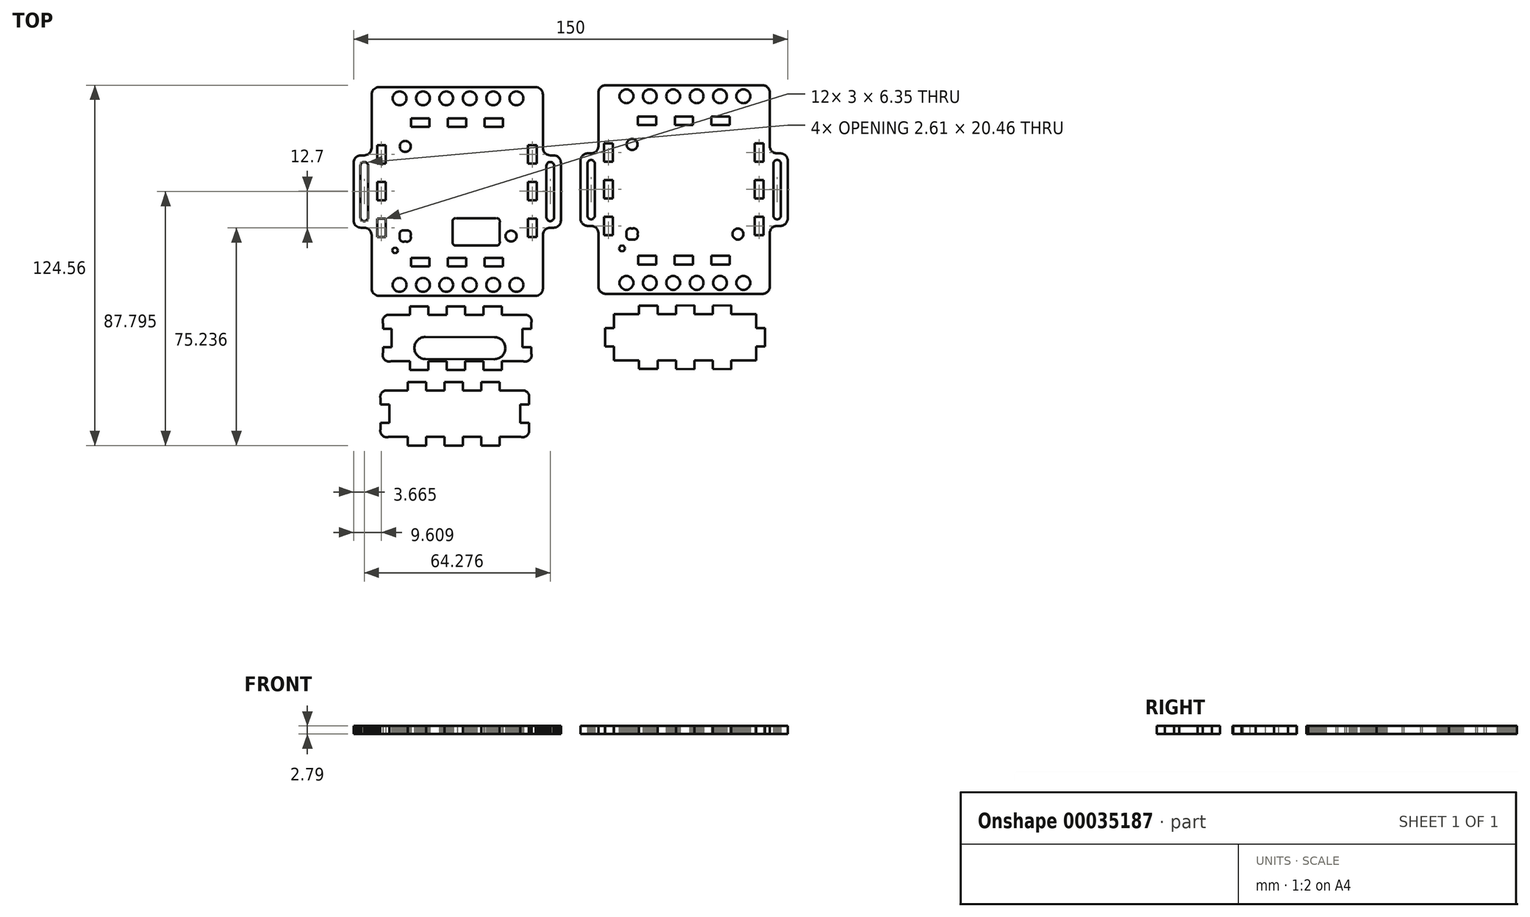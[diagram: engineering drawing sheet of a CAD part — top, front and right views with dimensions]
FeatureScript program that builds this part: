
annotation { "Feature Type Name" : "Feature", "Feature Type Description" : "" }
export const myFeature = defineFeature(function(context is Context, id is Id, definition is map)
    precondition{}
    {
        {
            var Q0;
            Q0=qCreatedBy(makeId("Top.planeOp"),FACE);
            var sketch = newSketch(context, id + "F0", { "sketchPlane" : qUnion([Q0])});
            skLineSegment(sketch, "E0", {"start": v(15.08, -72.64) * mm, "end": v(23.78, -72.67) * mm});
            skLineSegment(sketch, "E1", {"start": v(15.08, -67.86) * mm, "end": v(15.08, -72.64) * mm});
            skLineSegment(sketch, "E2", {"start": v(12.08, -61.47) * mm, "end": v(12.08, -67.86) * mm});
            skLineSegment(sketch, "E3", {"start": v(30.16, -56.69) * mm, "end": v(36.48, -56.66) * mm});
            skLineSegment(sketch, "E4", {"start": v(36.48, -56.66) * mm, "end": v(36.48, -53.69) * mm});
            skLineSegment(sketch, "E5", {"start": v(42.86, -53.67) * mm, "end": v(42.86, -56.69) * mm});
            skLineSegment(sketch, "E6", {"start": v(49.18, -56.66) * mm, "end": v(49.18, -53.69) * mm});
            skFitSpline(sketch, "E7", {"points": [v(40.44, -58.82) * mm, v(39.57, -58.82) * mm, v(38.85, -59.53) * mm, v(38.85, -60.4) * mm]});
            skLineSegment(sketch, "E8", {"start": v(23.78, -75.64) * mm, "end": v(30.16, -75.64) * mm});
            skFitSpline(sketch, "E9", {"points": [v(38.85, -66.62) * mm, v(38.85, -67.5) * mm, v(39.57, -68.2) * mm, v(40.44, -68.2) * mm]});
            skLineSegment(sketch, "E10", {"start": v(38.85, -60.4) * mm, "end": v(38.85, -66.62) * mm});
            skFitSpline(sketch, "E11", {"points": [v(53.53, -68.2) * mm, v(54.4, -68.2) * mm, v(55.12, -67.5) * mm, v(55.12, -66.62) * mm]});
            skLineSegment(sketch, "E12", {"start": v(53.53, -68.2) * mm, "end": v(40.44, -68.2) * mm});
            skFitSpline(sketch, "E13", {"points": [v(55.12, -60.4) * mm, v(55.12, -59.53) * mm, v(54.4, -58.82) * mm, v(53.53, -58.82) * mm]});
            skLineSegment(sketch, "E14", {"start": v(55.12, -60.4) * mm, "end": v(55.12, -66.62) * mm});
            skLineSegment(sketch, "E15", {"start": v(53.53, -58.82) * mm, "end": v(40.44, -58.82) * mm});
            skLineSegment(sketch, "E16", {"start": v(15.08, -61.47) * mm, "end": v(15.08, -56.69) * mm});
            skLineSegment(sketch, "E17", {"start": v(15.08, -56.69) * mm, "end": v(23.78, -56.65) * mm});
            skLineSegment(sketch, "E18", {"start": v(23.78, -56.65) * mm, "end": v(23.78, -53.69) * mm});
            skLineSegment(sketch, "E19", {"start": v(23.78, -53.69) * mm, "end": v(30.16, -53.69) * mm});
            skLineSegment(sketch, "E20", {"start": v(30.16, -53.69) * mm, "end": v(30.16, -56.69) * mm});
            skLineSegment(sketch, "E21", {"start": v(64.22, -72.64) * mm, "end": v(64.22, -67.86) * mm});
            skLineSegment(sketch, "E22", {"start": v(55.56, -72.64) * mm, "end": v(64.22, -72.64) * mm});
            skLineSegment(sketch, "E23", {"start": v(36.48, -53.69) * mm, "end": v(42.86, -53.67) * mm});
            skLineSegment(sketch, "E24", {"start": v(49.18, -75.64) * mm, "end": v(55.56, -75.66) * mm});
            skLineSegment(sketch, "E25", {"start": v(42.86, -56.69) * mm, "end": v(49.18, -56.66) * mm});
            skLineSegment(sketch, "E26", {"start": v(12.08, -67.86) * mm, "end": v(15.08, -67.86) * mm});
            skLineSegment(sketch, "E27", {"start": v(49.18, -53.69) * mm, "end": v(55.56, -53.67) * mm});
            skLineSegment(sketch, "E28", {"start": v(55.56, -53.67) * mm, "end": v(55.56, -56.69) * mm});
            skLineSegment(sketch, "E29", {"start": v(55.56, -56.69) * mm, "end": v(64.22, -56.69) * mm});
            skLineSegment(sketch, "E30", {"start": v(64.22, -56.69) * mm, "end": v(64.22, -61.47) * mm});
            skLineSegment(sketch, "E31", {"start": v(67.22, -61.47) * mm, "end": v(64.22, -61.47) * mm});
            skLineSegment(sketch, "E32", {"start": v(67.22, -67.86) * mm, "end": v(67.22, -61.47) * mm});
            skLineSegment(sketch, "E33", {"start": v(64.22, -67.86) * mm, "end": v(67.22, -67.86) * mm});
            skLineSegment(sketch, "E34", {"start": v(42.86, -75.66) * mm, "end": v(42.86, -72.64) * mm});
            skLineSegment(sketch, "E35", {"start": v(36.48, -75.64) * mm, "end": v(42.86, -75.66) * mm});
            skLineSegment(sketch, "E36", {"start": v(55.56, -75.66) * mm, "end": v(55.56, -72.64) * mm});
            skLineSegment(sketch, "E37", {"start": v(30.16, -72.64) * mm, "end": v(36.48, -72.66) * mm});
            skLineSegment(sketch, "E38", {"start": v(49.18, -72.66) * mm, "end": v(49.18, -75.64) * mm});
            skLineSegment(sketch, "E39", {"start": v(42.86, -72.64) * mm, "end": v(49.18, -72.66) * mm});
            skLineSegment(sketch, "E40", {"start": v(30.16, -75.64) * mm, "end": v(30.16, -72.64) * mm});
            skLineSegment(sketch, "E41", {"start": v(36.48, -72.66) * mm, "end": v(36.48, -75.64) * mm});
            skLineSegment(sketch, "E42", {"start": v(23.78, -72.67) * mm, "end": v(23.78, -75.64) * mm});
            skLineSegment(sketch, "E43", {"start": v(15.08, -61.47) * mm, "end": v(12.08, -61.47) * mm});
            skFitSpline(sketch, "E44", {"points": [v(-14.45, -32.95) * mm, v(-14.45, -31.3) * mm, v(-15.79, -29.95) * mm, v(-17.45, -29.95) * mm]});
            skLineSegment(sketch, "E45", {"start": v(-43.62, -29.95) * mm, "end": v(-43.62, -26.95) * mm});
            skLineSegment(sketch, "E46", {"start": v(-43.62, -26.95) * mm, "end": v(-37.27, -26.95) * mm});
            skLineSegment(sketch, "E47", {"start": v(-37.27, -26.95) * mm, "end": v(-37.27, -29.95) * mm});
            skLineSegment(sketch, "E48", {"start": v(-37.27, -29.95) * mm, "end": v(-30.92, -29.95) * mm});
            skLineSegment(sketch, "E49", {"start": v(-30.92, -29.95) * mm, "end": v(-30.92, -26.95) * mm});
            skLineSegment(sketch, "E50", {"start": v(-30.92, -26.95) * mm, "end": v(-24.57, -26.95) * mm});
            skLineSegment(sketch, "E51", {"start": v(-24.57, -26.95) * mm, "end": v(-24.57, -29.95) * mm});
            skLineSegment(sketch, "E52", {"start": v(-24.57, -29.95) * mm, "end": v(-17.45, -29.95) * mm});
            skLineSegment(sketch, "E53", {"start": v(-14.45, -32.95) * mm, "end": v(-14.45, -34.73) * mm});
            skLineSegment(sketch, "E54", {"start": v(-17.45, -34.73) * mm, "end": v(-14.45, -34.73) * mm});
            skLineSegment(sketch, "E55", {"start": v(-17.45, -41.12) * mm, "end": v(-17.45, -34.73) * mm});
            skLineSegment(sketch, "E56", {"start": v(-14.45, -41.12) * mm, "end": v(-17.45, -41.12) * mm});
            skLineSegment(sketch, "E57", {"start": v(-37.27, -48.9) * mm, "end": v(-37.27, -45.9) * mm});
            skLineSegment(sketch, "E58", {"start": v(-43.62, -48.9) * mm, "end": v(-37.27, -48.9) * mm});
            skLineSegment(sketch, "E59", {"start": v(-43.62, -45.9) * mm, "end": v(-43.62, -48.9) * mm});
            skLineSegment(sketch, "E60", {"start": v(-49.97, -45.9) * mm, "end": v(-43.62, -45.9) * mm});
            skFitSpline(sketch, "E61", {"points": [v(-17.45, -45.9) * mm, v(-15.79, -45.9) * mm, v(-14.45, -44.56) * mm, v(-14.45, -42.9) * mm]});
            skLineSegment(sketch, "E62", {"start": v(-14.45, -42.9) * mm, "end": v(-14.45, -41.12) * mm});
            skLineSegment(sketch, "E63", {"start": v(-24.57, -45.9) * mm, "end": v(-17.45, -45.9) * mm});
            skLineSegment(sketch, "E64", {"start": v(-24.57, -48.9) * mm, "end": v(-24.57, -45.9) * mm});
            skLineSegment(sketch, "E65", {"start": v(-30.92, -48.9) * mm, "end": v(-24.57, -48.9) * mm});
            skLineSegment(sketch, "E66", {"start": v(-30.92, -45.9) * mm, "end": v(-30.92, -48.9) * mm});
            skFitSpline(sketch, "E67", {"points": [v(-62.67, -29.95) * mm, v(-64.33, -29.95) * mm, v(-65.67, -31.3) * mm, v(-65.67, -32.95) * mm]});
            skLineSegment(sketch, "E68", {"start": v(-37.27, -45.9) * mm, "end": v(-30.92, -45.9) * mm});
            skLineSegment(sketch, "E69", {"start": v(-62.67, -29.95) * mm, "end": v(-56.36, -29.95) * mm});
            skLineSegment(sketch, "E70", {"start": v(-56.36, -29.95) * mm, "end": v(-56.36, -26.95) * mm});
            skLineSegment(sketch, "E71", {"start": v(-56.36, -26.95) * mm, "end": v(-49.97, -26.95) * mm});
            skLineSegment(sketch, "E72", {"start": v(-49.97, -48.9) * mm, "end": v(-49.97, -45.9) * mm});
            skLineSegment(sketch, "E73", {"start": v(-56.36, -48.9) * mm, "end": v(-49.97, -48.9) * mm});
            skLineSegment(sketch, "E74", {"start": v(-56.36, -45.9) * mm, "end": v(-56.36, -48.9) * mm});
            skLineSegment(sketch, "E75", {"start": v(-65.67, -41.12) * mm, "end": v(-65.67, -42.9) * mm});
            skLineSegment(sketch, "E76", {"start": v(-62.67, -41.12) * mm, "end": v(-65.67, -41.12) * mm});
            skLineSegment(sketch, "E77", {"start": v(-62.67, -34.73) * mm, "end": v(-62.67, -41.12) * mm});
            skLineSegment(sketch, "E78", {"start": v(-65.67, -34.73) * mm, "end": v(-62.67, -34.73) * mm});
            skFitSpline(sketch, "E79", {"points": [v(-65.67, -42.9) * mm, v(-65.67, -44.56) * mm, v(-64.33, -45.9) * mm, v(-62.67, -45.9) * mm]});
            skLineSegment(sketch, "E80", {"start": v(-62.67, -45.9) * mm, "end": v(-56.36, -45.9) * mm});
            skLineSegment(sketch, "E81", {"start": v(-49.97, -29.95) * mm, "end": v(-43.62, -29.95) * mm});
            skLineSegment(sketch, "E82", {"start": v(-65.67, -34.73) * mm, "end": v(-65.67, -32.95) * mm});
            skLineSegment(sketch, "E83", {"start": v(-49.97, -26.95) * mm, "end": v(-49.97, -29.95) * mm});
            skLineSegment(sketch, "E84", {"start": v(48.5, -26.32) * mm, "end": v(54.88, -26.3) * mm});
            skLineSegment(sketch, "E85", {"start": v(54.88, -26.3) * mm, "end": v(54.88, -29.32) * mm});
            skLineSegment(sketch, "E86", {"start": v(54.88, -29.32) * mm, "end": v(63.55, -29.32) * mm});
            skLineSegment(sketch, "E87", {"start": v(63.55, -29.32) * mm, "end": v(63.55, -34.1) * mm});
            skLineSegment(sketch, "E88", {"start": v(66.55, -34.1) * mm, "end": v(63.55, -34.1) * mm});
            skLineSegment(sketch, "E89", {"start": v(66.55, -40.48) * mm, "end": v(66.55, -34.1) * mm});
            skLineSegment(sketch, "E90", {"start": v(63.55, -40.48) * mm, "end": v(66.55, -40.48) * mm});
            skLineSegment(sketch, "E91", {"start": v(63.55, -45.27) * mm, "end": v(63.55, -40.48) * mm});
            skLineSegment(sketch, "E92", {"start": v(54.88, -45.27) * mm, "end": v(63.55, -45.27) * mm});
            skLineSegment(sketch, "E93", {"start": v(54.88, -48.29) * mm, "end": v(54.88, -45.27) * mm});
            skLineSegment(sketch, "E94", {"start": v(48.5, -48.26) * mm, "end": v(54.88, -48.29) * mm});
            skLineSegment(sketch, "E95", {"start": v(48.5, -45.29) * mm, "end": v(48.5, -48.26) * mm});
            skLineSegment(sketch, "E96", {"start": v(42.18, -45.27) * mm, "end": v(48.5, -45.29) * mm});
            skLineSegment(sketch, "E97", {"start": v(42.18, -48.29) * mm, "end": v(42.18, -45.27) * mm});
            skLineSegment(sketch, "E98", {"start": v(35.8, -48.26) * mm, "end": v(42.18, -48.29) * mm});
            skLineSegment(sketch, "E99", {"start": v(35.8, -45.29) * mm, "end": v(35.8, -48.26) * mm});
            skLineSegment(sketch, "E100", {"start": v(29.48, -45.27) * mm, "end": v(35.8, -45.29) * mm});
            skLineSegment(sketch, "E101", {"start": v(29.48, -48.26) * mm, "end": v(29.48, -45.27) * mm});
            skLineSegment(sketch, "E102", {"start": v(23.1, -48.26) * mm, "end": v(29.48, -48.26) * mm});
            skLineSegment(sketch, "E103", {"start": v(23.1, -45.3) * mm, "end": v(23.1, -48.26) * mm});
            skLineSegment(sketch, "E104", {"start": v(14.4, -45.27) * mm, "end": v(23.1, -45.3) * mm});
            skLineSegment(sketch, "E105", {"start": v(14.4, -40.48) * mm, "end": v(14.4, -45.27) * mm});
            skLineSegment(sketch, "E106", {"start": v(11.4, -40.48) * mm, "end": v(14.4, -40.48) * mm});
            skLineSegment(sketch, "E107", {"start": v(11.4, -34.1) * mm, "end": v(11.4, -40.48) * mm});
            skLineSegment(sketch, "E108", {"start": v(14.4, -34.1) * mm, "end": v(11.4, -34.1) * mm});
            skLineSegment(sketch, "E109", {"start": v(14.4, -34.1) * mm, "end": v(14.4, -29.32) * mm});
            skLineSegment(sketch, "E110", {"start": v(14.4, -29.32) * mm, "end": v(23.1, -29.28) * mm});
            skLineSegment(sketch, "E111", {"start": v(23.1, -29.28) * mm, "end": v(23.1, -26.32) * mm});
            skLineSegment(sketch, "E112", {"start": v(23.1, -26.32) * mm, "end": v(29.48, -26.32) * mm});
            skLineSegment(sketch, "E113", {"start": v(29.48, -26.32) * mm, "end": v(29.48, -29.32) * mm});
            skLineSegment(sketch, "E114", {"start": v(29.48, -29.32) * mm, "end": v(35.8, -29.3) * mm});
            skLineSegment(sketch, "E115", {"start": v(35.8, -29.3) * mm, "end": v(35.8, -26.32) * mm});
            skLineSegment(sketch, "E116", {"start": v(35.8, -26.32) * mm, "end": v(42.18, -26.3) * mm});
            skLineSegment(sketch, "E117", {"start": v(42.18, -26.3) * mm, "end": v(42.18, -29.32) * mm});
            skLineSegment(sketch, "E118", {"start": v(42.18, -29.32) * mm, "end": v(48.5, -29.3) * mm});
            skLineSegment(sketch, "E119", {"start": v(48.5, -29.3) * mm, "end": v(48.5, -26.32) * mm});
            skLineSegment(sketch, "E120", {"start": v(-13.64, -14.97) * mm, "end": v(-16.64, -14.97) * mm});
            skFitSpline(sketch, "E121", {"points": [v(-16.64, -19.76) * mm, v(-14.98, -19.76) * mm, v(-13.64, -18.4) * mm, v(-13.64, -16.76) * mm]});
            skLineSegment(sketch, "E122", {"start": v(-13.64, -16.76) * mm, "end": v(-13.64, -14.97) * mm});
            skLineSegment(sketch, "E123", {"start": v(-23.76, -19.76) * mm, "end": v(-16.64, -19.76) * mm});
            skLineSegment(sketch, "E124", {"start": v(-23.76, -22.75) * mm, "end": v(-23.76, -19.76) * mm});
            skLineSegment(sketch, "E125", {"start": v(-30.1, -22.75) * mm, "end": v(-23.76, -22.75) * mm});
            skLineSegment(sketch, "E126", {"start": v(-30.1, -19.76) * mm, "end": v(-30.1, -22.75) * mm});
            skLineSegment(sketch, "E127", {"start": v(-36.46, -19.76) * mm, "end": v(-30.1, -19.76) * mm});
            skLineSegment(sketch, "E128", {"start": v(-36.46, -22.75) * mm, "end": v(-36.46, -19.76) * mm});
            skLineSegment(sketch, "E129", {"start": v(-42.8, -22.75) * mm, "end": v(-36.46, -22.75) * mm});
            skLineSegment(sketch, "E130", {"start": v(-42.8, -19.76) * mm, "end": v(-42.8, -22.75) * mm});
            skLineSegment(sketch, "E131", {"start": v(-49.16, -19.76) * mm, "end": v(-42.8, -19.76) * mm});
            skLineSegment(sketch, "E132", {"start": v(-49.16, -22.75) * mm, "end": v(-49.16, -19.76) * mm});
            skLineSegment(sketch, "E133", {"start": v(-55.55, -22.75) * mm, "end": v(-49.16, -22.75) * mm});
            skLineSegment(sketch, "E134", {"start": v(-55.55, -19.76) * mm, "end": v(-55.55, -22.75) * mm});
            skFitSpline(sketch, "E135", {"points": [v(-64.86, -16.76) * mm, v(-64.86, -18.4) * mm, v(-63.52, -19.76) * mm, v(-61.87, -19.76) * mm]});
            skLineSegment(sketch, "E136", {"start": v(-61.87, -19.76) * mm, "end": v(-55.55, -19.76) * mm});
            skLineSegment(sketch, "E137", {"start": v(-64.86, -14.97) * mm, "end": v(-64.86, -16.76) * mm});
            skLineSegment(sketch, "E138", {"start": v(-61.86, -14.97) * mm, "end": v(-64.86, -14.97) * mm});
            skLineSegment(sketch, "E139", {"start": v(-61.86, -8.59) * mm, "end": v(-61.86, -14.97) * mm});
            skLineSegment(sketch, "E140", {"start": v(-64.86, -8.59) * mm, "end": v(-61.86, -8.59) * mm});
            skFitSpline(sketch, "E141", {"points": [v(-61.87, -3.8) * mm, v(-63.52, -3.8) * mm, v(-64.86, -5.15) * mm, v(-64.86, -6.8) * mm]});
            skLineSegment(sketch, "E142", {"start": v(-64.86, -8.59) * mm, "end": v(-64.86, -6.8) * mm});
            skLineSegment(sketch, "E143", {"start": v(-61.87, -3.8) * mm, "end": v(-55.55, -3.8) * mm});
            skLineSegment(sketch, "E144", {"start": v(-55.55, -3.8) * mm, "end": v(-55.55, -0.8) * mm});
            skLineSegment(sketch, "E145", {"start": v(-55.55, -0.8) * mm, "end": v(-49.16, -0.8) * mm});
            skFitSpline(sketch, "E146", {"points": [v(-13.64, -6.8) * mm, v(-13.64, -5.15) * mm, v(-14.98, -3.8) * mm, v(-16.64, -3.8) * mm]});
            skLineSegment(sketch, "E147", {"start": v(-49.16, -3.8) * mm, "end": v(-42.8, -3.8) * mm});
            skLineSegment(sketch, "E148", {"start": v(-42.8, -3.8) * mm, "end": v(-42.8, -0.8) * mm});
            skLineSegment(sketch, "E149", {"start": v(-42.8, -0.8) * mm, "end": v(-36.46, -0.8) * mm});
            skLineSegment(sketch, "E150", {"start": v(-36.46, -0.8) * mm, "end": v(-36.46, -3.8) * mm});
            skLineSegment(sketch, "E151", {"start": v(-36.46, -3.8) * mm, "end": v(-30.1, -3.8) * mm});
            skLineSegment(sketch, "E152", {"start": v(-30.1, -3.8) * mm, "end": v(-30.1, -0.8) * mm});
            skLineSegment(sketch, "E153", {"start": v(-30.1, -0.8) * mm, "end": v(-23.76, -0.8) * mm});
            skLineSegment(sketch, "E154", {"start": v(-23.76, -0.8) * mm, "end": v(-23.76, -3.8) * mm});
            skLineSegment(sketch, "E155", {"start": v(-23.76, -3.8) * mm, "end": v(-16.64, -3.8) * mm});
            skLineSegment(sketch, "E156", {"start": v(-13.64, -6.8) * mm, "end": v(-13.64, -8.59) * mm});
            skLineSegment(sketch, "E157", {"start": v(-16.64, -8.59) * mm, "end": v(-13.64, -8.59) * mm});
            skLineSegment(sketch, "E158", {"start": v(-16.64, -14.97) * mm, "end": v(-16.64, -8.59) * mm});
            skLineSegment(sketch, "E159", {"start": v(-49.16, -0.8) * mm, "end": v(-49.16, -3.8) * mm});
            skLineSegment(sketch, "E160", {"start": v(64.1, -14.68) * mm, "end": v(67.1, -14.68) * mm});
            skLineSegment(sketch, "E161", {"start": v(64.1, -19.46) * mm, "end": v(64.1, -14.68) * mm});
            skLineSegment(sketch, "E162", {"start": v(55.42, -19.46) * mm, "end": v(64.1, -19.46) * mm});
            skLineSegment(sketch, "E163", {"start": v(55.42, -22.48) * mm, "end": v(55.42, -19.46) * mm});
            skLineSegment(sketch, "E164", {"start": v(49.05, -22.46) * mm, "end": v(55.42, -22.48) * mm});
            skLineSegment(sketch, "E165", {"start": v(49.05, -19.49) * mm, "end": v(49.05, -22.46) * mm});
            skLineSegment(sketch, "E166", {"start": v(42.72, -19.46) * mm, "end": v(49.05, -19.49) * mm});
            skLineSegment(sketch, "E167", {"start": v(42.72, -22.48) * mm, "end": v(42.72, -19.46) * mm});
            skLineSegment(sketch, "E168", {"start": v(36.35, -22.46) * mm, "end": v(42.72, -22.48) * mm});
            skLineSegment(sketch, "E169", {"start": v(36.35, -19.49) * mm, "end": v(36.35, -22.46) * mm});
            skLineSegment(sketch, "E170", {"start": v(30.02, -19.46) * mm, "end": v(36.35, -19.49) * mm});
            skLineSegment(sketch, "E171", {"start": v(30.02, -22.46) * mm, "end": v(30.02, -19.46) * mm});
            skLineSegment(sketch, "E172", {"start": v(23.65, -22.46) * mm, "end": v(30.02, -22.46) * mm});
            skLineSegment(sketch, "E173", {"start": v(23.65, -19.49) * mm, "end": v(23.65, -22.46) * mm});
            skLineSegment(sketch, "E174", {"start": v(14.95, -19.46) * mm, "end": v(23.65, -19.49) * mm});
            skLineSegment(sketch, "E175", {"start": v(14.95, -14.68) * mm, "end": v(14.95, -19.46) * mm});
            skLineSegment(sketch, "E176", {"start": v(11.95, -14.68) * mm, "end": v(14.95, -14.68) * mm});
            skLineSegment(sketch, "E177", {"start": v(11.95, -8.29) * mm, "end": v(11.95, -14.68) * mm});
            skLineSegment(sketch, "E178", {"start": v(14.95, -8.29) * mm, "end": v(11.95, -8.29) * mm});
            skLineSegment(sketch, "E179", {"start": v(14.95, -8.29) * mm, "end": v(14.95, -3.5) * mm});
            skLineSegment(sketch, "E180", {"start": v(14.95, -3.5) * mm, "end": v(23.65, -3.48) * mm});
            skLineSegment(sketch, "E181", {"start": v(23.65, -3.48) * mm, "end": v(23.65, -0.5) * mm});
            skLineSegment(sketch, "E182", {"start": v(23.65, -0.5) * mm, "end": v(30.02, -0.5) * mm});
            skLineSegment(sketch, "E183", {"start": v(30.02, -0.5) * mm, "end": v(30.02, -3.5) * mm});
            skLineSegment(sketch, "E184", {"start": v(30.02, -3.5) * mm, "end": v(36.35, -3.49) * mm});
            skLineSegment(sketch, "E185", {"start": v(36.35, -3.49) * mm, "end": v(36.35, -0.5) * mm});
            skLineSegment(sketch, "E186", {"start": v(36.35, -0.5) * mm, "end": v(42.72, -0.49) * mm});
            skLineSegment(sketch, "E187", {"start": v(42.72, -0.49) * mm, "end": v(42.72, -3.5) * mm});
            skLineSegment(sketch, "E188", {"start": v(42.72, -3.5) * mm, "end": v(49.05, -3.49) * mm});
            skLineSegment(sketch, "E189", {"start": v(49.05, -3.49) * mm, "end": v(49.05, -0.5) * mm});
            skLineSegment(sketch, "E190", {"start": v(49.05, -0.5) * mm, "end": v(55.42, -0.49) * mm});
            skLineSegment(sketch, "E191", {"start": v(55.42, -0.49) * mm, "end": v(55.42, -3.5) * mm});
            skLineSegment(sketch, "E192", {"start": v(55.42, -3.5) * mm, "end": v(64.1, -3.5) * mm});
            skLineSegment(sketch, "E193", {"start": v(64.1, -3.5) * mm, "end": v(64.1, -8.29) * mm});
            skLineSegment(sketch, "E194", {"start": v(67.1, -8.29) * mm, "end": v(64.1, -8.29) * mm});
            skLineSegment(sketch, "E195", {"start": v(67.1, -14.68) * mm, "end": v(67.1, -8.29) * mm});
            skLineSegment(sketch, "E196", {"start": v(5.93, 27.05) * mm, "end": v(7.06, 27.05) * mm});
            skLineSegment(sketch, "E197", {"start": v(7.06, 52.1) * mm, "end": v(5.93, 52.1) * mm});
            skLineSegment(sketch, "E198", {"start": v(72.46, 52.1) * mm, "end": v(71.34, 52.1) * mm});
            skLineSegment(sketch, "E199", {"start": v(71.34, 27.05) * mm, "end": v(72.46, 27.05) * mm});
            skLineSegment(sketch, "E200", {"start": v(59.66, 24.58) * mm, "end": v(59.55, 24.93) * mm});
            skLineSegment(sketch, "E201", {"start": v(59.55, 24.93) * mm, "end": v(59.38, 25.25) * mm});
            skLineSegment(sketch, "E202", {"start": v(59.38, 25.25) * mm, "end": v(59.13, 25.56) * mm});
            skLineSegment(sketch, "E203", {"start": v(59.13, 25.56) * mm, "end": v(58.85, 25.78) * mm});
            skLineSegment(sketch, "E204", {"start": v(58.85, 25.78) * mm, "end": v(58.53, 25.95) * mm});
            skLineSegment(sketch, "E205", {"start": v(58.53, 25.95) * mm, "end": v(58.14, 26.06) * mm});
            skLineSegment(sketch, "E206", {"start": v(58.14, 26.06) * mm, "end": v(57.79, 26.1) * mm});
            skLineSegment(sketch, "E207", {"start": v(57.79, 26.1) * mm, "end": v(57.4, 26.06) * mm});
            skLineSegment(sketch, "E208", {"start": v(57.4, 26.06) * mm, "end": v(57.05, 25.95) * mm});
            skLineSegment(sketch, "E209", {"start": v(57.05, 25.95) * mm, "end": v(56.73, 25.78) * mm});
            skLineSegment(sketch, "E210", {"start": v(56.73, 25.78) * mm, "end": v(56.45, 25.56) * mm});
            skLineSegment(sketch, "E211", {"start": v(56.45, 25.56) * mm, "end": v(56.2, 25.25) * mm});
            skLineSegment(sketch, "E212", {"start": v(56.2, 25.25) * mm, "end": v(56.02, 24.93) * mm});
            skLineSegment(sketch, "E213", {"start": v(56.02, 24.93) * mm, "end": v(55.92, 24.58) * mm});
            skLineSegment(sketch, "E214", {"start": v(55.92, 24.58) * mm, "end": v(55.88, 24.22) * mm});
            skLineSegment(sketch, "E215", {"start": v(55.88, 24.22) * mm, "end": v(55.92, 23.84) * mm});
            skLineSegment(sketch, "E216", {"start": v(55.92, 23.84) * mm, "end": v(56.02, 23.48) * mm});
            skLineSegment(sketch, "E217", {"start": v(56.02, 23.48) * mm, "end": v(56.2, 23.17) * mm});
            skLineSegment(sketch, "E218", {"start": v(56.2, 23.17) * mm, "end": v(56.45, 22.88) * mm});
            skLineSegment(sketch, "E219", {"start": v(56.45, 22.88) * mm, "end": v(56.73, 22.64) * mm});
            skLineSegment(sketch, "E220", {"start": v(56.73, 22.64) * mm, "end": v(57.05, 22.46) * mm});
            skLineSegment(sketch, "E221", {"start": v(57.05, 22.46) * mm, "end": v(57.4, 22.35) * mm});
            skLineSegment(sketch, "E222", {"start": v(57.4, 22.35) * mm, "end": v(57.79, 22.32) * mm});
            skLineSegment(sketch, "E223", {"start": v(57.79, 22.32) * mm, "end": v(58.14, 22.35) * mm});
            skLineSegment(sketch, "E224", {"start": v(58.14, 22.35) * mm, "end": v(58.53, 22.46) * mm});
            skLineSegment(sketch, "E225", {"start": v(58.53, 22.46) * mm, "end": v(58.85, 22.64) * mm});
            skLineSegment(sketch, "E226", {"start": v(58.85, 22.64) * mm, "end": v(59.13, 22.88) * mm});
            skLineSegment(sketch, "E227", {"start": v(59.13, 22.88) * mm, "end": v(59.38, 23.17) * mm});
            skLineSegment(sketch, "E228", {"start": v(59.38, 23.17) * mm, "end": v(59.55, 23.48) * mm});
            skLineSegment(sketch, "E229", {"start": v(59.55, 23.48) * mm, "end": v(59.66, 23.84) * mm});
            skLineSegment(sketch, "E230", {"start": v(59.66, 23.84) * mm, "end": v(59.7, 24.22) * mm});
            skLineSegment(sketch, "E231", {"start": v(59.7, 24.22) * mm, "end": v(59.66, 24.58) * mm});
            skLineSegment(sketch, "E232", {"start": v(66.64, 55.59) * mm, "end": v(63.64, 55.59) * mm});
            skLineSegment(sketch, "E233", {"start": v(63.64, 55.59) * mm, "end": v(63.64, 49.24) * mm});
            skLineSegment(sketch, "E234", {"start": v(63.64, 49.24) * mm, "end": v(66.64, 49.24) * mm});
            skLineSegment(sketch, "E235", {"start": v(66.64, 49.24) * mm, "end": v(66.64, 55.59) * mm});
            skLineSegment(sketch, "E236", {"start": v(37.75, 72.27) * mm, "end": v(37.65, 72.66) * mm});
            skLineSegment(sketch, "E237", {"start": v(37.65, 72.66) * mm, "end": v(37.47, 73.05) * mm});
            skLineSegment(sketch, "E238", {"start": v(37.47, 73.05) * mm, "end": v(37.22, 73.37) * mm});
            skLineSegment(sketch, "E239", {"start": v(37.22, 73.37) * mm, "end": v(36.94, 73.68) * mm});
            skLineSegment(sketch, "E240", {"start": v(36.94, 73.68) * mm, "end": v(36.59, 73.9) * mm});
            skLineSegment(sketch, "E241", {"start": v(36.59, 73.9) * mm, "end": v(36.2, 74.07) * mm});
            skLineSegment(sketch, "E242", {"start": v(36.2, 74.07) * mm, "end": v(35.81, 74.21) * mm});
            skLineSegment(sketch, "E243", {"start": v(35.81, 74.21) * mm, "end": v(35.39, 74.25) * mm});
            skLineSegment(sketch, "E244", {"start": v(35.39, 74.25) * mm, "end": v(35, 74.21) * mm});
            skLineSegment(sketch, "E245", {"start": v(35, 74.21) * mm, "end": v(34.58, 74.07) * mm});
            skLineSegment(sketch, "E246", {"start": v(34.58, 74.07) * mm, "end": v(34.19, 73.9) * mm});
            skLineSegment(sketch, "E247", {"start": v(34.19, 73.9) * mm, "end": v(33.87, 73.68) * mm});
            skLineSegment(sketch, "E248", {"start": v(33.87, 73.68) * mm, "end": v(33.55, 73.37) * mm});
            skLineSegment(sketch, "E249", {"start": v(33.55, 73.37) * mm, "end": v(33.34, 73.05) * mm});
            skLineSegment(sketch, "E250", {"start": v(33.34, 73.05) * mm, "end": v(33.16, 72.66) * mm});
            skLineSegment(sketch, "E251", {"start": v(33.16, 72.66) * mm, "end": v(33.06, 72.27) * mm});
            skLineSegment(sketch, "E252", {"start": v(33.06, 72.27) * mm, "end": v(33.02, 71.85) * mm});
            skLineSegment(sketch, "E253", {"start": v(33.02, 71.85) * mm, "end": v(33.06, 71.43) * mm});
            skLineSegment(sketch, "E254", {"start": v(33.06, 71.43) * mm, "end": v(33.16, 71.04) * mm});
            skLineSegment(sketch, "E255", {"start": v(33.16, 71.04) * mm, "end": v(33.34, 70.65) * mm});
            skLineSegment(sketch, "E256", {"start": v(33.34, 70.65) * mm, "end": v(33.55, 70.3) * mm});
            skLineSegment(sketch, "E257", {"start": v(33.55, 70.3) * mm, "end": v(33.87, 70.01) * mm});
            skLineSegment(sketch, "E258", {"start": v(33.87, 70.01) * mm, "end": v(34.19, 69.77) * mm});
            skLineSegment(sketch, "E259", {"start": v(34.19, 69.77) * mm, "end": v(34.58, 69.6) * mm});
            skLineSegment(sketch, "E260", {"start": v(34.58, 69.6) * mm, "end": v(35, 69.49) * mm});
            skLineSegment(sketch, "E261", {"start": v(35, 69.49) * mm, "end": v(35.39, 69.45) * mm});
            skLineSegment(sketch, "E262", {"start": v(35.39, 69.45) * mm, "end": v(35.81, 69.49) * mm});
            skLineSegment(sketch, "E263", {"start": v(35.81, 69.49) * mm, "end": v(36.2, 69.6) * mm});
            skLineSegment(sketch, "E264", {"start": v(36.2, 69.6) * mm, "end": v(36.59, 69.77) * mm});
            skLineSegment(sketch, "E265", {"start": v(36.59, 69.77) * mm, "end": v(36.94, 70.01) * mm});
            skLineSegment(sketch, "E266", {"start": v(36.94, 70.01) * mm, "end": v(37.22, 70.3) * mm});
            skLineSegment(sketch, "E267", {"start": v(37.22, 70.3) * mm, "end": v(37.47, 70.65) * mm});
            skLineSegment(sketch, "E268", {"start": v(37.47, 70.65) * mm, "end": v(37.65, 71.04) * mm});
            skLineSegment(sketch, "E269", {"start": v(37.65, 71.04) * mm, "end": v(37.75, 71.43) * mm});
            skLineSegment(sketch, "E270", {"start": v(37.75, 71.43) * mm, "end": v(37.79, 71.85) * mm});
            skLineSegment(sketch, "E271", {"start": v(37.79, 71.85) * mm, "end": v(37.75, 72.27) * mm});
            skLineSegment(sketch, "E272", {"start": v(53.94, 72.27) * mm, "end": v(53.84, 72.66) * mm});
            skLineSegment(sketch, "E273", {"start": v(53.84, 72.66) * mm, "end": v(53.66, 73.05) * mm});
            skLineSegment(sketch, "E274", {"start": v(53.66, 73.05) * mm, "end": v(53.41, 73.37) * mm});
            skLineSegment(sketch, "E275", {"start": v(53.41, 73.37) * mm, "end": v(53.13, 73.68) * mm});
            skLineSegment(sketch, "E276", {"start": v(53.13, 73.68) * mm, "end": v(52.78, 73.9) * mm});
            skLineSegment(sketch, "E277", {"start": v(52.78, 73.9) * mm, "end": v(52.43, 74.07) * mm});
            skLineSegment(sketch, "E278", {"start": v(52.43, 74.07) * mm, "end": v(52, 74.21) * mm});
            skLineSegment(sketch, "E279", {"start": v(52, 74.21) * mm, "end": v(51.58, 74.25) * mm});
            skLineSegment(sketch, "E280", {"start": v(51.58, 74.25) * mm, "end": v(51.2, 74.21) * mm});
            skLineSegment(sketch, "E281", {"start": v(51.2, 74.21) * mm, "end": v(50.77, 74.07) * mm});
            skLineSegment(sketch, "E282", {"start": v(50.77, 74.07) * mm, "end": v(50.38, 73.9) * mm});
            skLineSegment(sketch, "E283", {"start": v(50.38, 73.9) * mm, "end": v(50.06, 73.68) * mm});
            skLineSegment(sketch, "E284", {"start": v(50.06, 73.68) * mm, "end": v(49.75, 73.37) * mm});
            skLineSegment(sketch, "E285", {"start": v(49.75, 73.37) * mm, "end": v(49.53, 73.05) * mm});
            skLineSegment(sketch, "E286", {"start": v(49.53, 73.05) * mm, "end": v(49.36, 72.66) * mm});
            skLineSegment(sketch, "E287", {"start": v(49.36, 72.66) * mm, "end": v(49.25, 72.27) * mm});
            skLineSegment(sketch, "E288", {"start": v(49.25, 72.27) * mm, "end": v(49.22, 71.85) * mm});
            skLineSegment(sketch, "E289", {"start": v(49.22, 71.85) * mm, "end": v(49.25, 71.43) * mm});
            skLineSegment(sketch, "E290", {"start": v(49.25, 71.43) * mm, "end": v(49.36, 71.04) * mm});
            skLineSegment(sketch, "E291", {"start": v(49.36, 71.04) * mm, "end": v(49.53, 70.65) * mm});
            skLineSegment(sketch, "E292", {"start": v(49.53, 70.65) * mm, "end": v(49.75, 70.3) * mm});
            skLineSegment(sketch, "E293", {"start": v(49.75, 70.3) * mm, "end": v(50.06, 70.01) * mm});
            skLineSegment(sketch, "E294", {"start": v(50.06, 70.01) * mm, "end": v(50.38, 69.77) * mm});
            skLineSegment(sketch, "E295", {"start": v(50.38, 69.77) * mm, "end": v(50.77, 69.6) * mm});
            skLineSegment(sketch, "E296", {"start": v(50.77, 69.6) * mm, "end": v(51.2, 69.49) * mm});
            skLineSegment(sketch, "E297", {"start": v(51.2, 69.49) * mm, "end": v(51.58, 69.45) * mm});
            skLineSegment(sketch, "E298", {"start": v(51.58, 69.45) * mm, "end": v(52, 69.49) * mm});
            skLineSegment(sketch, "E299", {"start": v(52, 69.49) * mm, "end": v(52.43, 69.6) * mm});
            skLineSegment(sketch, "E300", {"start": v(52.43, 69.6) * mm, "end": v(52.78, 69.77) * mm});
            skLineSegment(sketch, "E301", {"start": v(52.78, 69.77) * mm, "end": v(53.13, 70.01) * mm});
            skLineSegment(sketch, "E302", {"start": v(53.13, 70.01) * mm, "end": v(53.41, 70.3) * mm});
            skLineSegment(sketch, "E303", {"start": v(53.41, 70.3) * mm, "end": v(53.66, 70.65) * mm});
            skLineSegment(sketch, "E304", {"start": v(53.66, 70.65) * mm, "end": v(53.84, 71.04) * mm});
            skLineSegment(sketch, "E305", {"start": v(53.84, 71.04) * mm, "end": v(53.94, 71.43) * mm});
            skLineSegment(sketch, "E306", {"start": v(53.94, 71.43) * mm, "end": v(53.98, 71.85) * mm});
            skLineSegment(sketch, "E307", {"start": v(53.98, 71.85) * mm, "end": v(53.94, 72.27) * mm});
            skLineSegment(sketch, "E308", {"start": v(57.3, 6.9) * mm, "end": v(57.4, 6.51) * mm});
            skLineSegment(sketch, "E309", {"start": v(57.4, 6.51) * mm, "end": v(57.58, 6.13) * mm});
            skLineSegment(sketch, "E310", {"start": v(57.58, 6.13) * mm, "end": v(57.82, 5.8) * mm});
            skLineSegment(sketch, "E311", {"start": v(57.82, 5.8) * mm, "end": v(58.1, 5.5) * mm});
            skLineSegment(sketch, "E312", {"start": v(58.1, 5.5) * mm, "end": v(58.46, 5.24) * mm});
            skLineSegment(sketch, "E313", {"start": v(58.46, 5.24) * mm, "end": v(58.85, 5.07) * mm});
            skLineSegment(sketch, "E314", {"start": v(58.85, 5.07) * mm, "end": v(59.24, 4.96) * mm});
            skLineSegment(sketch, "E315", {"start": v(59.24, 4.96) * mm, "end": v(59.66, 4.93) * mm});
            skLineSegment(sketch, "E316", {"start": v(59.66, 4.93) * mm, "end": v(60.08, 4.96) * mm});
            skLineSegment(sketch, "E317", {"start": v(60.08, 4.96) * mm, "end": v(60.47, 5.07) * mm});
            skLineSegment(sketch, "E318", {"start": v(60.47, 5.07) * mm, "end": v(60.86, 5.24) * mm});
            skLineSegment(sketch, "E319", {"start": v(60.86, 5.24) * mm, "end": v(61.18, 5.5) * mm});
            skLineSegment(sketch, "E320", {"start": v(61.18, 5.5) * mm, "end": v(61.5, 5.8) * mm});
            skLineSegment(sketch, "E321", {"start": v(61.5, 5.8) * mm, "end": v(61.74, 6.13) * mm});
            skLineSegment(sketch, "E322", {"start": v(61.74, 6.13) * mm, "end": v(61.92, 6.51) * mm});
            skLineSegment(sketch, "E323", {"start": v(61.92, 6.51) * mm, "end": v(62.02, 6.9) * mm});
            skLineSegment(sketch, "E324", {"start": v(62.02, 6.9) * mm, "end": v(62.06, 7.33) * mm});
            skLineSegment(sketch, "E325", {"start": v(62.06, 7.33) * mm, "end": v(62.02, 7.75) * mm});
            skLineSegment(sketch, "E326", {"start": v(62.02, 7.75) * mm, "end": v(61.92, 8.14) * mm});
            skLineSegment(sketch, "E327", {"start": v(61.92, 8.14) * mm, "end": v(61.74, 8.53) * mm});
            skLineSegment(sketch, "E328", {"start": v(61.74, 8.53) * mm, "end": v(61.5, 8.88) * mm});
            skLineSegment(sketch, "E329", {"start": v(61.5, 8.88) * mm, "end": v(61.18, 9.16) * mm});
            skLineSegment(sketch, "E330", {"start": v(61.18, 9.16) * mm, "end": v(60.86, 9.4) * mm});
            skLineSegment(sketch, "E331", {"start": v(60.86, 9.4) * mm, "end": v(60.47, 9.58) * mm});
            skLineSegment(sketch, "E332", {"start": v(60.47, 9.58) * mm, "end": v(60.08, 9.69) * mm});
            skLineSegment(sketch, "E333", {"start": v(60.08, 9.69) * mm, "end": v(59.66, 9.73) * mm});
            skLineSegment(sketch, "E334", {"start": v(59.66, 9.73) * mm, "end": v(59.24, 9.69) * mm});
            skLineSegment(sketch, "E335", {"start": v(59.24, 9.69) * mm, "end": v(58.85, 9.58) * mm});
            skLineSegment(sketch, "E336", {"start": v(58.85, 9.58) * mm, "end": v(58.46, 9.4) * mm});
            skLineSegment(sketch, "E337", {"start": v(58.46, 9.4) * mm, "end": v(58.1, 9.16) * mm});
            skLineSegment(sketch, "E338", {"start": v(58.1, 9.16) * mm, "end": v(57.82, 8.88) * mm});
            skLineSegment(sketch, "E339", {"start": v(57.82, 8.88) * mm, "end": v(57.58, 8.53) * mm});
            skLineSegment(sketch, "E340", {"start": v(57.58, 8.53) * mm, "end": v(57.4, 8.14) * mm});
            skLineSegment(sketch, "E341", {"start": v(57.4, 8.14) * mm, "end": v(57.3, 7.75) * mm});
            skLineSegment(sketch, "E342", {"start": v(57.3, 7.75) * mm, "end": v(57.26, 7.33) * mm});
            skLineSegment(sketch, "E343", {"start": v(57.26, 7.33) * mm, "end": v(57.3, 6.9) * mm});
            skLineSegment(sketch, "E344", {"start": v(41.17, 6.9) * mm, "end": v(41.28, 6.51) * mm});
            skLineSegment(sketch, "E345", {"start": v(41.28, 6.51) * mm, "end": v(41.46, 6.13) * mm});
            skLineSegment(sketch, "E346", {"start": v(41.46, 6.13) * mm, "end": v(41.7, 5.8) * mm});
            skLineSegment(sketch, "E347", {"start": v(41.7, 5.8) * mm, "end": v(41.98, 5.5) * mm});
            skLineSegment(sketch, "E348", {"start": v(41.98, 5.5) * mm, "end": v(42.34, 5.24) * mm});
            skLineSegment(sketch, "E349", {"start": v(42.34, 5.24) * mm, "end": v(42.73, 5.07) * mm});
            skLineSegment(sketch, "E350", {"start": v(42.73, 5.07) * mm, "end": v(43.11, 4.96) * mm});
            skLineSegment(sketch, "E351", {"start": v(43.11, 4.96) * mm, "end": v(43.54, 4.93) * mm});
            skLineSegment(sketch, "E352", {"start": v(43.54, 4.93) * mm, "end": v(43.92, 4.96) * mm});
            skLineSegment(sketch, "E353", {"start": v(43.92, 4.96) * mm, "end": v(44.35, 5.07) * mm});
            skLineSegment(sketch, "E354", {"start": v(44.35, 5.07) * mm, "end": v(44.74, 5.24) * mm});
            skLineSegment(sketch, "E355", {"start": v(44.74, 5.24) * mm, "end": v(45.05, 5.5) * mm});
            skLineSegment(sketch, "E356", {"start": v(45.05, 5.5) * mm, "end": v(45.37, 5.8) * mm});
            skLineSegment(sketch, "E357", {"start": v(45.37, 5.8) * mm, "end": v(45.58, 6.13) * mm});
            skLineSegment(sketch, "E358", {"start": v(45.58, 6.13) * mm, "end": v(45.76, 6.51) * mm});
            skLineSegment(sketch, "E359", {"start": v(45.76, 6.51) * mm, "end": v(45.86, 6.9) * mm});
            skLineSegment(sketch, "E360", {"start": v(45.86, 6.9) * mm, "end": v(45.9, 7.33) * mm});
            skLineSegment(sketch, "E361", {"start": v(45.9, 7.33) * mm, "end": v(45.86, 7.75) * mm});
            skLineSegment(sketch, "E362", {"start": v(45.86, 7.75) * mm, "end": v(45.76, 8.14) * mm});
            skLineSegment(sketch, "E363", {"start": v(45.76, 8.14) * mm, "end": v(45.58, 8.53) * mm});
            skLineSegment(sketch, "E364", {"start": v(45.58, 8.53) * mm, "end": v(45.37, 8.88) * mm});
            skLineSegment(sketch, "E365", {"start": v(45.37, 8.88) * mm, "end": v(45.05, 9.16) * mm});
            skLineSegment(sketch, "E366", {"start": v(45.05, 9.16) * mm, "end": v(44.74, 9.4) * mm});
            skLineSegment(sketch, "E367", {"start": v(44.74, 9.4) * mm, "end": v(44.35, 9.58) * mm});
            skLineSegment(sketch, "E368", {"start": v(44.35, 9.58) * mm, "end": v(43.92, 9.69) * mm});
            skLineSegment(sketch, "E369", {"start": v(43.92, 9.69) * mm, "end": v(43.54, 9.73) * mm});
            skLineSegment(sketch, "E370", {"start": v(43.54, 9.73) * mm, "end": v(43.11, 9.69) * mm});
            skLineSegment(sketch, "E371", {"start": v(43.11, 9.69) * mm, "end": v(42.73, 9.58) * mm});
            skLineSegment(sketch, "E372", {"start": v(42.73, 9.58) * mm, "end": v(42.34, 9.4) * mm});
            skLineSegment(sketch, "E373", {"start": v(42.34, 9.4) * mm, "end": v(41.98, 9.16) * mm});
            skLineSegment(sketch, "E374", {"start": v(41.98, 9.16) * mm, "end": v(41.7, 8.88) * mm});
            skLineSegment(sketch, "E375", {"start": v(41.7, 8.88) * mm, "end": v(41.46, 8.53) * mm});
            skLineSegment(sketch, "E376", {"start": v(41.46, 8.53) * mm, "end": v(41.28, 8.14) * mm});
            skLineSegment(sketch, "E377", {"start": v(41.28, 8.14) * mm, "end": v(41.17, 7.75) * mm});
            skLineSegment(sketch, "E378", {"start": v(41.17, 7.75) * mm, "end": v(41.14, 7.33) * mm});
            skLineSegment(sketch, "E379", {"start": v(41.14, 7.33) * mm, "end": v(41.17, 6.9) * mm});
            skLineSegment(sketch, "E380", {"start": v(24.98, 6.9) * mm, "end": v(25.09, 6.51) * mm});
            skLineSegment(sketch, "E381", {"start": v(25.09, 6.51) * mm, "end": v(25.26, 6.13) * mm});
            skLineSegment(sketch, "E382", {"start": v(25.26, 6.13) * mm, "end": v(25.5, 5.8) * mm});
            skLineSegment(sketch, "E383", {"start": v(25.5, 5.8) * mm, "end": v(25.8, 5.5) * mm});
            skLineSegment(sketch, "E384", {"start": v(25.8, 5.5) * mm, "end": v(26.14, 5.24) * mm});
            skLineSegment(sketch, "E385", {"start": v(26.14, 5.24) * mm, "end": v(26.53, 5.07) * mm});
            skLineSegment(sketch, "E386", {"start": v(26.53, 5.07) * mm, "end": v(26.92, 4.96) * mm});
            skLineSegment(sketch, "E387", {"start": v(26.92, 4.96) * mm, "end": v(27.34, 4.93) * mm});
            skLineSegment(sketch, "E388", {"start": v(27.34, 4.93) * mm, "end": v(27.73, 4.96) * mm});
            skLineSegment(sketch, "E389", {"start": v(27.73, 4.96) * mm, "end": v(28.16, 5.07) * mm});
            skLineSegment(sketch, "E390", {"start": v(28.16, 5.07) * mm, "end": v(28.54, 5.24) * mm});
            skLineSegment(sketch, "E391", {"start": v(28.54, 5.24) * mm, "end": v(28.86, 5.5) * mm});
            skLineSegment(sketch, "E392", {"start": v(28.86, 5.5) * mm, "end": v(29.18, 5.8) * mm});
            skLineSegment(sketch, "E393", {"start": v(29.18, 5.8) * mm, "end": v(29.4, 6.13) * mm});
            skLineSegment(sketch, "E394", {"start": v(29.4, 6.13) * mm, "end": v(29.57, 6.51) * mm});
            skLineSegment(sketch, "E395", {"start": v(29.57, 6.51) * mm, "end": v(29.67, 6.9) * mm});
            skLineSegment(sketch, "E396", {"start": v(29.67, 6.9) * mm, "end": v(29.7, 7.33) * mm});
            skLineSegment(sketch, "E397", {"start": v(29.7, 7.33) * mm, "end": v(29.67, 7.75) * mm});
            skLineSegment(sketch, "E398", {"start": v(29.67, 7.75) * mm, "end": v(29.57, 8.14) * mm});
            skLineSegment(sketch, "E399", {"start": v(29.57, 8.14) * mm, "end": v(29.4, 8.53) * mm});
            skLineSegment(sketch, "E400", {"start": v(29.4, 8.53) * mm, "end": v(29.18, 8.88) * mm});
            skLineSegment(sketch, "E401", {"start": v(29.18, 8.88) * mm, "end": v(28.86, 9.16) * mm});
            skLineSegment(sketch, "E402", {"start": v(28.86, 9.16) * mm, "end": v(28.54, 9.4) * mm});
            skLineSegment(sketch, "E403", {"start": v(28.54, 9.4) * mm, "end": v(28.16, 9.58) * mm});
            skLineSegment(sketch, "E404", {"start": v(28.16, 9.58) * mm, "end": v(27.73, 9.69) * mm});
            skLineSegment(sketch, "E405", {"start": v(27.73, 9.69) * mm, "end": v(27.34, 9.73) * mm});
            skLineSegment(sketch, "E406", {"start": v(27.34, 9.73) * mm, "end": v(26.92, 9.69) * mm});
            skLineSegment(sketch, "E407", {"start": v(26.92, 9.69) * mm, "end": v(26.53, 9.58) * mm});
            skLineSegment(sketch, "E408", {"start": v(26.53, 9.58) * mm, "end": v(26.14, 9.4) * mm});
            skLineSegment(sketch, "E409", {"start": v(26.14, 9.4) * mm, "end": v(25.8, 9.16) * mm});
            skLineSegment(sketch, "E410", {"start": v(25.8, 9.16) * mm, "end": v(25.5, 8.88) * mm});
            skLineSegment(sketch, "E411", {"start": v(25.5, 8.88) * mm, "end": v(25.26, 8.53) * mm});
            skLineSegment(sketch, "E412", {"start": v(25.26, 8.53) * mm, "end": v(25.09, 8.14) * mm});
            skLineSegment(sketch, "E413", {"start": v(25.09, 8.14) * mm, "end": v(24.98, 7.75) * mm});
            skLineSegment(sketch, "E414", {"start": v(24.98, 7.75) * mm, "end": v(24.95, 7.33) * mm});
            skLineSegment(sketch, "E415", {"start": v(24.95, 7.33) * mm, "end": v(24.98, 6.9) * mm});
            skLineSegment(sketch, "E416", {"start": v(72.6, 48.85) * mm, "end": v(72.46, 49.13) * mm});
            skLineSegment(sketch, "E417", {"start": v(72.46, 49.13) * mm, "end": v(72.29, 49.38) * mm});
            skLineSegment(sketch, "E418", {"start": v(72.29, 49.38) * mm, "end": v(72.08, 49.59) * mm});
            skLineSegment(sketch, "E419", {"start": v(72.08, 49.59) * mm, "end": v(71.8, 49.73) * mm});
            skLineSegment(sketch, "E420", {"start": v(71.8, 49.73) * mm, "end": v(71.48, 49.8) * mm});
            skLineSegment(sketch, "E421", {"start": v(71.48, 49.8) * mm, "end": v(71.16, 49.8) * mm});
            skLineSegment(sketch, "E422", {"start": v(71.16, 49.8) * mm, "end": v(70.88, 49.73) * mm});
            skLineSegment(sketch, "E423", {"start": v(70.88, 49.73) * mm, "end": v(70.6, 49.59) * mm});
            skLineSegment(sketch, "E424", {"start": v(70.6, 49.59) * mm, "end": v(70.35, 49.38) * mm});
            skLineSegment(sketch, "E425", {"start": v(70.35, 49.38) * mm, "end": v(70.17, 49.13) * mm});
            skLineSegment(sketch, "E426", {"start": v(70.17, 49.13) * mm, "end": v(70.07, 48.85) * mm});
            skLineSegment(sketch, "E427", {"start": v(70.07, 48.85) * mm, "end": v(70.03, 48.53) * mm});
            skLineSegment(sketch, "E428", {"start": v(70.03, 48.53) * mm, "end": v(70.03, 30.64) * mm});
            skLineSegment(sketch, "E429", {"start": v(70.03, 30.64) * mm, "end": v(70.07, 30.33) * mm});
            skLineSegment(sketch, "E430", {"start": v(70.07, 30.33) * mm, "end": v(70.17, 30.05) * mm});
            skLineSegment(sketch, "E431", {"start": v(70.17, 30.05) * mm, "end": v(70.35, 29.8) * mm});
            skLineSegment(sketch, "E432", {"start": v(70.35, 29.8) * mm, "end": v(70.6, 29.59) * mm});
            skLineSegment(sketch, "E433", {"start": v(70.6, 29.59) * mm, "end": v(70.88, 29.45) * mm});
            skLineSegment(sketch, "E434", {"start": v(70.88, 29.45) * mm, "end": v(71.16, 29.34) * mm});
            skLineSegment(sketch, "E435", {"start": v(71.16, 29.34) * mm, "end": v(71.48, 29.34) * mm});
            skLineSegment(sketch, "E436", {"start": v(71.48, 29.34) * mm, "end": v(71.8, 29.45) * mm});
            skLineSegment(sketch, "E437", {"start": v(71.8, 29.45) * mm, "end": v(72.08, 29.59) * mm});
            skLineSegment(sketch, "E438", {"start": v(72.08, 29.59) * mm, "end": v(72.29, 29.8) * mm});
            skLineSegment(sketch, "E439", {"start": v(72.29, 29.8) * mm, "end": v(72.46, 30.05) * mm});
            skLineSegment(sketch, "E440", {"start": v(72.46, 30.05) * mm, "end": v(72.6, 30.33) * mm});
            skLineSegment(sketch, "E441", {"start": v(72.6, 30.33) * mm, "end": v(72.64, 30.64) * mm});
            skLineSegment(sketch, "E442", {"start": v(72.64, 30.64) * mm, "end": v(72.64, 48.53) * mm});
            skLineSegment(sketch, "E443", {"start": v(72.64, 48.53) * mm, "end": v(72.6, 48.85) * mm});
            skLineSegment(sketch, "E444", {"start": v(29.57, 64.9) * mm, "end": v(23.18, 64.9) * mm});
            skLineSegment(sketch, "E445", {"start": v(23.18, 64.9) * mm, "end": v(23.18, 61.9) * mm});
            skLineSegment(sketch, "E446", {"start": v(23.18, 61.9) * mm, "end": v(29.57, 61.9) * mm});
            skLineSegment(sketch, "E447", {"start": v(29.57, 61.9) * mm, "end": v(29.57, 64.9) * mm});
            skLineSegment(sketch, "E448", {"start": v(54.97, 64.9) * mm, "end": v(48.58, 64.9) * mm});
            skLineSegment(sketch, "E449", {"start": v(48.58, 64.9) * mm, "end": v(48.58, 61.9) * mm});
            skLineSegment(sketch, "E450", {"start": v(48.58, 61.9) * mm, "end": v(54.97, 61.9) * mm});
            skLineSegment(sketch, "E451", {"start": v(54.97, 61.9) * mm, "end": v(54.97, 64.9) * mm});
            skLineSegment(sketch, "E452", {"start": v(42.27, 16.67) * mm, "end": v(35.88, 16.67) * mm});
            skLineSegment(sketch, "E453", {"start": v(35.88, 16.67) * mm, "end": v(35.88, 13.68) * mm});
            skLineSegment(sketch, "E454", {"start": v(35.88, 13.68) * mm, "end": v(42.27, 13.68) * mm});
            skLineSegment(sketch, "E455", {"start": v(42.27, 13.68) * mm, "end": v(42.27, 16.67) * mm});
            skLineSegment(sketch, "E456", {"start": v(66.64, 30.19) * mm, "end": v(63.64, 30.19) * mm});
            skLineSegment(sketch, "E457", {"start": v(63.64, 30.19) * mm, "end": v(63.64, 23.84) * mm});
            skLineSegment(sketch, "E458", {"start": v(63.64, 23.84) * mm, "end": v(66.64, 23.84) * mm});
            skLineSegment(sketch, "E459", {"start": v(66.64, 23.84) * mm, "end": v(66.64, 30.19) * mm});
            skFitSpline(sketch, "E460", {"points": [v(19.3, 24.22) * mm, v(19.3, 23.18) * mm, v(20.16, 22.33) * mm, v(21.2, 22.33) * mm]});
            skFitSpline(sketch, "E461", {"points": [v(21.2, 22.33) * mm, v(22.25, 22.33) * mm, v(23.1, 23.18) * mm, v(23.1, 24.22) * mm]});
            skFitSpline(sketch, "E462", {"points": [v(23.1, 24.22) * mm, v(23.1, 25.27) * mm, v(22.25, 26.12) * mm, v(21.2, 26.12) * mm]});
            skFitSpline(sketch, "E463", {"points": [v(21.2, 26.12) * mm, v(20.16, 26.12) * mm, v(19.3, 25.27) * mm, v(19.3, 24.22) * mm]});
            skLineSegment(sketch, "E464", {"start": v(11.5, 23.84) * mm, "end": v(14.5, 23.84) * mm});
            skLineSegment(sketch, "E465", {"start": v(14.5, 23.84) * mm, "end": v(14.5, 30.19) * mm});
            skLineSegment(sketch, "E466", {"start": v(14.5, 30.19) * mm, "end": v(11.5, 30.19) * mm});
            skLineSegment(sketch, "E467", {"start": v(11.5, 30.19) * mm, "end": v(11.5, 23.84) * mm});
            skLineSegment(sketch, "E468", {"start": v(16.77, 19.24) * mm, "end": v(16.94, 19.79) * mm});
            skLineSegment(sketch, "E469", {"start": v(16.94, 19.79) * mm, "end": v(17.26, 20.1) * mm});
            skLineSegment(sketch, "E470", {"start": v(17.26, 18.4) * mm, "end": v(16.87, 18.8) * mm});
            skLineSegment(sketch, "E471", {"start": v(16.87, 18.8) * mm, "end": v(16.77, 19.24) * mm});
            skLineSegment(sketch, "E472", {"start": v(18.25, 18.4) * mm, "end": v(17.7, 18.26) * mm});
            skLineSegment(sketch, "E473", {"start": v(17.7, 18.26) * mm, "end": v(17.26, 18.4) * mm});
            skLineSegment(sketch, "E474", {"start": v(18.74, 19.24) * mm, "end": v(18.57, 18.7) * mm});
            skLineSegment(sketch, "E475", {"start": v(18.57, 18.7) * mm, "end": v(18.25, 18.4) * mm});
            skLineSegment(sketch, "E476", {"start": v(18.25, 20.1) * mm, "end": v(18.63, 19.68) * mm});
            skLineSegment(sketch, "E477", {"start": v(18.63, 19.68) * mm, "end": v(18.74, 19.24) * mm});
            skLineSegment(sketch, "E478", {"start": v(22.97, 55.94) * mm, "end": v(22.8, 56.26) * mm});
            skLineSegment(sketch, "E479", {"start": v(22.8, 56.26) * mm, "end": v(22.55, 56.54) * mm});
            skLineSegment(sketch, "E480", {"start": v(22.55, 56.54) * mm, "end": v(22.26, 56.79) * mm});
            skLineSegment(sketch, "E481", {"start": v(22.26, 56.79) * mm, "end": v(21.95, 56.96) * mm});
            skLineSegment(sketch, "E482", {"start": v(21.95, 56.96) * mm, "end": v(21.6, 57.07) * mm});
            skLineSegment(sketch, "E483", {"start": v(21.6, 57.07) * mm, "end": v(21.2, 57.1) * mm});
            skLineSegment(sketch, "E484", {"start": v(21.2, 57.1) * mm, "end": v(20.85, 57.07) * mm});
            skLineSegment(sketch, "E485", {"start": v(20.85, 57.07) * mm, "end": v(20.5, 56.96) * mm});
            skLineSegment(sketch, "E486", {"start": v(20.5, 56.96) * mm, "end": v(20.15, 56.79) * mm});
            skLineSegment(sketch, "E487", {"start": v(20.15, 56.79) * mm, "end": v(19.87, 56.54) * mm});
            skLineSegment(sketch, "E488", {"start": v(19.87, 56.54) * mm, "end": v(19.62, 56.26) * mm});
            skLineSegment(sketch, "E489", {"start": v(19.62, 56.26) * mm, "end": v(19.44, 55.94) * mm});
            skLineSegment(sketch, "E490", {"start": v(19.44, 55.94) * mm, "end": v(19.34, 55.55) * mm});
            skLineSegment(sketch, "E491", {"start": v(19.34, 55.55) * mm, "end": v(19.3, 55.2) * mm});
            skLineSegment(sketch, "E492", {"start": v(19.3, 55.2) * mm, "end": v(19.34, 54.81) * mm});
            skLineSegment(sketch, "E493", {"start": v(19.34, 54.81) * mm, "end": v(19.44, 54.46) * mm});
            skLineSegment(sketch, "E494", {"start": v(19.44, 54.46) * mm, "end": v(19.62, 54.14) * mm});
            skLineSegment(sketch, "E495", {"start": v(19.62, 54.14) * mm, "end": v(19.87, 53.86) * mm});
            skLineSegment(sketch, "E496", {"start": v(19.87, 53.86) * mm, "end": v(20.15, 53.61) * mm});
            skLineSegment(sketch, "E497", {"start": v(20.15, 53.61) * mm, "end": v(20.5, 53.43) * mm});
            skLineSegment(sketch, "E498", {"start": v(20.5, 53.43) * mm, "end": v(20.85, 53.33) * mm});
            skLineSegment(sketch, "E499", {"start": v(20.85, 53.33) * mm, "end": v(21.2, 53.3) * mm});
            skLineSegment(sketch, "E500", {"start": v(21.2, 53.3) * mm, "end": v(21.6, 53.33) * mm});
            skLineSegment(sketch, "E501", {"start": v(21.6, 53.33) * mm, "end": v(21.95, 53.43) * mm});
            skLineSegment(sketch, "E502", {"start": v(21.95, 53.43) * mm, "end": v(22.26, 53.61) * mm});
            skLineSegment(sketch, "E503", {"start": v(22.26, 53.61) * mm, "end": v(22.55, 53.86) * mm});
            skLineSegment(sketch, "E504", {"start": v(22.55, 53.86) * mm, "end": v(22.8, 54.14) * mm});
            skLineSegment(sketch, "E505", {"start": v(22.8, 54.14) * mm, "end": v(22.97, 54.46) * mm});
            skLineSegment(sketch, "E506", {"start": v(22.97, 54.46) * mm, "end": v(23.08, 54.81) * mm});
            skLineSegment(sketch, "E507", {"start": v(23.08, 54.81) * mm, "end": v(23.11, 55.2) * mm});
            skLineSegment(sketch, "E508", {"start": v(23.11, 55.2) * mm, "end": v(23.08, 55.55) * mm});
            skLineSegment(sketch, "E509", {"start": v(21.52, 72.66) * mm, "end": v(21.35, 73.05) * mm});
            skLineSegment(sketch, "E510", {"start": v(21.35, 73.05) * mm, "end": v(21.1, 73.37) * mm});
            skLineSegment(sketch, "E511", {"start": v(21.1, 73.37) * mm, "end": v(20.82, 73.68) * mm});
            skLineSegment(sketch, "E512", {"start": v(20.82, 73.68) * mm, "end": v(20.46, 73.9) * mm});
            skLineSegment(sketch, "E513", {"start": v(20.46, 73.9) * mm, "end": v(20.08, 74.07) * mm});
            skLineSegment(sketch, "E514", {"start": v(20.08, 74.07) * mm, "end": v(19.69, 74.21) * mm});
            skLineSegment(sketch, "E515", {"start": v(19.69, 74.21) * mm, "end": v(19.27, 74.25) * mm});
            skLineSegment(sketch, "E516", {"start": v(19.27, 74.25) * mm, "end": v(18.84, 74.21) * mm});
            skLineSegment(sketch, "E517", {"start": v(18.84, 74.21) * mm, "end": v(18.45, 74.07) * mm});
            skLineSegment(sketch, "E518", {"start": v(18.45, 74.07) * mm, "end": v(18.07, 73.9) * mm});
            skLineSegment(sketch, "E519", {"start": v(18.07, 73.9) * mm, "end": v(17.75, 73.68) * mm});
            skLineSegment(sketch, "E520", {"start": v(17.75, 73.68) * mm, "end": v(17.43, 73.37) * mm});
            skLineSegment(sketch, "E521", {"start": v(17.43, 73.37) * mm, "end": v(17.18, 73.05) * mm});
            skLineSegment(sketch, "E522", {"start": v(17.18, 73.05) * mm, "end": v(17, 72.66) * mm});
            skLineSegment(sketch, "E523", {"start": v(17, 72.66) * mm, "end": v(16.9, 72.27) * mm});
            skLineSegment(sketch, "E524", {"start": v(16.9, 72.27) * mm, "end": v(16.87, 71.85) * mm});
            skLineSegment(sketch, "E525", {"start": v(16.87, 71.85) * mm, "end": v(16.9, 71.43) * mm});
            skLineSegment(sketch, "E526", {"start": v(16.9, 71.43) * mm, "end": v(17, 71.04) * mm});
            skLineSegment(sketch, "E527", {"start": v(17, 71.04) * mm, "end": v(17.18, 70.65) * mm});
            skLineSegment(sketch, "E528", {"start": v(17.18, 70.65) * mm, "end": v(17.43, 70.3) * mm});
            skLineSegment(sketch, "E529", {"start": v(17.43, 70.3) * mm, "end": v(17.75, 70.01) * mm});
            skLineSegment(sketch, "E530", {"start": v(17.75, 70.01) * mm, "end": v(18.07, 69.77) * mm});
            skLineSegment(sketch, "E531", {"start": v(18.07, 69.77) * mm, "end": v(18.45, 69.6) * mm});
            skLineSegment(sketch, "E532", {"start": v(18.45, 69.6) * mm, "end": v(18.84, 69.49) * mm});
            skLineSegment(sketch, "E533", {"start": v(18.84, 69.49) * mm, "end": v(19.27, 69.45) * mm});
            skLineSegment(sketch, "E534", {"start": v(19.27, 69.45) * mm, "end": v(19.69, 69.49) * mm});
            skLineSegment(sketch, "E535", {"start": v(19.69, 69.49) * mm, "end": v(20.08, 69.6) * mm});
            skLineSegment(sketch, "E536", {"start": v(20.08, 69.6) * mm, "end": v(20.46, 69.77) * mm});
            skLineSegment(sketch, "E537", {"start": v(20.46, 69.77) * mm, "end": v(20.82, 70.01) * mm});
            skLineSegment(sketch, "E538", {"start": v(20.82, 70.01) * mm, "end": v(21.1, 70.3) * mm});
            skLineSegment(sketch, "E539", {"start": v(21.1, 70.3) * mm, "end": v(21.35, 70.65) * mm});
            skLineSegment(sketch, "E540", {"start": v(21.35, 70.65) * mm, "end": v(21.52, 71.04) * mm});
            skLineSegment(sketch, "E541", {"start": v(21.52, 71.04) * mm, "end": v(21.63, 71.43) * mm});
            skLineSegment(sketch, "E542", {"start": v(21.63, 71.43) * mm, "end": v(21.66, 71.85) * mm});
            skLineSegment(sketch, "E543", {"start": v(21.66, 71.85) * mm, "end": v(21.63, 72.27) * mm});
            skLineSegment(sketch, "E544", {"start": v(29.57, 72.66) * mm, "end": v(29.4, 73.05) * mm});
            skLineSegment(sketch, "E545", {"start": v(29.4, 73.05) * mm, "end": v(29.18, 73.37) * mm});
            skLineSegment(sketch, "E546", {"start": v(29.18, 73.37) * mm, "end": v(28.86, 73.68) * mm});
            skLineSegment(sketch, "E547", {"start": v(28.86, 73.68) * mm, "end": v(28.54, 73.9) * mm});
            skLineSegment(sketch, "E548", {"start": v(28.54, 73.9) * mm, "end": v(28.16, 74.07) * mm});
            skLineSegment(sketch, "E549", {"start": v(28.16, 74.07) * mm, "end": v(27.73, 74.21) * mm});
            skLineSegment(sketch, "E550", {"start": v(27.73, 74.21) * mm, "end": v(27.34, 74.25) * mm});
            skLineSegment(sketch, "E551", {"start": v(27.34, 74.25) * mm, "end": v(26.92, 74.21) * mm});
            skLineSegment(sketch, "E552", {"start": v(26.92, 74.21) * mm, "end": v(26.53, 74.07) * mm});
            skLineSegment(sketch, "E553", {"start": v(26.53, 74.07) * mm, "end": v(26.14, 73.9) * mm});
            skLineSegment(sketch, "E554", {"start": v(26.14, 73.9) * mm, "end": v(25.8, 73.68) * mm});
            skLineSegment(sketch, "E555", {"start": v(25.8, 73.68) * mm, "end": v(25.5, 73.37) * mm});
            skLineSegment(sketch, "E556", {"start": v(25.5, 73.37) * mm, "end": v(25.26, 73.05) * mm});
            skLineSegment(sketch, "E557", {"start": v(25.26, 73.05) * mm, "end": v(25.09, 72.66) * mm});
            skLineSegment(sketch, "E558", {"start": v(25.09, 72.66) * mm, "end": v(24.98, 72.27) * mm});
            skLineSegment(sketch, "E559", {"start": v(24.98, 72.27) * mm, "end": v(24.95, 71.85) * mm});
            skLineSegment(sketch, "E560", {"start": v(24.95, 71.85) * mm, "end": v(24.98, 71.43) * mm});
            skLineSegment(sketch, "E561", {"start": v(24.98, 71.43) * mm, "end": v(25.09, 71.04) * mm});
            skLineSegment(sketch, "E562", {"start": v(25.09, 71.04) * mm, "end": v(25.26, 70.65) * mm});
            skLineSegment(sketch, "E563", {"start": v(25.26, 70.65) * mm, "end": v(25.5, 70.3) * mm});
            skLineSegment(sketch, "E564", {"start": v(25.5, 70.3) * mm, "end": v(25.8, 70.01) * mm});
            skLineSegment(sketch, "E565", {"start": v(25.8, 70.01) * mm, "end": v(26.14, 69.77) * mm});
            skLineSegment(sketch, "E566", {"start": v(26.14, 69.77) * mm, "end": v(26.53, 69.6) * mm});
            skLineSegment(sketch, "E567", {"start": v(26.53, 69.6) * mm, "end": v(26.92, 69.49) * mm});
            skLineSegment(sketch, "E568", {"start": v(26.92, 69.49) * mm, "end": v(27.34, 69.45) * mm});
            skLineSegment(sketch, "E569", {"start": v(27.34, 69.45) * mm, "end": v(27.73, 69.49) * mm});
            skLineSegment(sketch, "E570", {"start": v(27.73, 69.49) * mm, "end": v(28.16, 69.6) * mm});
            skLineSegment(sketch, "E571", {"start": v(28.16, 69.6) * mm, "end": v(28.54, 69.77) * mm});
            skLineSegment(sketch, "E572", {"start": v(28.54, 69.77) * mm, "end": v(28.86, 70.01) * mm});
            skLineSegment(sketch, "E573", {"start": v(28.86, 70.01) * mm, "end": v(29.18, 70.3) * mm});
            skLineSegment(sketch, "E574", {"start": v(29.18, 70.3) * mm, "end": v(29.4, 70.65) * mm});
            skLineSegment(sketch, "E575", {"start": v(29.4, 70.65) * mm, "end": v(29.57, 71.04) * mm});
            skLineSegment(sketch, "E576", {"start": v(29.57, 71.04) * mm, "end": v(29.67, 71.43) * mm});
            skLineSegment(sketch, "E577", {"start": v(29.67, 71.43) * mm, "end": v(29.7, 71.85) * mm});
            skLineSegment(sketch, "E578", {"start": v(29.7, 71.85) * mm, "end": v(29.67, 72.27) * mm});
            skLineSegment(sketch, "E579", {"start": v(66.64, 36.54) * mm, "end": v(66.64, 42.89) * mm});
            skLineSegment(sketch, "E580", {"start": v(66.64, 42.89) * mm, "end": v(63.64, 42.89) * mm});
            skLineSegment(sketch, "E581", {"start": v(63.64, 42.89) * mm, "end": v(63.64, 36.54) * mm});
            skLineSegment(sketch, "E582", {"start": v(45.76, 72.66) * mm, "end": v(45.58, 73.05) * mm});
            skLineSegment(sketch, "E583", {"start": v(45.58, 73.05) * mm, "end": v(45.37, 73.37) * mm});
            skLineSegment(sketch, "E584", {"start": v(45.37, 73.37) * mm, "end": v(45.05, 73.68) * mm});
            skLineSegment(sketch, "E585", {"start": v(45.05, 73.68) * mm, "end": v(44.74, 73.9) * mm});
            skLineSegment(sketch, "E586", {"start": v(44.74, 73.9) * mm, "end": v(44.35, 74.07) * mm});
            skLineSegment(sketch, "E587", {"start": v(44.35, 74.07) * mm, "end": v(43.92, 74.21) * mm});
            skLineSegment(sketch, "E588", {"start": v(43.92, 74.21) * mm, "end": v(43.54, 74.25) * mm});
            skLineSegment(sketch, "E589", {"start": v(43.54, 74.25) * mm, "end": v(43.11, 74.21) * mm});
            skLineSegment(sketch, "E590", {"start": v(43.11, 74.21) * mm, "end": v(42.73, 74.07) * mm});
            skLineSegment(sketch, "E591", {"start": v(42.73, 74.07) * mm, "end": v(42.34, 73.9) * mm});
            skLineSegment(sketch, "E592", {"start": v(42.34, 73.9) * mm, "end": v(41.98, 73.68) * mm});
            skLineSegment(sketch, "E593", {"start": v(41.98, 73.68) * mm, "end": v(41.7, 73.37) * mm});
            skLineSegment(sketch, "E594", {"start": v(41.7, 73.37) * mm, "end": v(41.46, 73.05) * mm});
            skLineSegment(sketch, "E595", {"start": v(41.46, 73.05) * mm, "end": v(41.28, 72.66) * mm});
            skLineSegment(sketch, "E596", {"start": v(41.28, 72.66) * mm, "end": v(41.17, 72.27) * mm});
            skLineSegment(sketch, "E597", {"start": v(41.17, 72.27) * mm, "end": v(41.14, 71.85) * mm});
            skLineSegment(sketch, "E598", {"start": v(41.14, 71.85) * mm, "end": v(41.17, 71.43) * mm});
            skLineSegment(sketch, "E599", {"start": v(41.17, 71.43) * mm, "end": v(41.28, 71.04) * mm});
            skLineSegment(sketch, "E600", {"start": v(41.28, 71.04) * mm, "end": v(41.46, 70.65) * mm});
            skLineSegment(sketch, "E601", {"start": v(41.46, 70.65) * mm, "end": v(41.7, 70.3) * mm});
            skLineSegment(sketch, "E602", {"start": v(41.7, 70.3) * mm, "end": v(41.98, 70.01) * mm});
            skLineSegment(sketch, "E603", {"start": v(41.98, 70.01) * mm, "end": v(42.34, 69.77) * mm});
            skLineSegment(sketch, "E604", {"start": v(42.34, 69.77) * mm, "end": v(42.73, 69.6) * mm});
            skLineSegment(sketch, "E605", {"start": v(42.73, 69.6) * mm, "end": v(43.11, 69.49) * mm});
            skLineSegment(sketch, "E606", {"start": v(43.11, 69.49) * mm, "end": v(43.54, 69.45) * mm});
            skLineSegment(sketch, "E607", {"start": v(43.54, 69.45) * mm, "end": v(43.92, 69.49) * mm});
            skLineSegment(sketch, "E608", {"start": v(43.92, 69.49) * mm, "end": v(44.35, 69.6) * mm});
            skLineSegment(sketch, "E609", {"start": v(44.35, 69.6) * mm, "end": v(44.74, 69.77) * mm});
            skLineSegment(sketch, "E610", {"start": v(44.74, 69.77) * mm, "end": v(45.05, 70.01) * mm});
            skLineSegment(sketch, "E611", {"start": v(45.05, 70.01) * mm, "end": v(45.37, 70.3) * mm});
            skLineSegment(sketch, "E612", {"start": v(45.37, 70.3) * mm, "end": v(45.58, 70.65) * mm});
            skLineSegment(sketch, "E613", {"start": v(45.58, 70.65) * mm, "end": v(45.76, 71.04) * mm});
            skLineSegment(sketch, "E614", {"start": v(45.76, 71.04) * mm, "end": v(45.86, 71.43) * mm});
            skLineSegment(sketch, "E615", {"start": v(45.86, 71.43) * mm, "end": v(45.9, 71.85) * mm});
            skLineSegment(sketch, "E616", {"start": v(45.9, 71.85) * mm, "end": v(45.86, 72.27) * mm});
            skLineSegment(sketch, "E617", {"start": v(61.92, 72.66) * mm, "end": v(61.74, 73.05) * mm});
            skLineSegment(sketch, "E618", {"start": v(61.74, 73.05) * mm, "end": v(61.5, 73.37) * mm});
            skLineSegment(sketch, "E619", {"start": v(61.5, 73.37) * mm, "end": v(61.18, 73.68) * mm});
            skLineSegment(sketch, "E620", {"start": v(61.18, 73.68) * mm, "end": v(60.86, 73.9) * mm});
            skLineSegment(sketch, "E621", {"start": v(60.86, 73.9) * mm, "end": v(60.47, 74.07) * mm});
            skLineSegment(sketch, "E622", {"start": v(60.47, 74.07) * mm, "end": v(60.08, 74.21) * mm});
            skLineSegment(sketch, "E623", {"start": v(60.08, 74.21) * mm, "end": v(59.66, 74.25) * mm});
            skLineSegment(sketch, "E624", {"start": v(59.66, 74.25) * mm, "end": v(59.24, 74.21) * mm});
            skLineSegment(sketch, "E625", {"start": v(59.24, 74.21) * mm, "end": v(58.85, 74.07) * mm});
            skLineSegment(sketch, "E626", {"start": v(58.85, 74.07) * mm, "end": v(58.46, 73.9) * mm});
            skLineSegment(sketch, "E627", {"start": v(58.46, 73.9) * mm, "end": v(58.1, 73.68) * mm});
            skLineSegment(sketch, "E628", {"start": v(58.1, 73.68) * mm, "end": v(57.82, 73.37) * mm});
            skLineSegment(sketch, "E629", {"start": v(57.82, 73.37) * mm, "end": v(57.58, 73.05) * mm});
            skLineSegment(sketch, "E630", {"start": v(57.58, 73.05) * mm, "end": v(57.4, 72.66) * mm});
            skLineSegment(sketch, "E631", {"start": v(57.4, 72.66) * mm, "end": v(57.3, 72.27) * mm});
            skLineSegment(sketch, "E632", {"start": v(57.3, 72.27) * mm, "end": v(57.26, 71.85) * mm});
            skLineSegment(sketch, "E633", {"start": v(57.26, 71.85) * mm, "end": v(57.3, 71.43) * mm});
            skLineSegment(sketch, "E634", {"start": v(57.3, 71.43) * mm, "end": v(57.4, 71.04) * mm});
            skLineSegment(sketch, "E635", {"start": v(57.4, 71.04) * mm, "end": v(57.58, 70.65) * mm});
            skLineSegment(sketch, "E636", {"start": v(57.58, 70.65) * mm, "end": v(57.82, 70.3) * mm});
            skLineSegment(sketch, "E637", {"start": v(57.82, 70.3) * mm, "end": v(58.1, 70.01) * mm});
            skLineSegment(sketch, "E638", {"start": v(58.1, 70.01) * mm, "end": v(58.46, 69.77) * mm});
            skLineSegment(sketch, "E639", {"start": v(58.46, 69.77) * mm, "end": v(58.85, 69.6) * mm});
            skLineSegment(sketch, "E640", {"start": v(58.85, 69.6) * mm, "end": v(59.24, 69.49) * mm});
            skLineSegment(sketch, "E641", {"start": v(59.24, 69.49) * mm, "end": v(59.66, 69.45) * mm});
            skLineSegment(sketch, "E642", {"start": v(59.66, 69.45) * mm, "end": v(60.08, 69.49) * mm});
            skLineSegment(sketch, "E643", {"start": v(60.08, 69.49) * mm, "end": v(60.47, 69.6) * mm});
            skLineSegment(sketch, "E644", {"start": v(60.47, 69.6) * mm, "end": v(60.86, 69.77) * mm});
            skLineSegment(sketch, "E645", {"start": v(60.86, 69.77) * mm, "end": v(61.18, 70.01) * mm});
            skLineSegment(sketch, "E646", {"start": v(61.18, 70.01) * mm, "end": v(61.5, 70.3) * mm});
            skLineSegment(sketch, "E647", {"start": v(61.5, 70.3) * mm, "end": v(61.74, 70.65) * mm});
            skLineSegment(sketch, "E648", {"start": v(61.74, 70.65) * mm, "end": v(61.92, 71.04) * mm});
            skLineSegment(sketch, "E649", {"start": v(61.92, 71.04) * mm, "end": v(62.02, 71.43) * mm});
            skLineSegment(sketch, "E650", {"start": v(62.02, 71.43) * mm, "end": v(62.06, 71.85) * mm});
            skLineSegment(sketch, "E651", {"start": v(62.06, 71.85) * mm, "end": v(62.02, 72.27) * mm});
            skLineSegment(sketch, "E652", {"start": v(49.36, 6.51) * mm, "end": v(49.53, 6.13) * mm});
            skLineSegment(sketch, "E653", {"start": v(49.53, 6.13) * mm, "end": v(49.75, 5.8) * mm});
            skLineSegment(sketch, "E654", {"start": v(49.75, 5.8) * mm, "end": v(50.06, 5.5) * mm});
            skLineSegment(sketch, "E655", {"start": v(50.06, 5.5) * mm, "end": v(50.38, 5.24) * mm});
            skLineSegment(sketch, "E656", {"start": v(50.38, 5.24) * mm, "end": v(50.77, 5.07) * mm});
            skLineSegment(sketch, "E657", {"start": v(50.77, 5.07) * mm, "end": v(51.2, 4.96) * mm});
            skLineSegment(sketch, "E658", {"start": v(51.2, 4.96) * mm, "end": v(51.58, 4.93) * mm});
            skLineSegment(sketch, "E659", {"start": v(51.58, 4.93) * mm, "end": v(52, 4.96) * mm});
            skLineSegment(sketch, "E660", {"start": v(52, 4.96) * mm, "end": v(52.43, 5.07) * mm});
            skLineSegment(sketch, "E661", {"start": v(52.43, 5.07) * mm, "end": v(52.78, 5.24) * mm});
            skLineSegment(sketch, "E662", {"start": v(52.78, 5.24) * mm, "end": v(53.13, 5.5) * mm});
            skLineSegment(sketch, "E663", {"start": v(53.13, 5.5) * mm, "end": v(53.41, 5.8) * mm});
            skLineSegment(sketch, "E664", {"start": v(53.41, 5.8) * mm, "end": v(53.66, 6.13) * mm});
            skLineSegment(sketch, "E665", {"start": v(53.66, 6.13) * mm, "end": v(53.84, 6.51) * mm});
            skLineSegment(sketch, "E666", {"start": v(53.84, 6.51) * mm, "end": v(53.94, 6.9) * mm});
            skLineSegment(sketch, "E667", {"start": v(53.94, 6.9) * mm, "end": v(53.98, 7.33) * mm});
            skLineSegment(sketch, "E668", {"start": v(53.98, 7.33) * mm, "end": v(53.94, 7.75) * mm});
            skLineSegment(sketch, "E669", {"start": v(53.94, 7.75) * mm, "end": v(53.84, 8.14) * mm});
            skLineSegment(sketch, "E670", {"start": v(53.84, 8.14) * mm, "end": v(53.66, 8.53) * mm});
            skLineSegment(sketch, "E671", {"start": v(53.66, 8.53) * mm, "end": v(53.41, 8.88) * mm});
            skLineSegment(sketch, "E672", {"start": v(53.41, 8.88) * mm, "end": v(53.13, 9.16) * mm});
            skLineSegment(sketch, "E673", {"start": v(53.13, 9.16) * mm, "end": v(52.78, 9.4) * mm});
            skLineSegment(sketch, "E674", {"start": v(52.78, 9.4) * mm, "end": v(52.43, 9.58) * mm});
            skLineSegment(sketch, "E675", {"start": v(52.43, 9.58) * mm, "end": v(52, 9.69) * mm});
            skLineSegment(sketch, "E676", {"start": v(52, 9.69) * mm, "end": v(51.58, 9.73) * mm});
            skLineSegment(sketch, "E677", {"start": v(51.58, 9.73) * mm, "end": v(51.2, 9.69) * mm});
            skLineSegment(sketch, "E678", {"start": v(51.2, 9.69) * mm, "end": v(50.77, 9.58) * mm});
            skLineSegment(sketch, "E679", {"start": v(50.77, 9.58) * mm, "end": v(50.38, 9.4) * mm});
            skLineSegment(sketch, "E680", {"start": v(50.38, 9.4) * mm, "end": v(50.06, 9.16) * mm});
            skLineSegment(sketch, "E681", {"start": v(50.06, 9.16) * mm, "end": v(49.75, 8.88) * mm});
            skLineSegment(sketch, "E682", {"start": v(49.75, 8.88) * mm, "end": v(49.53, 8.53) * mm});
            skLineSegment(sketch, "E683", {"start": v(49.53, 8.53) * mm, "end": v(49.36, 8.14) * mm});
            skLineSegment(sketch, "E684", {"start": v(49.36, 8.14) * mm, "end": v(49.25, 7.75) * mm});
            skLineSegment(sketch, "E685", {"start": v(49.25, 7.75) * mm, "end": v(49.22, 7.33) * mm});
            skLineSegment(sketch, "E686", {"start": v(49.22, 7.33) * mm, "end": v(49.25, 6.9) * mm});
            skLineSegment(sketch, "E687", {"start": v(33.16, 6.51) * mm, "end": v(33.34, 6.13) * mm});
            skLineSegment(sketch, "E688", {"start": v(33.34, 6.13) * mm, "end": v(33.55, 5.8) * mm});
            skLineSegment(sketch, "E689", {"start": v(33.55, 5.8) * mm, "end": v(33.87, 5.5) * mm});
            skLineSegment(sketch, "E690", {"start": v(33.87, 5.5) * mm, "end": v(34.19, 5.24) * mm});
            skLineSegment(sketch, "E691", {"start": v(34.19, 5.24) * mm, "end": v(34.58, 5.07) * mm});
            skLineSegment(sketch, "E692", {"start": v(34.58, 5.07) * mm, "end": v(35, 4.96) * mm});
            skLineSegment(sketch, "E693", {"start": v(35, 4.96) * mm, "end": v(35.39, 4.93) * mm});
            skLineSegment(sketch, "E694", {"start": v(35.39, 4.93) * mm, "end": v(35.81, 4.96) * mm});
            skLineSegment(sketch, "E695", {"start": v(35.81, 4.96) * mm, "end": v(36.2, 5.07) * mm});
            skLineSegment(sketch, "E696", {"start": v(36.2, 5.07) * mm, "end": v(36.59, 5.24) * mm});
            skLineSegment(sketch, "E697", {"start": v(36.59, 5.24) * mm, "end": v(36.94, 5.5) * mm});
            skLineSegment(sketch, "E698", {"start": v(36.94, 5.5) * mm, "end": v(37.22, 5.8) * mm});
            skLineSegment(sketch, "E699", {"start": v(37.22, 5.8) * mm, "end": v(37.47, 6.13) * mm});
            skLineSegment(sketch, "E700", {"start": v(37.47, 6.13) * mm, "end": v(37.65, 6.51) * mm});
            skLineSegment(sketch, "E701", {"start": v(37.65, 6.51) * mm, "end": v(37.75, 6.9) * mm});
            skLineSegment(sketch, "E702", {"start": v(37.75, 6.9) * mm, "end": v(37.79, 7.33) * mm});
            skLineSegment(sketch, "E703", {"start": v(37.79, 7.33) * mm, "end": v(37.75, 7.75) * mm});
            skLineSegment(sketch, "E704", {"start": v(37.75, 7.75) * mm, "end": v(37.65, 8.14) * mm});
            skLineSegment(sketch, "E705", {"start": v(37.65, 8.14) * mm, "end": v(37.47, 8.53) * mm});
            skLineSegment(sketch, "E706", {"start": v(37.47, 8.53) * mm, "end": v(37.22, 8.88) * mm});
            skLineSegment(sketch, "E707", {"start": v(37.22, 8.88) * mm, "end": v(36.94, 9.16) * mm});
            skLineSegment(sketch, "E708", {"start": v(36.94, 9.16) * mm, "end": v(36.59, 9.4) * mm});
            skLineSegment(sketch, "E709", {"start": v(36.59, 9.4) * mm, "end": v(36.2, 9.58) * mm});
            skLineSegment(sketch, "E710", {"start": v(36.2, 9.58) * mm, "end": v(35.81, 9.69) * mm});
            skLineSegment(sketch, "E711", {"start": v(35.81, 9.69) * mm, "end": v(35.39, 9.73) * mm});
            skLineSegment(sketch, "E712", {"start": v(35.39, 9.73) * mm, "end": v(35, 9.69) * mm});
            skLineSegment(sketch, "E713", {"start": v(35, 9.69) * mm, "end": v(34.58, 9.58) * mm});
            skLineSegment(sketch, "E714", {"start": v(34.58, 9.58) * mm, "end": v(34.19, 9.4) * mm});
            skLineSegment(sketch, "E715", {"start": v(34.19, 9.4) * mm, "end": v(33.87, 9.16) * mm});
            skLineSegment(sketch, "E716", {"start": v(33.87, 9.16) * mm, "end": v(33.55, 8.88) * mm});
            skLineSegment(sketch, "E717", {"start": v(33.55, 8.88) * mm, "end": v(33.34, 8.53) * mm});
            skLineSegment(sketch, "E718", {"start": v(33.34, 8.53) * mm, "end": v(33.16, 8.14) * mm});
            skLineSegment(sketch, "E719", {"start": v(33.16, 8.14) * mm, "end": v(33.06, 7.75) * mm});
            skLineSegment(sketch, "E720", {"start": v(33.06, 7.75) * mm, "end": v(33.02, 7.33) * mm});
            skLineSegment(sketch, "E721", {"start": v(33.02, 7.33) * mm, "end": v(33.06, 6.9) * mm});
            skLineSegment(sketch, "E722", {"start": v(18.45, 9.58) * mm, "end": v(18.07, 9.4) * mm});
            skLineSegment(sketch, "E723", {"start": v(18.07, 9.4) * mm, "end": v(17.75, 9.16) * mm});
            skLineSegment(sketch, "E724", {"start": v(17.75, 9.16) * mm, "end": v(17.43, 8.88) * mm});
            skLineSegment(sketch, "E725", {"start": v(17.43, 8.88) * mm, "end": v(17.18, 8.53) * mm});
            skLineSegment(sketch, "E726", {"start": v(17.18, 8.53) * mm, "end": v(17, 8.14) * mm});
            skLineSegment(sketch, "E727", {"start": v(17, 8.14) * mm, "end": v(16.9, 7.75) * mm});
            skLineSegment(sketch, "E728", {"start": v(16.9, 7.75) * mm, "end": v(16.87, 7.33) * mm});
            skLineSegment(sketch, "E729", {"start": v(16.87, 7.33) * mm, "end": v(16.9, 6.9) * mm});
            skLineSegment(sketch, "E730", {"start": v(8.19, 49.13) * mm, "end": v(8.01, 49.38) * mm});
            skLineSegment(sketch, "E731", {"start": v(8.01, 49.38) * mm, "end": v(7.8, 49.59) * mm});
            skLineSegment(sketch, "E732", {"start": v(7.8, 49.59) * mm, "end": v(7.52, 49.73) * mm});
            skLineSegment(sketch, "E733", {"start": v(7.52, 49.73) * mm, "end": v(7.2, 49.8) * mm});
            skLineSegment(sketch, "E734", {"start": v(7.2, 49.8) * mm, "end": v(6.88, 49.8) * mm});
            skLineSegment(sketch, "E735", {"start": v(6.88, 49.8) * mm, "end": v(6.57, 49.73) * mm});
            skLineSegment(sketch, "E736", {"start": v(6.57, 49.73) * mm, "end": v(6.32, 49.59) * mm});
            skLineSegment(sketch, "E737", {"start": v(6.32, 49.59) * mm, "end": v(6.07, 49.38) * mm});
            skLineSegment(sketch, "E738", {"start": v(35.99, 64.9) * mm, "end": v(35.99, 61.9) * mm});
            skLineSegment(sketch, "E739", {"start": v(35.99, 61.9) * mm, "end": v(42.27, 61.9) * mm});
            skLineSegment(sketch, "E740", {"start": v(42.27, 61.9) * mm, "end": v(42.27, 64.9) * mm});
            skLineSegment(sketch, "E741", {"start": v(23.29, 16.67) * mm, "end": v(23.29, 13.68) * mm});
            skLineSegment(sketch, "E742", {"start": v(23.29, 13.68) * mm, "end": v(29.57, 13.68) * mm});
            skLineSegment(sketch, "E743", {"start": v(29.57, 13.68) * mm, "end": v(29.57, 16.67) * mm});
            skLineSegment(sketch, "E744", {"start": v(48.58, 16.67) * mm, "end": v(48.58, 13.68) * mm});
            skLineSegment(sketch, "E745", {"start": v(48.58, 13.68) * mm, "end": v(54.97, 13.68) * mm});
            skLineSegment(sketch, "E746", {"start": v(54.97, 13.68) * mm, "end": v(54.97, 16.67) * mm});
            skLineSegment(sketch, "E747", {"start": v(14.5, 49.24) * mm, "end": v(14.5, 55.59) * mm});
            skLineSegment(sketch, "E748", {"start": v(14.5, 55.59) * mm, "end": v(11.5, 55.59) * mm});
            skLineSegment(sketch, "E749", {"start": v(11.5, 55.59) * mm, "end": v(11.5, 49.24) * mm});
            skLineSegment(sketch, "E750", {"start": v(11.5, 42.89) * mm, "end": v(11.5, 36.54) * mm});
            skLineSegment(sketch, "E751", {"start": v(11.5, 36.54) * mm, "end": v(14.5, 36.54) * mm});
            skLineSegment(sketch, "E752", {"start": v(14.5, 36.54) * mm, "end": v(14.5, 42.89) * mm});
            skLineSegment(sketch, "E753", {"start": v(14.5, 42.89) * mm, "end": v(11.5, 42.89) * mm});
            skLineSegment(sketch, "E754", {"start": v(11.5, 49.24) * mm, "end": v(14.5, 49.24) * mm});
            skLineSegment(sketch, "E755", {"start": v(54.97, 16.67) * mm, "end": v(48.58, 16.67) * mm});
            skLineSegment(sketch, "E756", {"start": v(29.57, 16.67) * mm, "end": v(23.29, 16.67) * mm});
            skLineSegment(sketch, "E757", {"start": v(42.27, 64.9) * mm, "end": v(35.99, 64.9) * mm});
            skLineSegment(sketch, "E758", {"start": v(8.3, 48.85) * mm, "end": v(8.19, 49.13) * mm});
            skLineSegment(sketch, "E759", {"start": v(16.9, 6.9) * mm, "end": v(17, 6.51) * mm});
            skLineSegment(sketch, "E760", {"start": v(33.06, 6.9) * mm, "end": v(33.16, 6.51) * mm});
            skLineSegment(sketch, "E761", {"start": v(49.25, 6.9) * mm, "end": v(49.36, 6.51) * mm});
            skLineSegment(sketch, "E762", {"start": v(62.02, 72.27) * mm, "end": v(61.92, 72.66) * mm});
            skLineSegment(sketch, "E763", {"start": v(45.86, 72.27) * mm, "end": v(45.76, 72.66) * mm});
            skLineSegment(sketch, "E764", {"start": v(63.64, 36.54) * mm, "end": v(66.64, 36.54) * mm});
            skLineSegment(sketch, "E765", {"start": v(29.67, 72.27) * mm, "end": v(29.57, 72.66) * mm});
            skLineSegment(sketch, "E766", {"start": v(21.63, 72.27) * mm, "end": v(21.52, 72.66) * mm});
            skLineSegment(sketch, "E767", {"start": v(23.08, 55.55) * mm, "end": v(22.97, 55.94) * mm});
            skLineSegment(sketch, "E768", {"start": v(17.26, 20.1) * mm, "end": v(17.82, 20.22) * mm});
            skLineSegment(sketch, "E769", {"start": v(17.82, 20.22) * mm, "end": v(18.25, 20.1) * mm});
            skLineSegment(sketch, "E770", {"start": v(8.19, 30.05) * mm, "end": v(8.3, 30.33) * mm});
            skLineSegment(sketch, "E771", {"start": v(8.3, 30.33) * mm, "end": v(8.36, 30.64) * mm});
            skLineSegment(sketch, "E772", {"start": v(8.36, 30.64) * mm, "end": v(8.36, 48.53) * mm});
            skLineSegment(sketch, "E773", {"start": v(8.36, 48.53) * mm, "end": v(8.3, 48.85) * mm});
            skLineSegment(sketch, "E774", {"start": v(17, 6.51) * mm, "end": v(17.18, 6.13) * mm});
            skLineSegment(sketch, "E775", {"start": v(17.18, 6.13) * mm, "end": v(17.43, 5.8) * mm});
            skLineSegment(sketch, "E776", {"start": v(17.43, 5.8) * mm, "end": v(17.75, 5.5) * mm});
            skLineSegment(sketch, "E777", {"start": v(17.75, 5.5) * mm, "end": v(18.07, 5.24) * mm});
            skLineSegment(sketch, "E778", {"start": v(18.07, 5.24) * mm, "end": v(18.45, 5.07) * mm});
            skLineSegment(sketch, "E779", {"start": v(18.45, 5.07) * mm, "end": v(18.84, 4.96) * mm});
            skLineSegment(sketch, "E780", {"start": v(18.84, 4.96) * mm, "end": v(19.27, 4.93) * mm});
            skLineSegment(sketch, "E781", {"start": v(19.27, 4.93) * mm, "end": v(19.69, 4.96) * mm});
            skLineSegment(sketch, "E782", {"start": v(19.69, 4.96) * mm, "end": v(20.08, 5.07) * mm});
            skLineSegment(sketch, "E783", {"start": v(20.08, 5.07) * mm, "end": v(20.46, 5.24) * mm});
            skLineSegment(sketch, "E784", {"start": v(20.46, 5.24) * mm, "end": v(20.82, 5.5) * mm});
            skLineSegment(sketch, "E785", {"start": v(20.82, 5.5) * mm, "end": v(21.1, 5.8) * mm});
            skLineSegment(sketch, "E786", {"start": v(21.1, 5.8) * mm, "end": v(21.35, 6.13) * mm});
            skLineSegment(sketch, "E787", {"start": v(21.35, 6.13) * mm, "end": v(21.52, 6.51) * mm});
            skLineSegment(sketch, "E788", {"start": v(21.52, 6.51) * mm, "end": v(21.63, 6.9) * mm});
            skLineSegment(sketch, "E789", {"start": v(21.63, 6.9) * mm, "end": v(21.66, 7.33) * mm});
            skLineSegment(sketch, "E790", {"start": v(21.66, 7.33) * mm, "end": v(21.63, 7.75) * mm});
            skLineSegment(sketch, "E791", {"start": v(21.63, 7.75) * mm, "end": v(21.52, 8.14) * mm});
            skLineSegment(sketch, "E792", {"start": v(21.52, 8.14) * mm, "end": v(21.35, 8.53) * mm});
            skLineSegment(sketch, "E793", {"start": v(21.35, 8.53) * mm, "end": v(21.1, 8.88) * mm});
            skLineSegment(sketch, "E794", {"start": v(21.1, 8.88) * mm, "end": v(20.82, 9.16) * mm});
            skLineSegment(sketch, "E795", {"start": v(20.82, 9.16) * mm, "end": v(20.46, 9.4) * mm});
            skLineSegment(sketch, "E796", {"start": v(20.46, 9.4) * mm, "end": v(20.08, 9.58) * mm});
            skLineSegment(sketch, "E797", {"start": v(20.08, 9.58) * mm, "end": v(19.69, 9.69) * mm});
            skLineSegment(sketch, "E798", {"start": v(19.69, 9.69) * mm, "end": v(19.27, 9.73) * mm});
            skLineSegment(sketch, "E799", {"start": v(19.27, 9.73) * mm, "end": v(18.84, 9.69) * mm});
            skLineSegment(sketch, "E800", {"start": v(18.84, 9.69) * mm, "end": v(18.45, 9.58) * mm});
            skLineSegment(sketch, "E801", {"start": v(6.07, 29.8) * mm, "end": v(6.32, 29.59) * mm});
            skLineSegment(sketch, "E802", {"start": v(6.32, 29.59) * mm, "end": v(6.57, 29.45) * mm});
            skLineSegment(sketch, "E803", {"start": v(6.57, 29.45) * mm, "end": v(6.88, 29.34) * mm});
            skLineSegment(sketch, "E804", {"start": v(6.88, 29.34) * mm, "end": v(7.2, 29.34) * mm});
            skLineSegment(sketch, "E805", {"start": v(7.2, 29.34) * mm, "end": v(7.52, 29.45) * mm});
            skLineSegment(sketch, "E806", {"start": v(7.52, 29.45) * mm, "end": v(7.8, 29.59) * mm});
            skLineSegment(sketch, "E807", {"start": v(6.07, 49.38) * mm, "end": v(5.9, 49.13) * mm});
            skLineSegment(sketch, "E808", {"start": v(5.9, 49.13) * mm, "end": v(5.79, 48.85) * mm});
            skLineSegment(sketch, "E809", {"start": v(5.79, 48.85) * mm, "end": v(5.75, 48.53) * mm});
            skLineSegment(sketch, "E810", {"start": v(5.75, 48.53) * mm, "end": v(5.75, 30.64) * mm});
            skLineSegment(sketch, "E811", {"start": v(5.75, 30.64) * mm, "end": v(5.79, 30.33) * mm});
            skLineSegment(sketch, "E812", {"start": v(5.79, 30.33) * mm, "end": v(5.9, 30.05) * mm});
            skLineSegment(sketch, "E813", {"start": v(5.9, 30.05) * mm, "end": v(6.07, 29.8) * mm});
            skLineSegment(sketch, "E814", {"start": v(7.8, 29.59) * mm, "end": v(8.01, 29.8) * mm});
            skLineSegment(sketch, "E815", {"start": v(8.01, 29.8) * mm, "end": v(8.19, 30.05) * mm});
            skLineSegment(sketch, "E816", {"start": v(-67.14, 2.98) * mm, "end": v(-66.71, 2.88) * mm});
            skLineSegment(sketch, "E817", {"start": v(-18.74, 23.9) * mm, "end": v(-18.84, 24.25) * mm});
            skLineSegment(sketch, "E818", {"start": v(-11.75, 54.91) * mm, "end": v(-14.75, 54.91) * mm});
            skLineSegment(sketch, "E819", {"start": v(-40.64, 71.6) * mm, "end": v(-40.75, 71.99) * mm});
            skLineSegment(sketch, "E820", {"start": v(-24.45, 71.6) * mm, "end": v(-24.56, 71.99) * mm});
            skLineSegment(sketch, "E821", {"start": v(-21.1, 6.23) * mm, "end": v(-21, 5.84) * mm});
            skLineSegment(sketch, "E822", {"start": v(-37.22, 6.23) * mm, "end": v(-37.12, 5.84) * mm});
            skLineSegment(sketch, "E823", {"start": v(-53.41, 6.23) * mm, "end": v(-53.3, 5.84) * mm});
            skLineSegment(sketch, "E824", {"start": v(-5.79, 48.17) * mm, "end": v(-5.9, 48.46) * mm});
            skLineSegment(sketch, "E825", {"start": v(-48.83, 64.22) * mm, "end": v(-55.21, 64.22) * mm});
            skLineSegment(sketch, "E826", {"start": v(-23.43, 64.22) * mm, "end": v(-29.81, 64.22) * mm});
            skLineSegment(sketch, "E827", {"start": v(-36.13, 16) * mm, "end": v(-42.51, 16) * mm});
            skLineSegment(sketch, "E828", {"start": v(-42.51, 16) * mm, "end": v(-42.51, 13) * mm});
            skLineSegment(sketch, "E829", {"start": v(-11.75, 29.51) * mm, "end": v(-14.75, 29.51) * mm});
            skLineSegment(sketch, "E830", {"start": v(-14.75, 29.51) * mm, "end": v(-14.75, 23.16) * mm});
            skLineSegment(sketch, "E831", {"start": v(-14.75, 23.16) * mm, "end": v(-11.75, 23.16) * mm});
            skLineSegment(sketch, "E832", {"start": v(-11.75, 23.16) * mm, "end": v(-11.75, 29.51) * mm});
            skFitSpline(sketch, "E833", {"points": [v(-59.08, 23.55) * mm, v(-59.08, 22.5) * mm, v(-58.24, 21.65) * mm, v(-57.19, 21.65) * mm]});
            skFitSpline(sketch, "E834", {"points": [v(-57.19, 21.65) * mm, v(-56.14, 21.65) * mm, v(-55.3, 22.5) * mm, v(-55.3, 23.55) * mm]});
            skFitSpline(sketch, "E835", {"points": [v(-55.3, 23.55) * mm, v(-55.3, 24.6) * mm, v(-56.14, 25.45) * mm, v(-57.19, 25.45) * mm]});
            skFitSpline(sketch, "E836", {"points": [v(-57.19, 25.45) * mm, v(-58.24, 25.45) * mm, v(-59.08, 24.6) * mm, v(-59.08, 23.55) * mm]});
            skLineSegment(sketch, "E837", {"start": v(-66.9, 23.16) * mm, "end": v(-63.9, 23.16) * mm});
            skLineSegment(sketch, "E838", {"start": v(-63.9, 23.16) * mm, "end": v(-63.9, 29.51) * mm});
            skLineSegment(sketch, "E839", {"start": v(-63.9, 29.51) * mm, "end": v(-66.9, 29.51) * mm});
            skLineSegment(sketch, "E840", {"start": v(-66.9, 29.51) * mm, "end": v(-66.9, 23.16) * mm});
            skFitSpline(sketch, "E841", {"points": [v(-24.54, 28.08) * mm, v(-24.54, 28.96) * mm, v(-25.25, 29.67) * mm, v(-26.12, 29.67) * mm]});
            skLineSegment(sketch, "E842", {"start": v(-24.54, 28.08) * mm, "end": v(-24.54, 21.87) * mm});
            skFitSpline(sketch, "E843", {"points": [v(-39.21, 29.67) * mm, v(-40.09, 29.67) * mm, v(-40.8, 28.96) * mm, v(-40.8, 28.08) * mm]});
            skLineSegment(sketch, "E844", {"start": v(-26.12, 29.67) * mm, "end": v(-39.21, 29.67) * mm});
            skFitSpline(sketch, "E845", {"points": [v(-40.8, 21.87) * mm, v(-40.8, 21) * mm, v(-40.09, 20.28) * mm, v(-39.21, 20.28) * mm]});
            skLineSegment(sketch, "E846", {"start": v(-40.8, 28.08) * mm, "end": v(-40.8, 21.87) * mm});
            skFitSpline(sketch, "E847", {"points": [v(-26.12, 20.28) * mm, v(-25.25, 20.28) * mm, v(-24.54, 21) * mm, v(-24.54, 21.87) * mm]});
            skLineSegment(sketch, "E848", {"start": v(-26.12, 20.28) * mm, "end": v(-39.21, 20.28) * mm});
            skLineSegment(sketch, "E849", {"start": v(-61.18, 19.42) * mm, "end": v(-60.62, 19.55) * mm});
            skLineSegment(sketch, "E850", {"start": v(-60.62, 19.55) * mm, "end": v(-60.2, 19.42) * mm});
            skLineSegment(sketch, "E851", {"start": v(-61.67, 18.57) * mm, "end": v(-61.5, 19.11) * mm});
            skLineSegment(sketch, "E852", {"start": v(-61.5, 19.11) * mm, "end": v(-61.18, 19.42) * mm});
            skLineSegment(sketch, "E853", {"start": v(-61.18, 17.72) * mm, "end": v(-61.56, 18.13) * mm});
            skLineSegment(sketch, "E854", {"start": v(-61.56, 18.13) * mm, "end": v(-61.67, 18.57) * mm});
            skLineSegment(sketch, "E855", {"start": v(-60.2, 17.72) * mm, "end": v(-60.74, 17.59) * mm});
            skLineSegment(sketch, "E856", {"start": v(-60.74, 17.59) * mm, "end": v(-61.18, 17.72) * mm});
            skLineSegment(sketch, "E857", {"start": v(-59.7, 18.57) * mm, "end": v(-59.86, 18.02) * mm});
            skLineSegment(sketch, "E858", {"start": v(-59.86, 18.02) * mm, "end": v(-60.2, 17.72) * mm});
            skLineSegment(sketch, "E859", {"start": v(-60.2, 19.42) * mm, "end": v(-59.8, 19) * mm});
            skLineSegment(sketch, "E860", {"start": v(-59.8, 19) * mm, "end": v(-59.7, 18.57) * mm});
            skLineSegment(sketch, "E861", {"start": v(-55.32, 54.88) * mm, "end": v(-55.43, 55.26) * mm});
            skLineSegment(sketch, "E862", {"start": v(-59.02, 54.88) * mm, "end": v(-59.06, 54.52) * mm});
            skLineSegment(sketch, "E863", {"start": v(-59.06, 54.52) * mm, "end": v(-59.02, 54.14) * mm});
            skLineSegment(sketch, "E864", {"start": v(-59.02, 54.14) * mm, "end": v(-58.92, 53.78) * mm});
            skLineSegment(sketch, "E865", {"start": v(-58.92, 53.78) * mm, "end": v(-58.74, 53.46) * mm});
            skLineSegment(sketch, "E866", {"start": v(-58.74, 53.46) * mm, "end": v(-58.53, 53.18) * mm});
            skLineSegment(sketch, "E867", {"start": v(-58.53, 53.18) * mm, "end": v(-58.25, 52.94) * mm});
            skLineSegment(sketch, "E868", {"start": v(-58.25, 52.94) * mm, "end": v(-57.9, 52.76) * mm});
            skLineSegment(sketch, "E869", {"start": v(-57.9, 52.76) * mm, "end": v(-57.54, 52.65) * mm});
            skLineSegment(sketch, "E870", {"start": v(-57.54, 52.65) * mm, "end": v(-57.19, 52.62) * mm});
            skLineSegment(sketch, "E871", {"start": v(-57.19, 52.62) * mm, "end": v(-56.8, 52.65) * mm});
            skLineSegment(sketch, "E872", {"start": v(-56.8, 52.65) * mm, "end": v(-56.45, 52.76) * mm});
            skLineSegment(sketch, "E873", {"start": v(-56.45, 52.76) * mm, "end": v(-56.13, 52.94) * mm});
            skLineSegment(sketch, "E874", {"start": v(-56.13, 52.94) * mm, "end": v(-55.85, 53.18) * mm});
            skLineSegment(sketch, "E875", {"start": v(-55.85, 53.18) * mm, "end": v(-55.6, 53.46) * mm});
            skLineSegment(sketch, "E876", {"start": v(-55.6, 53.46) * mm, "end": v(-55.43, 53.78) * mm});
            skLineSegment(sketch, "E877", {"start": v(-55.43, 53.78) * mm, "end": v(-55.32, 54.14) * mm});
            skLineSegment(sketch, "E878", {"start": v(-55.32, 54.14) * mm, "end": v(-55.28, 54.52) * mm});
            skLineSegment(sketch, "E879", {"start": v(-55.28, 54.52) * mm, "end": v(-55.32, 54.88) * mm});
            skLineSegment(sketch, "E880", {"start": v(-56.77, 71.6) * mm, "end": v(-56.87, 71.99) * mm});
            skLineSegment(sketch, "E881", {"start": v(-56.87, 71.99) * mm, "end": v(-57.05, 72.37) * mm});
            skLineSegment(sketch, "E882", {"start": v(-57.05, 72.37) * mm, "end": v(-57.3, 72.7) * mm});
            skLineSegment(sketch, "E883", {"start": v(-57.3, 72.7) * mm, "end": v(-57.58, 73) * mm});
            skLineSegment(sketch, "E884", {"start": v(-57.58, 73) * mm, "end": v(-57.93, 73.22) * mm});
            skLineSegment(sketch, "E885", {"start": v(-57.93, 73.22) * mm, "end": v(-58.32, 73.4) * mm});
            skLineSegment(sketch, "E886", {"start": v(-48.69, 71.6) * mm, "end": v(-48.8, 71.99) * mm});
            skLineSegment(sketch, "E887", {"start": v(-49.53, 73) * mm, "end": v(-49.85, 73.22) * mm});
            skLineSegment(sketch, "E888", {"start": v(-49.85, 73.22) * mm, "end": v(-50.24, 73.4) * mm});
            skLineSegment(sketch, "E889", {"start": v(-50.24, 73.4) * mm, "end": v(-50.63, 73.54) * mm});
            skLineSegment(sketch, "E890", {"start": v(-50.63, 73.54) * mm, "end": v(-51.05, 73.57) * mm});
            skLineSegment(sketch, "E891", {"start": v(-51.05, 73.57) * mm, "end": v(-51.47, 73.54) * mm});
            skLineSegment(sketch, "E892", {"start": v(-51.47, 73.54) * mm, "end": v(-51.86, 73.4) * mm});
            skLineSegment(sketch, "E893", {"start": v(-51.86, 73.4) * mm, "end": v(-52.25, 73.22) * mm});
            skLineSegment(sketch, "E894", {"start": v(-52.25, 73.22) * mm, "end": v(-52.6, 73) * mm});
            skLineSegment(sketch, "E895", {"start": v(-52.6, 73) * mm, "end": v(-52.89, 72.7) * mm});
            skLineSegment(sketch, "E896", {"start": v(-52.89, 72.7) * mm, "end": v(-53.13, 72.37) * mm});
            skLineSegment(sketch, "E897", {"start": v(-53.13, 72.37) * mm, "end": v(-53.3, 71.99) * mm});
            skLineSegment(sketch, "E898", {"start": v(-53.3, 71.99) * mm, "end": v(-53.41, 71.6) * mm});
            skLineSegment(sketch, "E899", {"start": v(-53.41, 71.6) * mm, "end": v(-53.45, 71.17) * mm});
            skLineSegment(sketch, "E900", {"start": v(-53.45, 71.17) * mm, "end": v(-53.41, 70.75) * mm});
            skLineSegment(sketch, "E901", {"start": v(-53.41, 70.75) * mm, "end": v(-53.3, 70.36) * mm});
            skLineSegment(sketch, "E902", {"start": v(-53.3, 70.36) * mm, "end": v(-53.13, 69.97) * mm});
            skLineSegment(sketch, "E903", {"start": v(-53.13, 69.97) * mm, "end": v(-52.89, 69.62) * mm});
            skLineSegment(sketch, "E904", {"start": v(-52.89, 69.62) * mm, "end": v(-52.6, 69.34) * mm});
            skLineSegment(sketch, "E905", {"start": v(-52.6, 69.34) * mm, "end": v(-52.25, 69.1) * mm});
            skLineSegment(sketch, "E906", {"start": v(-52.25, 69.1) * mm, "end": v(-51.86, 68.92) * mm});
            skLineSegment(sketch, "E907", {"start": v(-51.86, 68.92) * mm, "end": v(-51.47, 68.81) * mm});
            skLineSegment(sketch, "E908", {"start": v(-51.47, 68.81) * mm, "end": v(-51.05, 68.78) * mm});
            skLineSegment(sketch, "E909", {"start": v(-51.05, 68.78) * mm, "end": v(-50.63, 68.81) * mm});
            skLineSegment(sketch, "E910", {"start": v(-50.63, 68.81) * mm, "end": v(-50.24, 68.92) * mm});
            skLineSegment(sketch, "E911", {"start": v(-50.24, 68.92) * mm, "end": v(-49.85, 69.1) * mm});
            skLineSegment(sketch, "E912", {"start": v(-49.85, 69.1) * mm, "end": v(-49.53, 69.34) * mm});
            skLineSegment(sketch, "E913", {"start": v(-49.53, 69.34) * mm, "end": v(-49.22, 69.62) * mm});
            skLineSegment(sketch, "E914", {"start": v(-49.22, 69.62) * mm, "end": v(-48.97, 69.97) * mm});
            skLineSegment(sketch, "E915", {"start": v(-48.97, 69.97) * mm, "end": v(-48.8, 70.36) * mm});
            skLineSegment(sketch, "E916", {"start": v(-48.8, 70.36) * mm, "end": v(-48.69, 70.75) * mm});
            skLineSegment(sketch, "E917", {"start": v(-48.69, 70.75) * mm, "end": v(-48.65, 71.17) * mm});
            skLineSegment(sketch, "E918", {"start": v(-48.65, 71.17) * mm, "end": v(-48.69, 71.6) * mm});
            skLineSegment(sketch, "E919", {"start": v(-14.75, 35.86) * mm, "end": v(-11.75, 35.86) * mm});
            skLineSegment(sketch, "E920", {"start": v(-32.5, 71.6) * mm, "end": v(-32.6, 71.99) * mm});
            skLineSegment(sketch, "E921", {"start": v(-16.37, 71.6) * mm, "end": v(-16.48, 71.99) * mm});
            skLineSegment(sketch, "E922", {"start": v(-16.48, 71.99) * mm, "end": v(-16.65, 72.37) * mm});
            skLineSegment(sketch, "E923", {"start": v(-16.65, 72.37) * mm, "end": v(-16.9, 72.7) * mm});
            skLineSegment(sketch, "E924", {"start": v(-16.9, 72.7) * mm, "end": v(-17.18, 73) * mm});
            skLineSegment(sketch, "E925", {"start": v(-17.18, 73) * mm, "end": v(-17.54, 73.22) * mm});
            skLineSegment(sketch, "E926", {"start": v(-17.54, 73.22) * mm, "end": v(-17.92, 73.4) * mm});
            skLineSegment(sketch, "E927", {"start": v(-17.92, 73.4) * mm, "end": v(-18.31, 73.54) * mm});
            skLineSegment(sketch, "E928", {"start": v(-18.31, 73.54) * mm, "end": v(-18.74, 73.57) * mm});
            skLineSegment(sketch, "E929", {"start": v(-18.74, 73.57) * mm, "end": v(-19.16, 73.54) * mm});
            skLineSegment(sketch, "E930", {"start": v(-19.16, 73.54) * mm, "end": v(-19.55, 73.4) * mm});
            skLineSegment(sketch, "E931", {"start": v(-19.55, 73.4) * mm, "end": v(-19.94, 73.22) * mm});
            skLineSegment(sketch, "E932", {"start": v(-19.94, 73.22) * mm, "end": v(-20.25, 73) * mm});
            skLineSegment(sketch, "E933", {"start": v(-20.25, 73) * mm, "end": v(-20.57, 72.7) * mm});
            skLineSegment(sketch, "E934", {"start": v(-20.57, 72.7) * mm, "end": v(-20.82, 72.37) * mm});
            skLineSegment(sketch, "E935", {"start": v(-20.82, 72.37) * mm, "end": v(-21, 71.99) * mm});
            skLineSegment(sketch, "E936", {"start": v(-21, 71.99) * mm, "end": v(-21.1, 71.6) * mm});
            skLineSegment(sketch, "E937", {"start": v(-21.1, 71.6) * mm, "end": v(-21.14, 71.17) * mm});
            skLineSegment(sketch, "E938", {"start": v(-21.14, 71.17) * mm, "end": v(-21.1, 70.75) * mm});
            skLineSegment(sketch, "E939", {"start": v(-21.1, 70.75) * mm, "end": v(-21, 70.36) * mm});
            skLineSegment(sketch, "E940", {"start": v(-21, 70.36) * mm, "end": v(-20.82, 69.97) * mm});
            skLineSegment(sketch, "E941", {"start": v(-20.82, 69.97) * mm, "end": v(-20.57, 69.62) * mm});
            skLineSegment(sketch, "E942", {"start": v(-20.57, 69.62) * mm, "end": v(-20.25, 69.34) * mm});
            skLineSegment(sketch, "E943", {"start": v(-20.25, 69.34) * mm, "end": v(-19.94, 69.1) * mm});
            skLineSegment(sketch, "E944", {"start": v(-19.94, 69.1) * mm, "end": v(-19.55, 68.92) * mm});
            skLineSegment(sketch, "E945", {"start": v(-19.55, 68.92) * mm, "end": v(-19.16, 68.81) * mm});
            skLineSegment(sketch, "E946", {"start": v(-19.16, 68.81) * mm, "end": v(-18.74, 68.78) * mm});
            skLineSegment(sketch, "E947", {"start": v(-18.74, 68.78) * mm, "end": v(-18.31, 68.81) * mm});
            skLineSegment(sketch, "E948", {"start": v(-18.31, 68.81) * mm, "end": v(-17.92, 68.92) * mm});
            skLineSegment(sketch, "E949", {"start": v(-17.92, 68.92) * mm, "end": v(-17.54, 69.1) * mm});
            skLineSegment(sketch, "E950", {"start": v(-29.14, 6.23) * mm, "end": v(-29.04, 5.84) * mm});
            skLineSegment(sketch, "E951", {"start": v(-29.04, 5.84) * mm, "end": v(-28.86, 5.45) * mm});
            skLineSegment(sketch, "E952", {"start": v(-28.86, 5.45) * mm, "end": v(-28.61, 5.13) * mm});
            skLineSegment(sketch, "E953", {"start": v(-28.61, 5.13) * mm, "end": v(-28.33, 4.82) * mm});
            skLineSegment(sketch, "E954", {"start": v(-28.33, 4.82) * mm, "end": v(-27.98, 4.57) * mm});
            skLineSegment(sketch, "E955", {"start": v(-27.98, 4.57) * mm, "end": v(-27.63, 4.4) * mm});
            skLineSegment(sketch, "E956", {"start": v(-27.63, 4.4) * mm, "end": v(-27.2, 4.29) * mm});
            skLineSegment(sketch, "E957", {"start": v(-27.2, 4.29) * mm, "end": v(-26.78, 4.25) * mm});
            skLineSegment(sketch, "E958", {"start": v(-26.78, 4.25) * mm, "end": v(-26.4, 4.29) * mm});
            skLineSegment(sketch, "E959", {"start": v(-26.4, 4.29) * mm, "end": v(-25.97, 4.4) * mm});
            skLineSegment(sketch, "E960", {"start": v(-25.97, 4.4) * mm, "end": v(-25.62, 4.57) * mm});
            skLineSegment(sketch, "E961", {"start": v(-25.62, 4.57) * mm, "end": v(-25.26, 4.82) * mm});
            skLineSegment(sketch, "E962", {"start": v(-25.26, 4.82) * mm, "end": v(-24.98, 5.13) * mm});
            skLineSegment(sketch, "E963", {"start": v(-24.98, 5.13) * mm, "end": v(-24.73, 5.45) * mm});
            skLineSegment(sketch, "E964", {"start": v(-24.73, 5.45) * mm, "end": v(-24.56, 5.84) * mm});
            skLineSegment(sketch, "E965", {"start": v(-24.56, 5.84) * mm, "end": v(-24.45, 6.23) * mm});
            skLineSegment(sketch, "E966", {"start": v(-24.45, 6.23) * mm, "end": v(-24.42, 6.65) * mm});
            skLineSegment(sketch, "E967", {"start": v(-24.42, 6.65) * mm, "end": v(-24.45, 7.07) * mm});
            skLineSegment(sketch, "E968", {"start": v(-24.45, 7.07) * mm, "end": v(-24.56, 7.46) * mm});
            skLineSegment(sketch, "E969", {"start": v(-24.56, 7.46) * mm, "end": v(-24.73, 7.85) * mm});
            skLineSegment(sketch, "E970", {"start": v(-24.73, 7.85) * mm, "end": v(-24.98, 8.2) * mm});
            skLineSegment(sketch, "E971", {"start": v(-24.98, 8.2) * mm, "end": v(-25.26, 8.49) * mm});
            skLineSegment(sketch, "E972", {"start": v(-25.26, 8.49) * mm, "end": v(-25.62, 8.73) * mm});
            skLineSegment(sketch, "E973", {"start": v(-25.62, 8.73) * mm, "end": v(-25.97, 8.9) * mm});
            skLineSegment(sketch, "E974", {"start": v(-25.97, 8.9) * mm, "end": v(-26.4, 9.01) * mm});
            skLineSegment(sketch, "E975", {"start": v(-26.4, 9.01) * mm, "end": v(-26.78, 9.05) * mm});
            skLineSegment(sketch, "E976", {"start": v(-26.78, 9.05) * mm, "end": v(-27.2, 9.01) * mm});
            skLineSegment(sketch, "E977", {"start": v(-27.2, 9.01) * mm, "end": v(-27.63, 8.9) * mm});
            skLineSegment(sketch, "E978", {"start": v(-27.63, 8.9) * mm, "end": v(-27.98, 8.73) * mm});
            skLineSegment(sketch, "E979", {"start": v(-27.98, 8.73) * mm, "end": v(-28.33, 8.49) * mm});
            skLineSegment(sketch, "E980", {"start": v(-28.33, 8.49) * mm, "end": v(-28.61, 8.2) * mm});
            skLineSegment(sketch, "E981", {"start": v(-28.61, 8.2) * mm, "end": v(-28.86, 7.85) * mm});
            skLineSegment(sketch, "E982", {"start": v(-28.86, 7.85) * mm, "end": v(-29.04, 7.46) * mm});
            skLineSegment(sketch, "E983", {"start": v(-29.04, 7.46) * mm, "end": v(-29.14, 7.07) * mm});
            skLineSegment(sketch, "E984", {"start": v(-29.14, 7.07) * mm, "end": v(-29.18, 6.65) * mm});
            skLineSegment(sketch, "E985", {"start": v(-29.18, 6.65) * mm, "end": v(-29.14, 6.23) * mm});
            skLineSegment(sketch, "E986", {"start": v(-45.34, 6.23) * mm, "end": v(-45.23, 5.84) * mm});
            skLineSegment(sketch, "E987", {"start": v(-45.23, 5.84) * mm, "end": v(-45.05, 5.45) * mm});
            skLineSegment(sketch, "E988", {"start": v(-45.05, 5.45) * mm, "end": v(-44.8, 5.13) * mm});
            skLineSegment(sketch, "E989", {"start": v(-44.8, 5.13) * mm, "end": v(-44.52, 4.82) * mm});
            skLineSegment(sketch, "E990", {"start": v(-44.52, 4.82) * mm, "end": v(-44.17, 4.57) * mm});
            skLineSegment(sketch, "E991", {"start": v(-44.17, 4.57) * mm, "end": v(-43.82, 4.4) * mm});
            skLineSegment(sketch, "E992", {"start": v(-43.82, 4.4) * mm, "end": v(-43.4, 4.29) * mm});
            skLineSegment(sketch, "E993", {"start": v(-43.4, 4.29) * mm, "end": v(-42.97, 4.25) * mm});
            skLineSegment(sketch, "E994", {"start": v(-42.97, 4.25) * mm, "end": v(-42.58, 4.29) * mm});
            skLineSegment(sketch, "E995", {"start": v(-42.58, 4.29) * mm, "end": v(-42.16, 4.4) * mm});
            skLineSegment(sketch, "E996", {"start": v(-42.16, 4.4) * mm, "end": v(-41.8, 4.57) * mm});
            skLineSegment(sketch, "E997", {"start": v(-41.8, 4.57) * mm, "end": v(-41.46, 4.82) * mm});
            skLineSegment(sketch, "E998", {"start": v(-41.46, 4.82) * mm, "end": v(-41.17, 5.13) * mm});
            skLineSegment(sketch, "E999", {"start": v(-41.17, 5.13) * mm, "end": v(-40.93, 5.45) * mm});
            skLineSegment(sketch, "E1000", {"start": v(-40.93, 5.45) * mm, "end": v(-40.75, 5.84) * mm});
            skLineSegment(sketch, "E1001", {"start": v(-40.75, 5.84) * mm, "end": v(-40.64, 6.23) * mm});
            skLineSegment(sketch, "E1002", {"start": v(-40.64, 6.23) * mm, "end": v(-40.6, 6.65) * mm});
            skLineSegment(sketch, "E1003", {"start": v(-40.6, 6.65) * mm, "end": v(-40.64, 7.07) * mm});
            skLineSegment(sketch, "E1004", {"start": v(-40.64, 7.07) * mm, "end": v(-40.75, 7.46) * mm});
            skLineSegment(sketch, "E1005", {"start": v(-40.75, 7.46) * mm, "end": v(-40.93, 7.85) * mm});
            skLineSegment(sketch, "E1006", {"start": v(-40.93, 7.85) * mm, "end": v(-41.17, 8.2) * mm});
            skLineSegment(sketch, "E1007", {"start": v(-41.17, 8.2) * mm, "end": v(-41.46, 8.49) * mm});
            skLineSegment(sketch, "E1008", {"start": v(-41.46, 8.49) * mm, "end": v(-41.8, 8.73) * mm});
            skLineSegment(sketch, "E1009", {"start": v(-41.8, 8.73) * mm, "end": v(-42.16, 8.9) * mm});
            skLineSegment(sketch, "E1010", {"start": v(-42.16, 8.9) * mm, "end": v(-42.58, 9.01) * mm});
            skLineSegment(sketch, "E1011", {"start": v(-42.58, 9.01) * mm, "end": v(-42.97, 9.05) * mm});
            skLineSegment(sketch, "E1012", {"start": v(-42.97, 9.05) * mm, "end": v(-43.4, 9.01) * mm});
            skLineSegment(sketch, "E1013", {"start": v(-43.4, 9.01) * mm, "end": v(-43.82, 8.9) * mm});
            skLineSegment(sketch, "E1014", {"start": v(-43.82, 8.9) * mm, "end": v(-44.17, 8.73) * mm});
            skLineSegment(sketch, "E1015", {"start": v(-44.17, 8.73) * mm, "end": v(-44.52, 8.49) * mm});
            skLineSegment(sketch, "E1016", {"start": v(-44.52, 8.49) * mm, "end": v(-44.8, 8.2) * mm});
            skLineSegment(sketch, "E1017", {"start": v(-44.8, 8.2) * mm, "end": v(-45.05, 7.85) * mm});
            skLineSegment(sketch, "E1018", {"start": v(-45.05, 7.85) * mm, "end": v(-45.23, 7.46) * mm});
            skLineSegment(sketch, "E1019", {"start": v(-45.23, 7.46) * mm, "end": v(-45.34, 7.07) * mm});
            skLineSegment(sketch, "E1020", {"start": v(-45.34, 7.07) * mm, "end": v(-45.37, 6.65) * mm});
            skLineSegment(sketch, "E1021", {"start": v(-45.37, 6.65) * mm, "end": v(-45.34, 6.23) * mm});
            skLineSegment(sketch, "E1022", {"start": v(-61.46, 6.23) * mm, "end": v(-61.35, 5.84) * mm});
            skLineSegment(sketch, "E1023", {"start": v(-61.35, 5.84) * mm, "end": v(-61.18, 5.45) * mm});
            skLineSegment(sketch, "E1024", {"start": v(-61.18, 5.45) * mm, "end": v(-60.96, 5.13) * mm});
            skLineSegment(sketch, "E1025", {"start": v(-60.96, 5.13) * mm, "end": v(-60.65, 4.82) * mm});
            skLineSegment(sketch, "E1026", {"start": v(-60.65, 4.82) * mm, "end": v(-60.33, 4.57) * mm});
            skLineSegment(sketch, "E1027", {"start": v(-60.33, 4.57) * mm, "end": v(-59.94, 4.4) * mm});
            skLineSegment(sketch, "E1028", {"start": v(-59.94, 4.4) * mm, "end": v(-59.52, 4.29) * mm});
            skLineSegment(sketch, "E1029", {"start": v(-59.52, 4.29) * mm, "end": v(-59.13, 4.25) * mm});
            skLineSegment(sketch, "E1030", {"start": v(-59.13, 4.25) * mm, "end": v(-58.7, 4.29) * mm});
            skLineSegment(sketch, "E1031", {"start": v(-58.7, 4.29) * mm, "end": v(-58.32, 4.4) * mm});
            skLineSegment(sketch, "E1032", {"start": v(-58.32, 4.4) * mm, "end": v(-57.93, 4.57) * mm});
            skLineSegment(sketch, "E1033", {"start": v(-57.93, 4.57) * mm, "end": v(-57.58, 4.82) * mm});
            skLineSegment(sketch, "E1034", {"start": v(-57.58, 4.82) * mm, "end": v(-57.3, 5.13) * mm});
            skLineSegment(sketch, "E1035", {"start": v(-57.3, 5.13) * mm, "end": v(-57.05, 5.45) * mm});
            skLineSegment(sketch, "E1036", {"start": v(-57.05, 5.45) * mm, "end": v(-56.87, 5.84) * mm});
            skLineSegment(sketch, "E1037", {"start": v(-56.87, 5.84) * mm, "end": v(-56.77, 6.23) * mm});
            skLineSegment(sketch, "E1038", {"start": v(-56.77, 6.23) * mm, "end": v(-56.73, 6.65) * mm});
            skLineSegment(sketch, "E1039", {"start": v(-56.73, 6.65) * mm, "end": v(-56.77, 7.07) * mm});
            skLineSegment(sketch, "E1040", {"start": v(-56.77, 7.07) * mm, "end": v(-56.87, 7.46) * mm});
            skLineSegment(sketch, "E1041", {"start": v(-56.87, 7.46) * mm, "end": v(-57.05, 7.85) * mm});
            skLineSegment(sketch, "E1042", {"start": v(-57.05, 7.85) * mm, "end": v(-57.3, 8.2) * mm});
            skLineSegment(sketch, "E1043", {"start": v(-57.3, 8.2) * mm, "end": v(-57.58, 8.49) * mm});
            skLineSegment(sketch, "E1044", {"start": v(-57.58, 8.49) * mm, "end": v(-57.93, 8.73) * mm});
            skLineSegment(sketch, "E1045", {"start": v(-57.93, 8.73) * mm, "end": v(-58.32, 8.9) * mm});
            skLineSegment(sketch, "E1046", {"start": v(-58.32, 8.9) * mm, "end": v(-58.7, 9.01) * mm});
            skLineSegment(sketch, "E1047", {"start": v(-58.7, 9.01) * mm, "end": v(-59.13, 9.05) * mm});
            skLineSegment(sketch, "E1048", {"start": v(-59.13, 9.05) * mm, "end": v(-59.52, 9.01) * mm});
            skLineSegment(sketch, "E1049", {"start": v(-59.52, 9.01) * mm, "end": v(-59.94, 8.9) * mm});
            skLineSegment(sketch, "E1050", {"start": v(-59.94, 8.9) * mm, "end": v(-60.33, 8.73) * mm});
            skLineSegment(sketch, "E1051", {"start": v(-60.33, 8.73) * mm, "end": v(-60.65, 8.49) * mm});
            skLineSegment(sketch, "E1052", {"start": v(-60.65, 8.49) * mm, "end": v(-60.96, 8.2) * mm});
            skLineSegment(sketch, "E1053", {"start": v(-60.96, 8.2) * mm, "end": v(-61.18, 7.85) * mm});
            skLineSegment(sketch, "E1054", {"start": v(-61.18, 7.85) * mm, "end": v(-61.35, 7.46) * mm});
            skLineSegment(sketch, "E1055", {"start": v(-61.35, 7.46) * mm, "end": v(-61.46, 7.07) * mm});
            skLineSegment(sketch, "E1056", {"start": v(-61.46, 7.07) * mm, "end": v(-61.5, 6.65) * mm});
            skLineSegment(sketch, "E1057", {"start": v(-70.07, 48.17) * mm, "end": v(-70.17, 48.46) * mm});
            skLineSegment(sketch, "E1058", {"start": v(-70.17, 48.46) * mm, "end": v(-70.38, 48.7) * mm});
            skLineSegment(sketch, "E1059", {"start": v(-70.38, 48.7) * mm, "end": v(-70.6, 48.91) * mm});
            skLineSegment(sketch, "E1060", {"start": v(-70.6, 48.91) * mm, "end": v(-70.88, 49.05) * mm});
            skLineSegment(sketch, "E1061", {"start": v(-70.88, 49.05) * mm, "end": v(-71.2, 49.13) * mm});
            skLineSegment(sketch, "E1062", {"start": v(-71.2, 49.13) * mm, "end": v(-71.51, 49.13) * mm});
            skLineSegment(sketch, "E1063", {"start": v(-71.51, 49.13) * mm, "end": v(-71.8, 49.05) * mm});
            skLineSegment(sketch, "E1064", {"start": v(-71.8, 49.05) * mm, "end": v(-72.08, 48.91) * mm});
            skLineSegment(sketch, "E1065", {"start": v(-72.08, 48.91) * mm, "end": v(-72.32, 48.7) * mm});
            skLineSegment(sketch, "E1066", {"start": v(-72.32, 48.7) * mm, "end": v(-72.5, 48.46) * mm});
            skLineSegment(sketch, "E1067", {"start": v(-72.5, 48.46) * mm, "end": v(-72.6, 48.17) * mm});
            skLineSegment(sketch, "E1068", {"start": v(-72.6, 48.17) * mm, "end": v(-72.64, 47.86) * mm});
            skLineSegment(sketch, "E1069", {"start": v(-72.64, 47.86) * mm, "end": v(-72.64, 29.97) * mm});
            skLineSegment(sketch, "E1070", {"start": v(-72.64, 29.97) * mm, "end": v(-72.6, 29.65) * mm});
            skLineSegment(sketch, "E1071", {"start": v(-72.6, 29.65) * mm, "end": v(-72.5, 29.37) * mm});
            skLineSegment(sketch, "E1072", {"start": v(-72.5, 29.37) * mm, "end": v(-72.32, 29.12) * mm});
            skLineSegment(sketch, "E1073", {"start": v(-72.32, 29.12) * mm, "end": v(-72.08, 28.91) * mm});
            skLineSegment(sketch, "E1074", {"start": v(-72.08, 28.91) * mm, "end": v(-71.8, 28.77) * mm});
            skLineSegment(sketch, "E1075", {"start": v(-71.8, 28.77) * mm, "end": v(-71.51, 28.66) * mm});
            skLineSegment(sketch, "E1076", {"start": v(-71.51, 28.66) * mm, "end": v(-71.2, 28.66) * mm});
            skLineSegment(sketch, "E1077", {"start": v(-71.2, 28.66) * mm, "end": v(-70.88, 28.77) * mm});
            skLineSegment(sketch, "E1078", {"start": v(-70.88, 28.77) * mm, "end": v(-70.6, 28.91) * mm});
            skLineSegment(sketch, "E1079", {"start": v(-70.6, 28.91) * mm, "end": v(-70.38, 29.12) * mm});
            skLineSegment(sketch, "E1080", {"start": v(-70.38, 29.12) * mm, "end": v(-70.17, 29.37) * mm});
            skLineSegment(sketch, "E1081", {"start": v(-70.17, 29.37) * mm, "end": v(-70.07, 29.65) * mm});
            skLineSegment(sketch, "E1082", {"start": v(-70.07, 29.65) * mm, "end": v(-70.03, 29.97) * mm});
            skLineSegment(sketch, "E1083", {"start": v(-70.03, 29.97) * mm, "end": v(-70.03, 47.86) * mm});
            skLineSegment(sketch, "E1084", {"start": v(-70.03, 47.86) * mm, "end": v(-70.07, 48.17) * mm});
            skLineSegment(sketch, "E1085", {"start": v(-36.13, 64.22) * mm, "end": v(-42.4, 64.22) * mm});
            skLineSegment(sketch, "E1086", {"start": v(-42.4, 64.22) * mm, "end": v(-42.4, 61.23) * mm});
            skLineSegment(sketch, "E1087", {"start": v(-42.4, 61.23) * mm, "end": v(-36.13, 61.23) * mm});
            skLineSegment(sketch, "E1088", {"start": v(-36.13, 61.23) * mm, "end": v(-36.13, 64.22) * mm});
            skLineSegment(sketch, "E1089", {"start": v(-48.83, 16) * mm, "end": v(-55.1, 16) * mm});
            skLineSegment(sketch, "E1090", {"start": v(-55.1, 16) * mm, "end": v(-55.1, 13) * mm});
            skLineSegment(sketch, "E1091", {"start": v(-55.1, 13) * mm, "end": v(-48.83, 13) * mm});
            skLineSegment(sketch, "E1092", {"start": v(-48.83, 13) * mm, "end": v(-48.83, 16) * mm});
            skLineSegment(sketch, "E1093", {"start": v(-23.43, 16) * mm, "end": v(-29.81, 16) * mm});
            skLineSegment(sketch, "E1094", {"start": v(-29.81, 16) * mm, "end": v(-29.81, 13) * mm});
            skLineSegment(sketch, "E1095", {"start": v(-29.81, 13) * mm, "end": v(-23.43, 13) * mm});
            skLineSegment(sketch, "E1096", {"start": v(-23.43, 13) * mm, "end": v(-23.43, 16) * mm});
            skLineSegment(sketch, "E1097", {"start": v(-66.9, 48.56) * mm, "end": v(-63.9, 48.56) * mm});
            skLineSegment(sketch, "E1098", {"start": v(-63.9, 48.56) * mm, "end": v(-63.9, 54.91) * mm});
            skLineSegment(sketch, "E1099", {"start": v(-63.9, 54.91) * mm, "end": v(-66.9, 54.91) * mm});
            skLineSegment(sketch, "E1100", {"start": v(-66.9, 54.91) * mm, "end": v(-66.9, 48.56) * mm});
            skLineSegment(sketch, "E1101", {"start": v(-63.9, 42.21) * mm, "end": v(-66.9, 42.21) * mm});
            skLineSegment(sketch, "E1102", {"start": v(-66.9, 42.21) * mm, "end": v(-66.9, 35.86) * mm});
            skLineSegment(sketch, "E1103", {"start": v(-66.9, 35.86) * mm, "end": v(-63.9, 35.86) * mm});
            skLineSegment(sketch, "E1104", {"start": v(-63.9, 35.86) * mm, "end": v(-63.9, 42.21) * mm});
            skLineSegment(sketch, "E1105", {"start": v(-49.53, 4.82) * mm, "end": v(-49.22, 5.13) * mm});
            skLineSegment(sketch, "E1106", {"start": v(-49.22, 5.13) * mm, "end": v(-48.97, 5.45) * mm});
            skLineSegment(sketch, "E1107", {"start": v(-48.97, 5.45) * mm, "end": v(-48.8, 5.84) * mm});
            skLineSegment(sketch, "E1108", {"start": v(-48.8, 5.84) * mm, "end": v(-48.69, 6.23) * mm});
            skLineSegment(sketch, "E1109", {"start": v(-48.69, 6.23) * mm, "end": v(-48.65, 6.65) * mm});
            skLineSegment(sketch, "E1110", {"start": v(-48.65, 6.65) * mm, "end": v(-48.69, 7.07) * mm});
            skLineSegment(sketch, "E1111", {"start": v(-48.69, 7.07) * mm, "end": v(-48.8, 7.46) * mm});
            skLineSegment(sketch, "E1112", {"start": v(-48.8, 7.46) * mm, "end": v(-48.97, 7.85) * mm});
            skLineSegment(sketch, "E1113", {"start": v(-48.97, 7.85) * mm, "end": v(-49.22, 8.2) * mm});
            skLineSegment(sketch, "E1114", {"start": v(-49.22, 8.2) * mm, "end": v(-49.53, 8.49) * mm});
            skLineSegment(sketch, "E1115", {"start": v(-49.53, 8.49) * mm, "end": v(-49.85, 8.73) * mm});
            skLineSegment(sketch, "E1116", {"start": v(-49.85, 8.73) * mm, "end": v(-50.24, 8.9) * mm});
            skLineSegment(sketch, "E1117", {"start": v(-50.24, 8.9) * mm, "end": v(-50.63, 9.01) * mm});
            skLineSegment(sketch, "E1118", {"start": v(-50.63, 9.01) * mm, "end": v(-51.05, 9.05) * mm});
            skLineSegment(sketch, "E1119", {"start": v(-51.05, 9.05) * mm, "end": v(-51.47, 9.01) * mm});
            skLineSegment(sketch, "E1120", {"start": v(-51.47, 9.01) * mm, "end": v(-51.86, 8.9) * mm});
            skLineSegment(sketch, "E1121", {"start": v(-51.86, 8.9) * mm, "end": v(-52.25, 8.73) * mm});
            skLineSegment(sketch, "E1122", {"start": v(-52.25, 8.73) * mm, "end": v(-52.6, 8.49) * mm});
            skLineSegment(sketch, "E1123", {"start": v(-52.6, 8.49) * mm, "end": v(-52.89, 8.2) * mm});
            skLineSegment(sketch, "E1124", {"start": v(-52.89, 8.2) * mm, "end": v(-53.13, 7.85) * mm});
            skLineSegment(sketch, "E1125", {"start": v(-53.13, 7.85) * mm, "end": v(-53.3, 7.46) * mm});
            skLineSegment(sketch, "E1126", {"start": v(-53.3, 7.46) * mm, "end": v(-53.41, 7.07) * mm});
            skLineSegment(sketch, "E1127", {"start": v(-53.41, 7.07) * mm, "end": v(-53.45, 6.65) * mm});
            skLineSegment(sketch, "E1128", {"start": v(-53.45, 6.65) * mm, "end": v(-53.41, 6.23) * mm});
            skLineSegment(sketch, "E1129", {"start": v(-37.12, 5.84) * mm, "end": v(-36.94, 5.45) * mm});
            skLineSegment(sketch, "E1130", {"start": v(-36.94, 5.45) * mm, "end": v(-36.7, 5.13) * mm});
            skLineSegment(sketch, "E1131", {"start": v(-36.7, 5.13) * mm, "end": v(-36.41, 4.82) * mm});
            skLineSegment(sketch, "E1132", {"start": v(-36.41, 4.82) * mm, "end": v(-36.06, 4.57) * mm});
            skLineSegment(sketch, "E1133", {"start": v(-36.06, 4.57) * mm, "end": v(-35.67, 4.4) * mm});
            skLineSegment(sketch, "E1134", {"start": v(-35.67, 4.4) * mm, "end": v(-35.28, 4.29) * mm});
            skLineSegment(sketch, "E1135", {"start": v(-35.28, 4.29) * mm, "end": v(-34.86, 4.25) * mm});
            skLineSegment(sketch, "E1136", {"start": v(-34.86, 4.25) * mm, "end": v(-34.43, 4.29) * mm});
            skLineSegment(sketch, "E1137", {"start": v(-34.43, 4.29) * mm, "end": v(-34.05, 4.4) * mm});
            skLineSegment(sketch, "E1138", {"start": v(-34.05, 4.4) * mm, "end": v(-33.66, 4.57) * mm});
            skLineSegment(sketch, "E1139", {"start": v(-33.66, 4.57) * mm, "end": v(-33.34, 4.82) * mm});
            skLineSegment(sketch, "E1140", {"start": v(-33.34, 4.82) * mm, "end": v(-33.02, 5.13) * mm});
            skLineSegment(sketch, "E1141", {"start": v(-33.02, 5.13) * mm, "end": v(-32.78, 5.45) * mm});
            skLineSegment(sketch, "E1142", {"start": v(-32.78, 5.45) * mm, "end": v(-32.6, 5.84) * mm});
            skLineSegment(sketch, "E1143", {"start": v(-32.6, 5.84) * mm, "end": v(-32.5, 6.23) * mm});
            skLineSegment(sketch, "E1144", {"start": v(-32.5, 6.23) * mm, "end": v(-32.46, 6.65) * mm});
            skLineSegment(sketch, "E1145", {"start": v(-32.46, 6.65) * mm, "end": v(-32.5, 7.07) * mm});
            skLineSegment(sketch, "E1146", {"start": v(-32.5, 7.07) * mm, "end": v(-32.6, 7.46) * mm});
            skLineSegment(sketch, "E1147", {"start": v(-32.6, 7.46) * mm, "end": v(-32.78, 7.85) * mm});
            skLineSegment(sketch, "E1148", {"start": v(-32.78, 7.85) * mm, "end": v(-33.02, 8.2) * mm});
            skLineSegment(sketch, "E1149", {"start": v(-33.02, 8.2) * mm, "end": v(-33.34, 8.49) * mm});
            skLineSegment(sketch, "E1150", {"start": v(-33.34, 8.49) * mm, "end": v(-33.66, 8.73) * mm});
            skLineSegment(sketch, "E1151", {"start": v(-33.66, 8.73) * mm, "end": v(-34.05, 8.9) * mm});
            skLineSegment(sketch, "E1152", {"start": v(-34.05, 8.9) * mm, "end": v(-34.43, 9.01) * mm});
            skLineSegment(sketch, "E1153", {"start": v(-34.43, 9.01) * mm, "end": v(-34.86, 9.05) * mm});
            skLineSegment(sketch, "E1154", {"start": v(-34.86, 9.05) * mm, "end": v(-35.28, 9.01) * mm});
            skLineSegment(sketch, "E1155", {"start": v(-35.28, 9.01) * mm, "end": v(-35.67, 8.9) * mm});
            skLineSegment(sketch, "E1156", {"start": v(-35.67, 8.9) * mm, "end": v(-36.06, 8.73) * mm});
            skLineSegment(sketch, "E1157", {"start": v(-36.06, 8.73) * mm, "end": v(-36.41, 8.49) * mm});
            skLineSegment(sketch, "E1158", {"start": v(-36.41, 8.49) * mm, "end": v(-36.7, 8.2) * mm});
            skLineSegment(sketch, "E1159", {"start": v(-36.7, 8.2) * mm, "end": v(-36.94, 7.85) * mm});
            skLineSegment(sketch, "E1160", {"start": v(-36.94, 7.85) * mm, "end": v(-37.12, 7.46) * mm});
            skLineSegment(sketch, "E1161", {"start": v(-37.12, 7.46) * mm, "end": v(-37.22, 7.07) * mm});
            skLineSegment(sketch, "E1162", {"start": v(-37.22, 7.07) * mm, "end": v(-37.26, 6.65) * mm});
            skLineSegment(sketch, "E1163", {"start": v(-37.26, 6.65) * mm, "end": v(-37.22, 6.23) * mm});
            skLineSegment(sketch, "E1164", {"start": v(-21, 5.84) * mm, "end": v(-20.82, 5.45) * mm});
            skLineSegment(sketch, "E1165", {"start": v(-20.82, 5.45) * mm, "end": v(-20.57, 5.13) * mm});
            skLineSegment(sketch, "E1166", {"start": v(-20.57, 5.13) * mm, "end": v(-20.25, 4.82) * mm});
            skLineSegment(sketch, "E1167", {"start": v(-20.25, 4.82) * mm, "end": v(-19.94, 4.57) * mm});
            skLineSegment(sketch, "E1168", {"start": v(-19.94, 4.57) * mm, "end": v(-19.55, 4.4) * mm});
            skLineSegment(sketch, "E1169", {"start": v(-19.55, 4.4) * mm, "end": v(-19.16, 4.29) * mm});
            skLineSegment(sketch, "E1170", {"start": v(-19.16, 4.29) * mm, "end": v(-18.74, 4.25) * mm});
            skLineSegment(sketch, "E1171", {"start": v(-18.74, 4.25) * mm, "end": v(-18.31, 4.29) * mm});
            skLineSegment(sketch, "E1172", {"start": v(-18.31, 4.29) * mm, "end": v(-17.92, 4.4) * mm});
            skLineSegment(sketch, "E1173", {"start": v(-17.92, 4.4) * mm, "end": v(-17.54, 4.57) * mm});
            skLineSegment(sketch, "E1174", {"start": v(-17.54, 4.57) * mm, "end": v(-17.18, 4.82) * mm});
            skLineSegment(sketch, "E1175", {"start": v(-17.18, 4.82) * mm, "end": v(-16.9, 5.13) * mm});
            skLineSegment(sketch, "E1176", {"start": v(-16.9, 5.13) * mm, "end": v(-16.65, 5.45) * mm});
            skLineSegment(sketch, "E1177", {"start": v(-16.65, 5.45) * mm, "end": v(-16.48, 5.84) * mm});
            skLineSegment(sketch, "E1178", {"start": v(-16.48, 5.84) * mm, "end": v(-16.37, 6.23) * mm});
            skLineSegment(sketch, "E1179", {"start": v(-16.37, 6.23) * mm, "end": v(-16.34, 6.65) * mm});
            skLineSegment(sketch, "E1180", {"start": v(-16.34, 6.65) * mm, "end": v(-16.37, 7.07) * mm});
            skLineSegment(sketch, "E1181", {"start": v(-16.37, 7.07) * mm, "end": v(-16.48, 7.46) * mm});
            skLineSegment(sketch, "E1182", {"start": v(-16.48, 7.46) * mm, "end": v(-16.65, 7.85) * mm});
            skLineSegment(sketch, "E1183", {"start": v(-16.65, 7.85) * mm, "end": v(-16.9, 8.2) * mm});
            skLineSegment(sketch, "E1184", {"start": v(-16.9, 8.2) * mm, "end": v(-17.18, 8.49) * mm});
            skLineSegment(sketch, "E1185", {"start": v(-17.18, 8.49) * mm, "end": v(-17.54, 8.73) * mm});
            skLineSegment(sketch, "E1186", {"start": v(-17.54, 8.73) * mm, "end": v(-17.92, 8.9) * mm});
            skLineSegment(sketch, "E1187", {"start": v(-17.92, 8.9) * mm, "end": v(-18.31, 9.01) * mm});
            skLineSegment(sketch, "E1188", {"start": v(-18.31, 9.01) * mm, "end": v(-18.74, 9.05) * mm});
            skLineSegment(sketch, "E1189", {"start": v(-18.74, 9.05) * mm, "end": v(-19.16, 9.01) * mm});
            skLineSegment(sketch, "E1190", {"start": v(-19.16, 9.01) * mm, "end": v(-19.55, 8.9) * mm});
            skLineSegment(sketch, "E1191", {"start": v(-19.55, 8.9) * mm, "end": v(-19.94, 8.73) * mm});
            skLineSegment(sketch, "E1192", {"start": v(-19.94, 8.73) * mm, "end": v(-20.25, 8.49) * mm});
            skLineSegment(sketch, "E1193", {"start": v(-20.25, 8.49) * mm, "end": v(-20.57, 8.2) * mm});
            skLineSegment(sketch, "E1194", {"start": v(-20.57, 8.2) * mm, "end": v(-20.82, 7.85) * mm});
            skLineSegment(sketch, "E1195", {"start": v(-20.82, 7.85) * mm, "end": v(-21, 7.46) * mm});
            skLineSegment(sketch, "E1196", {"start": v(-21, 7.46) * mm, "end": v(-21.1, 7.07) * mm});
            skLineSegment(sketch, "E1197", {"start": v(-21.1, 7.07) * mm, "end": v(-21.14, 6.65) * mm});
            skLineSegment(sketch, "E1198", {"start": v(-21.14, 6.65) * mm, "end": v(-21.1, 6.23) * mm});
            skLineSegment(sketch, "E1199", {"start": v(-24.56, 71.99) * mm, "end": v(-24.73, 72.37) * mm});
            skLineSegment(sketch, "E1200", {"start": v(-24.73, 72.37) * mm, "end": v(-24.98, 72.7) * mm});
            skLineSegment(sketch, "E1201", {"start": v(-24.98, 72.7) * mm, "end": v(-25.26, 73) * mm});
            skLineSegment(sketch, "E1202", {"start": v(-25.26, 73) * mm, "end": v(-25.62, 73.22) * mm});
            skLineSegment(sketch, "E1203", {"start": v(-25.62, 73.22) * mm, "end": v(-25.97, 73.4) * mm});
            skLineSegment(sketch, "E1204", {"start": v(-25.97, 73.4) * mm, "end": v(-26.4, 73.54) * mm});
            skLineSegment(sketch, "E1205", {"start": v(-26.4, 73.54) * mm, "end": v(-26.78, 73.57) * mm});
            skLineSegment(sketch, "E1206", {"start": v(-26.78, 73.57) * mm, "end": v(-27.2, 73.54) * mm});
            skLineSegment(sketch, "E1207", {"start": v(-27.2, 73.54) * mm, "end": v(-27.63, 73.4) * mm});
            skLineSegment(sketch, "E1208", {"start": v(-27.63, 73.4) * mm, "end": v(-27.98, 73.22) * mm});
            skLineSegment(sketch, "E1209", {"start": v(-27.98, 73.22) * mm, "end": v(-28.33, 73) * mm});
            skLineSegment(sketch, "E1210", {"start": v(-28.33, 73) * mm, "end": v(-28.61, 72.7) * mm});
            skLineSegment(sketch, "E1211", {"start": v(-28.61, 72.7) * mm, "end": v(-28.86, 72.37) * mm});
            skLineSegment(sketch, "E1212", {"start": v(-28.86, 72.37) * mm, "end": v(-29.04, 71.99) * mm});
            skLineSegment(sketch, "E1213", {"start": v(-61.5, 6.65) * mm, "end": v(-61.46, 6.23) * mm});
            skLineSegment(sketch, "E1214", {"start": v(-29.14, 71.6) * mm, "end": v(-29.18, 71.17) * mm});
            skLineSegment(sketch, "E1215", {"start": v(-29.18, 71.17) * mm, "end": v(-29.14, 70.75) * mm});
            skLineSegment(sketch, "E1216", {"start": v(-29.14, 70.75) * mm, "end": v(-29.04, 70.36) * mm});
            skLineSegment(sketch, "E1217", {"start": v(-29.04, 70.36) * mm, "end": v(-28.86, 69.97) * mm});
            skLineSegment(sketch, "E1218", {"start": v(-28.86, 69.97) * mm, "end": v(-28.61, 69.62) * mm});
            skLineSegment(sketch, "E1219", {"start": v(-28.61, 69.62) * mm, "end": v(-28.33, 69.34) * mm});
            skLineSegment(sketch, "E1220", {"start": v(-28.33, 69.34) * mm, "end": v(-27.98, 69.1) * mm});
            skLineSegment(sketch, "E1221", {"start": v(-27.98, 69.1) * mm, "end": v(-27.63, 68.92) * mm});
            skLineSegment(sketch, "E1222", {"start": v(-27.63, 68.92) * mm, "end": v(-27.2, 68.81) * mm});
            skLineSegment(sketch, "E1223", {"start": v(-27.2, 68.81) * mm, "end": v(-26.78, 68.78) * mm});
            skLineSegment(sketch, "E1224", {"start": v(-26.78, 68.78) * mm, "end": v(-26.4, 68.81) * mm});
            skLineSegment(sketch, "E1225", {"start": v(-26.4, 68.81) * mm, "end": v(-25.97, 68.92) * mm});
            skLineSegment(sketch, "E1226", {"start": v(-25.97, 68.92) * mm, "end": v(-25.62, 69.1) * mm});
            skLineSegment(sketch, "E1227", {"start": v(-25.62, 69.1) * mm, "end": v(-25.26, 69.34) * mm});
            skLineSegment(sketch, "E1228", {"start": v(-25.26, 69.34) * mm, "end": v(-24.98, 69.62) * mm});
            skLineSegment(sketch, "E1229", {"start": v(-24.98, 69.62) * mm, "end": v(-24.73, 69.97) * mm});
            skLineSegment(sketch, "E1230", {"start": v(-24.73, 69.97) * mm, "end": v(-24.56, 70.36) * mm});
            skLineSegment(sketch, "E1231", {"start": v(-24.56, 70.36) * mm, "end": v(-24.45, 70.75) * mm});
            skLineSegment(sketch, "E1232", {"start": v(-24.45, 70.75) * mm, "end": v(-24.42, 71.17) * mm});
            skLineSegment(sketch, "E1233", {"start": v(-24.42, 71.17) * mm, "end": v(-24.45, 71.6) * mm});
            skLineSegment(sketch, "E1234", {"start": v(-40.75, 71.99) * mm, "end": v(-40.93, 72.37) * mm});
            skLineSegment(sketch, "E1235", {"start": v(-40.93, 72.37) * mm, "end": v(-41.17, 72.7) * mm});
            skLineSegment(sketch, "E1236", {"start": v(-41.17, 72.7) * mm, "end": v(-41.46, 73) * mm});
            skLineSegment(sketch, "E1237", {"start": v(-41.46, 73) * mm, "end": v(-41.8, 73.22) * mm});
            skLineSegment(sketch, "E1238", {"start": v(-41.8, 73.22) * mm, "end": v(-42.16, 73.4) * mm});
            skLineSegment(sketch, "E1239", {"start": v(-42.16, 73.4) * mm, "end": v(-42.58, 73.54) * mm});
            skLineSegment(sketch, "E1240", {"start": v(-42.58, 73.54) * mm, "end": v(-42.97, 73.57) * mm});
            skLineSegment(sketch, "E1241", {"start": v(-42.97, 73.57) * mm, "end": v(-43.4, 73.54) * mm});
            skLineSegment(sketch, "E1242", {"start": v(-43.4, 73.54) * mm, "end": v(-43.82, 73.4) * mm});
            skLineSegment(sketch, "E1243", {"start": v(-43.82, 73.4) * mm, "end": v(-44.17, 73.22) * mm});
            skLineSegment(sketch, "E1244", {"start": v(-44.17, 73.22) * mm, "end": v(-44.52, 73) * mm});
            skLineSegment(sketch, "E1245", {"start": v(-44.52, 73) * mm, "end": v(-44.8, 72.7) * mm});
            skLineSegment(sketch, "E1246", {"start": v(-44.8, 72.7) * mm, "end": v(-45.05, 72.37) * mm});
            skLineSegment(sketch, "E1247", {"start": v(-45.05, 72.37) * mm, "end": v(-45.23, 71.99) * mm});
            skLineSegment(sketch, "E1248", {"start": v(-45.23, 71.99) * mm, "end": v(-45.34, 71.6) * mm});
            skLineSegment(sketch, "E1249", {"start": v(-45.34, 71.6) * mm, "end": v(-45.37, 71.17) * mm});
            skLineSegment(sketch, "E1250", {"start": v(-45.37, 71.17) * mm, "end": v(-45.34, 70.75) * mm});
            skLineSegment(sketch, "E1251", {"start": v(-45.34, 70.75) * mm, "end": v(-45.23, 70.36) * mm});
            skLineSegment(sketch, "E1252", {"start": v(-45.23, 70.36) * mm, "end": v(-45.05, 69.97) * mm});
            skLineSegment(sketch, "E1253", {"start": v(-45.05, 69.97) * mm, "end": v(-44.8, 69.62) * mm});
            skLineSegment(sketch, "E1254", {"start": v(-44.8, 69.62) * mm, "end": v(-44.52, 69.34) * mm});
            skLineSegment(sketch, "E1255", {"start": v(-44.52, 69.34) * mm, "end": v(-44.17, 69.1) * mm});
            skLineSegment(sketch, "E1256", {"start": v(-44.17, 69.1) * mm, "end": v(-43.82, 68.92) * mm});
            skLineSegment(sketch, "E1257", {"start": v(-43.82, 68.92) * mm, "end": v(-43.4, 68.81) * mm});
            skLineSegment(sketch, "E1258", {"start": v(-43.4, 68.81) * mm, "end": v(-42.97, 68.78) * mm});
            skLineSegment(sketch, "E1259", {"start": v(-42.97, 68.78) * mm, "end": v(-42.58, 68.81) * mm});
            skLineSegment(sketch, "E1260", {"start": v(-42.58, 68.81) * mm, "end": v(-42.16, 68.92) * mm});
            skLineSegment(sketch, "E1261", {"start": v(-42.16, 68.92) * mm, "end": v(-41.8, 69.1) * mm});
            skLineSegment(sketch, "E1262", {"start": v(-41.8, 69.1) * mm, "end": v(-41.46, 69.34) * mm});
            skLineSegment(sketch, "E1263", {"start": v(-41.46, 69.34) * mm, "end": v(-41.17, 69.62) * mm});
            skLineSegment(sketch, "E1264", {"start": v(-41.17, 69.62) * mm, "end": v(-40.93, 69.97) * mm});
            skLineSegment(sketch, "E1265", {"start": v(-40.93, 69.97) * mm, "end": v(-40.75, 70.36) * mm});
            skLineSegment(sketch, "E1266", {"start": v(-40.75, 70.36) * mm, "end": v(-40.64, 70.75) * mm});
            skLineSegment(sketch, "E1267", {"start": v(-40.64, 70.75) * mm, "end": v(-40.6, 71.17) * mm});
            skLineSegment(sketch, "E1268", {"start": v(-40.6, 71.17) * mm, "end": v(-40.64, 71.6) * mm});
            skLineSegment(sketch, "E1269", {"start": v(-14.75, 54.91) * mm, "end": v(-14.75, 48.56) * mm});
            skLineSegment(sketch, "E1270", {"start": v(-14.75, 48.56) * mm, "end": v(-11.75, 48.56) * mm});
            skLineSegment(sketch, "E1271", {"start": v(-11.75, 48.56) * mm, "end": v(-11.75, 54.91) * mm});
            skLineSegment(sketch, "E1272", {"start": v(-18.84, 24.25) * mm, "end": v(-19.02, 24.57) * mm});
            skLineSegment(sketch, "E1273", {"start": v(-19.02, 24.57) * mm, "end": v(-19.27, 24.89) * mm});
            skLineSegment(sketch, "E1274", {"start": v(-19.27, 24.89) * mm, "end": v(-19.55, 25.1) * mm});
            skLineSegment(sketch, "E1275", {"start": v(-19.55, 25.1) * mm, "end": v(-19.87, 25.28) * mm});
            skLineSegment(sketch, "E1276", {"start": v(-19.87, 25.28) * mm, "end": v(-20.22, 25.38) * mm});
            skLineSegment(sketch, "E1277", {"start": v(-20.22, 25.38) * mm, "end": v(-20.6, 25.42) * mm});
            skLineSegment(sketch, "E1278", {"start": v(-20.6, 25.42) * mm, "end": v(-20.96, 25.38) * mm});
            skLineSegment(sketch, "E1279", {"start": v(-20.96, 25.38) * mm, "end": v(-21.31, 25.28) * mm});
            skLineSegment(sketch, "E1280", {"start": v(-21.31, 25.28) * mm, "end": v(-21.66, 25.1) * mm});
            skLineSegment(sketch, "E1281", {"start": v(-21.66, 25.1) * mm, "end": v(-21.95, 24.89) * mm});
            skLineSegment(sketch, "E1282", {"start": v(-21.95, 24.89) * mm, "end": v(-22.2, 24.57) * mm});
            skLineSegment(sketch, "E1283", {"start": v(-22.2, 24.57) * mm, "end": v(-22.37, 24.25) * mm});
            skLineSegment(sketch, "E1284", {"start": v(-22.37, 24.25) * mm, "end": v(-22.48, 23.9) * mm});
            skLineSegment(sketch, "E1285", {"start": v(-22.48, 23.9) * mm, "end": v(-22.51, 23.55) * mm});
            skLineSegment(sketch, "E1286", {"start": v(-22.51, 23.55) * mm, "end": v(-22.48, 23.16) * mm});
            skLineSegment(sketch, "E1287", {"start": v(-22.48, 23.16) * mm, "end": v(-22.37, 22.8) * mm});
            skLineSegment(sketch, "E1288", {"start": v(-22.37, 22.8) * mm, "end": v(-22.2, 22.5) * mm});
            skLineSegment(sketch, "E1289", {"start": v(-22.2, 22.5) * mm, "end": v(-21.95, 22.2) * mm});
            skLineSegment(sketch, "E1290", {"start": v(-21.95, 22.2) * mm, "end": v(-21.66, 21.96) * mm});
            skLineSegment(sketch, "E1291", {"start": v(-21.66, 21.96) * mm, "end": v(-21.31, 21.79) * mm});
            skLineSegment(sketch, "E1292", {"start": v(-21.31, 21.79) * mm, "end": v(-20.96, 21.68) * mm});
            skLineSegment(sketch, "E1293", {"start": v(-20.96, 21.68) * mm, "end": v(-20.6, 21.64) * mm});
            skLineSegment(sketch, "E1294", {"start": v(-20.6, 21.64) * mm, "end": v(-20.22, 21.68) * mm});
            skLineSegment(sketch, "E1295", {"start": v(-20.22, 21.68) * mm, "end": v(-19.87, 21.79) * mm});
            skLineSegment(sketch, "E1296", {"start": v(-19.87, 21.79) * mm, "end": v(-19.55, 21.96) * mm});
            skLineSegment(sketch, "E1297", {"start": v(-19.55, 21.96) * mm, "end": v(-19.27, 22.2) * mm});
            skLineSegment(sketch, "E1298", {"start": v(-19.27, 22.2) * mm, "end": v(-19.02, 22.5) * mm});
            skLineSegment(sketch, "E1299", {"start": v(-19.02, 22.5) * mm, "end": v(-18.84, 22.8) * mm});
            skLineSegment(sketch, "E1300", {"start": v(-18.84, 22.8) * mm, "end": v(-18.74, 23.16) * mm});
            skLineSegment(sketch, "E1301", {"start": v(-18.74, 23.16) * mm, "end": v(-18.7, 23.55) * mm});
            skLineSegment(sketch, "E1302", {"start": v(-18.7, 23.55) * mm, "end": v(-18.74, 23.9) * mm});
            skLineSegment(sketch, "E1303", {"start": v(-67.53, 3.2) * mm, "end": v(-67.14, 2.98) * mm});
            skLineSegment(sketch, "E1304", {"start": v(-67.91, 3.44) * mm, "end": v(-67.53, 3.2) * mm});
            skLineSegment(sketch, "E1305", {"start": v(-68.2, 3.76) * mm, "end": v(-67.91, 3.44) * mm});
            skLineSegment(sketch, "E1306", {"start": v(-68.48, 4.11) * mm, "end": v(-68.2, 3.76) * mm});
            skLineSegment(sketch, "E1307", {"start": v(-68.65, 4.5) * mm, "end": v(-68.48, 4.11) * mm});
            skLineSegment(sketch, "E1308", {"start": v(-68.76, 4.96) * mm, "end": v(-68.65, 4.5) * mm});
            skLineSegment(sketch, "E1309", {"start": v(-68.8, 5.38) * mm, "end": v(-68.76, 4.96) * mm});
            skLineSegment(sketch, "E1310", {"start": v(-68.8, 23.83) * mm, "end": v(-68.8, 5.38) * mm});
            skLineSegment(sketch, "E1311", {"start": v(-68.83, 24.3) * mm, "end": v(-68.8, 23.83) * mm});
            skLineSegment(sketch, "E1312", {"start": v(-68.97, 24.71) * mm, "end": v(-68.83, 24.3) * mm});
            skLineSegment(sketch, "E1313", {"start": v(-17.54, 69.1) * mm, "end": v(-17.18, 69.34) * mm});
            skLineSegment(sketch, "E1314", {"start": v(-17.18, 69.34) * mm, "end": v(-16.9, 69.62) * mm});
            skLineSegment(sketch, "E1315", {"start": v(-16.9, 69.62) * mm, "end": v(-16.65, 69.97) * mm});
            skLineSegment(sketch, "E1316", {"start": v(-16.65, 69.97) * mm, "end": v(-16.48, 70.36) * mm});
            skLineSegment(sketch, "E1317", {"start": v(-16.48, 70.36) * mm, "end": v(-16.37, 70.75) * mm});
            skLineSegment(sketch, "E1318", {"start": v(-16.37, 70.75) * mm, "end": v(-16.34, 71.17) * mm});
            skLineSegment(sketch, "E1319", {"start": v(-16.34, 71.17) * mm, "end": v(-16.37, 71.6) * mm});
            skLineSegment(sketch, "E1320", {"start": v(-32.6, 71.99) * mm, "end": v(-32.78, 72.37) * mm});
            skLineSegment(sketch, "E1321", {"start": v(-32.78, 72.37) * mm, "end": v(-33.02, 72.7) * mm});
            skLineSegment(sketch, "E1322", {"start": v(-33.02, 72.7) * mm, "end": v(-33.34, 73) * mm});
            skLineSegment(sketch, "E1323", {"start": v(-33.34, 73) * mm, "end": v(-33.66, 73.22) * mm});
            skLineSegment(sketch, "E1324", {"start": v(-33.66, 73.22) * mm, "end": v(-34.05, 73.4) * mm});
            skLineSegment(sketch, "E1325", {"start": v(-34.05, 73.4) * mm, "end": v(-34.43, 73.54) * mm});
            skLineSegment(sketch, "E1326", {"start": v(-34.43, 73.54) * mm, "end": v(-34.86, 73.57) * mm});
            skLineSegment(sketch, "E1327", {"start": v(-34.86, 73.57) * mm, "end": v(-35.28, 73.54) * mm});
            skLineSegment(sketch, "E1328", {"start": v(-35.28, 73.54) * mm, "end": v(-35.67, 73.4) * mm});
            skLineSegment(sketch, "E1329", {"start": v(-35.67, 73.4) * mm, "end": v(-36.06, 73.22) * mm});
            skLineSegment(sketch, "E1330", {"start": v(-36.06, 73.22) * mm, "end": v(-36.41, 73) * mm});
            skLineSegment(sketch, "E1331", {"start": v(-36.41, 73) * mm, "end": v(-36.7, 72.7) * mm});
            skLineSegment(sketch, "E1332", {"start": v(-36.7, 72.7) * mm, "end": v(-36.94, 72.37) * mm});
            skLineSegment(sketch, "E1333", {"start": v(-36.94, 72.37) * mm, "end": v(-37.12, 71.99) * mm});
            skLineSegment(sketch, "E1334", {"start": v(-37.12, 71.99) * mm, "end": v(-37.22, 71.6) * mm});
            skLineSegment(sketch, "E1335", {"start": v(-37.22, 71.6) * mm, "end": v(-37.26, 71.17) * mm});
            skLineSegment(sketch, "E1336", {"start": v(-37.26, 71.17) * mm, "end": v(-37.22, 70.75) * mm});
            skLineSegment(sketch, "E1337", {"start": v(-37.22, 70.75) * mm, "end": v(-37.12, 70.36) * mm});
            skLineSegment(sketch, "E1338", {"start": v(-37.12, 70.36) * mm, "end": v(-36.94, 69.97) * mm});
            skLineSegment(sketch, "E1339", {"start": v(-36.94, 69.97) * mm, "end": v(-36.7, 69.62) * mm});
            skLineSegment(sketch, "E1340", {"start": v(-36.7, 69.62) * mm, "end": v(-36.41, 69.34) * mm});
            skLineSegment(sketch, "E1341", {"start": v(-36.41, 69.34) * mm, "end": v(-36.06, 69.1) * mm});
            skLineSegment(sketch, "E1342", {"start": v(-36.06, 69.1) * mm, "end": v(-35.67, 68.92) * mm});
            skLineSegment(sketch, "E1343", {"start": v(-35.67, 68.92) * mm, "end": v(-35.28, 68.81) * mm});
            skLineSegment(sketch, "E1344", {"start": v(-35.28, 68.81) * mm, "end": v(-34.86, 68.78) * mm});
            skLineSegment(sketch, "E1345", {"start": v(-34.86, 68.78) * mm, "end": v(-34.43, 68.81) * mm});
            skLineSegment(sketch, "E1346", {"start": v(-34.43, 68.81) * mm, "end": v(-34.05, 68.92) * mm});
            skLineSegment(sketch, "E1347", {"start": v(-34.05, 68.92) * mm, "end": v(-33.66, 69.1) * mm});
            skLineSegment(sketch, "E1348", {"start": v(-33.66, 69.1) * mm, "end": v(-33.34, 69.34) * mm});
            skLineSegment(sketch, "E1349", {"start": v(-33.34, 69.34) * mm, "end": v(-33.02, 69.62) * mm});
            skLineSegment(sketch, "E1350", {"start": v(-33.02, 69.62) * mm, "end": v(-32.78, 69.97) * mm});
            skLineSegment(sketch, "E1351", {"start": v(-32.78, 69.97) * mm, "end": v(-32.6, 70.36) * mm});
            skLineSegment(sketch, "E1352", {"start": v(-32.6, 70.36) * mm, "end": v(-32.5, 70.75) * mm});
            skLineSegment(sketch, "E1353", {"start": v(-32.5, 70.75) * mm, "end": v(-32.46, 71.17) * mm});
            skLineSegment(sketch, "E1354", {"start": v(-32.46, 71.17) * mm, "end": v(-32.5, 71.6) * mm});
            skLineSegment(sketch, "E1355", {"start": v(-11.75, 35.86) * mm, "end": v(-11.75, 42.21) * mm});
            skLineSegment(sketch, "E1356", {"start": v(-11.75, 42.21) * mm, "end": v(-14.75, 42.21) * mm});
            skLineSegment(sketch, "E1357", {"start": v(-14.75, 42.21) * mm, "end": v(-14.75, 35.86) * mm});
            skLineSegment(sketch, "E1358", {"start": v(-48.8, 71.99) * mm, "end": v(-48.97, 72.37) * mm});
            skLineSegment(sketch, "E1359", {"start": v(-48.97, 72.37) * mm, "end": v(-49.22, 72.7) * mm});
            skLineSegment(sketch, "E1360", {"start": v(-49.22, 72.7) * mm, "end": v(-49.53, 73) * mm});
            skLineSegment(sketch, "E1361", {"start": v(-11.72, 74.95) * mm, "end": v(-12.14, 74.98) * mm});
            skLineSegment(sketch, "E1362", {"start": v(-11.26, 74.84) * mm, "end": v(-11.72, 74.95) * mm});
            skLineSegment(sketch, "E1363", {"start": v(-10.87, 74.63) * mm, "end": v(-11.26, 74.84) * mm});
            skLineSegment(sketch, "E1364", {"start": v(-10.52, 74.38) * mm, "end": v(-10.87, 74.63) * mm});
            skLineSegment(sketch, "E1365", {"start": v(-10.2, 74.07) * mm, "end": v(-10.52, 74.38) * mm});
            skLineSegment(sketch, "E1366", {"start": v(-9.95, 73.71) * mm, "end": v(-10.2, 74.07) * mm});
            skLineSegment(sketch, "E1367", {"start": v(-9.74, 73.3) * mm, "end": v(-9.95, 73.71) * mm});
            skLineSegment(sketch, "E1368", {"start": v(-9.63, 72.87) * mm, "end": v(-9.74, 73.3) * mm});
            skLineSegment(sketch, "E1369", {"start": v(-9.6, 72.44) * mm, "end": v(-9.63, 72.87) * mm});
            skLineSegment(sketch, "E1370", {"start": v(-9.6, 53.96) * mm, "end": v(-9.6, 72.44) * mm});
            skLineSegment(sketch, "E1371", {"start": v(-9.56, 53.54) * mm, "end": v(-9.6, 53.96) * mm});
            skLineSegment(sketch, "E1372", {"start": v(-9.46, 53.11) * mm, "end": v(-9.56, 53.54) * mm});
            skLineSegment(sketch, "E1373", {"start": v(-9.25, 52.69) * mm, "end": v(-9.46, 53.11) * mm});
            skLineSegment(sketch, "E1374", {"start": v(-9, 52.34) * mm, "end": v(-9.25, 52.69) * mm});
            skLineSegment(sketch, "E1375", {"start": v(-8.68, 52.02) * mm, "end": v(-9, 52.34) * mm});
            skLineSegment(sketch, "E1376", {"start": v(-8.33, 51.77) * mm, "end": v(-8.68, 52.02) * mm});
            skLineSegment(sketch, "E1377", {"start": v(-7.94, 51.6) * mm, "end": v(-8.33, 51.77) * mm});
            skLineSegment(sketch, "E1378", {"start": v(-7.52, 51.49) * mm, "end": v(-7.94, 51.6) * mm});
            skLineSegment(sketch, "E1379", {"start": v(-7.06, 51.42) * mm, "end": v(-7.52, 51.49) * mm});
            skLineSegment(sketch, "E1380", {"start": v(-5.93, 51.42) * mm, "end": v(-7.06, 51.42) * mm});
            skLineSegment(sketch, "E1381", {"start": v(-5.5, 51.38) * mm, "end": v(-5.93, 51.42) * mm});
            skLineSegment(sketch, "E1382", {"start": v(-5.05, 51.28) * mm, "end": v(-5.5, 51.38) * mm});
            skLineSegment(sketch, "E1383", {"start": v(-4.66, 51.1) * mm, "end": v(-5.05, 51.28) * mm});
            skLineSegment(sketch, "E1384", {"start": v(-4.3, 50.85) * mm, "end": v(-4.66, 51.1) * mm});
            skLineSegment(sketch, "E1385", {"start": v(-4, 50.54) * mm, "end": v(-4.3, 50.85) * mm});
            skLineSegment(sketch, "E1386", {"start": v(-3.74, 50.15) * mm, "end": v(-4, 50.54) * mm});
            skLineSegment(sketch, "E1387", {"start": v(-3.53, 49.76) * mm, "end": v(-3.74, 50.15) * mm});
            skLineSegment(sketch, "E1388", {"start": v(-3.43, 49.34) * mm, "end": v(-3.53, 49.76) * mm});
            skLineSegment(sketch, "E1389", {"start": v(-3.4, 48.88) * mm, "end": v(-3.43, 49.34) * mm});
            skLineSegment(sketch, "E1390", {"start": v(-3.4, 28.91) * mm, "end": v(-3.4, 48.88) * mm});
            skLineSegment(sketch, "E1391", {"start": v(-3.43, 28.49) * mm, "end": v(-3.4, 28.91) * mm});
            skLineSegment(sketch, "E1392", {"start": v(-3.53, 28.06) * mm, "end": v(-3.43, 28.49) * mm});
            skLineSegment(sketch, "E1393", {"start": v(-3.74, 27.64) * mm, "end": v(-3.53, 28.06) * mm});
            skLineSegment(sketch, "E1394", {"start": v(-4, 27.29) * mm, "end": v(-3.74, 27.64) * mm});
            skLineSegment(sketch, "E1395", {"start": v(-4.3, 26.97) * mm, "end": v(-4, 27.29) * mm});
            skLineSegment(sketch, "E1396", {"start": v(-4.66, 26.72) * mm, "end": v(-4.3, 26.97) * mm});
            skLineSegment(sketch, "E1397", {"start": v(-5.05, 26.55) * mm, "end": v(-4.66, 26.72) * mm});
            skLineSegment(sketch, "E1398", {"start": v(-58.32, 73.4) * mm, "end": v(-58.7, 73.54) * mm});
            skLineSegment(sketch, "E1399", {"start": v(-58.7, 73.54) * mm, "end": v(-59.13, 73.57) * mm});
            skLineSegment(sketch, "E1400", {"start": v(-59.13, 73.57) * mm, "end": v(-59.52, 73.54) * mm});
            skLineSegment(sketch, "E1401", {"start": v(-59.52, 73.54) * mm, "end": v(-59.94, 73.4) * mm});
            skLineSegment(sketch, "E1402", {"start": v(-59.94, 73.4) * mm, "end": v(-60.33, 73.22) * mm});
            skLineSegment(sketch, "E1403", {"start": v(-60.33, 73.22) * mm, "end": v(-60.65, 73) * mm});
            skLineSegment(sketch, "E1404", {"start": v(-60.65, 73) * mm, "end": v(-60.96, 72.7) * mm});
            skLineSegment(sketch, "E1405", {"start": v(-60.96, 72.7) * mm, "end": v(-61.18, 72.37) * mm});
            skLineSegment(sketch, "E1406", {"start": v(-61.18, 72.37) * mm, "end": v(-61.35, 71.99) * mm});
            skLineSegment(sketch, "E1407", {"start": v(-61.35, 71.99) * mm, "end": v(-61.46, 71.6) * mm});
            skLineSegment(sketch, "E1408", {"start": v(-61.46, 71.6) * mm, "end": v(-61.5, 71.17) * mm});
            skLineSegment(sketch, "E1409", {"start": v(-61.5, 71.17) * mm, "end": v(-61.46, 70.75) * mm});
            skLineSegment(sketch, "E1410", {"start": v(-61.46, 70.75) * mm, "end": v(-61.35, 70.36) * mm});
            skLineSegment(sketch, "E1411", {"start": v(-61.35, 70.36) * mm, "end": v(-61.18, 69.97) * mm});
            skLineSegment(sketch, "E1412", {"start": v(-61.18, 69.97) * mm, "end": v(-60.96, 69.62) * mm});
            skLineSegment(sketch, "E1413", {"start": v(-60.96, 69.62) * mm, "end": v(-60.65, 69.34) * mm});
            skLineSegment(sketch, "E1414", {"start": v(-60.65, 69.34) * mm, "end": v(-60.33, 69.1) * mm});
            skLineSegment(sketch, "E1415", {"start": v(-60.33, 69.1) * mm, "end": v(-59.94, 68.92) * mm});
            skLineSegment(sketch, "E1416", {"start": v(-59.94, 68.92) * mm, "end": v(-59.52, 68.81) * mm});
            skLineSegment(sketch, "E1417", {"start": v(-59.52, 68.81) * mm, "end": v(-59.13, 68.78) * mm});
            skLineSegment(sketch, "E1418", {"start": v(-59.13, 68.78) * mm, "end": v(-58.7, 68.81) * mm});
            skLineSegment(sketch, "E1419", {"start": v(-58.7, 68.81) * mm, "end": v(-58.32, 68.92) * mm});
            skLineSegment(sketch, "E1420", {"start": v(-58.32, 68.92) * mm, "end": v(-57.93, 69.1) * mm});
            skLineSegment(sketch, "E1421", {"start": v(-57.93, 69.1) * mm, "end": v(-57.58, 69.34) * mm});
            skLineSegment(sketch, "E1422", {"start": v(-29.04, 71.99) * mm, "end": v(-29.14, 71.6) * mm});
            skLineSegment(sketch, "E1423", {"start": v(-57.3, 69.62) * mm, "end": v(-57.05, 69.97) * mm});
            skLineSegment(sketch, "E1424", {"start": v(-57.05, 69.97) * mm, "end": v(-56.87, 70.36) * mm});
            skLineSegment(sketch, "E1425", {"start": v(-56.87, 70.36) * mm, "end": v(-56.77, 70.75) * mm});
            skLineSegment(sketch, "E1426", {"start": v(-56.77, 70.75) * mm, "end": v(-56.73, 71.17) * mm});
            skLineSegment(sketch, "E1427", {"start": v(-56.73, 71.17) * mm, "end": v(-56.77, 71.6) * mm});
            skLineSegment(sketch, "E1428", {"start": v(-55.43, 55.26) * mm, "end": v(-55.6, 55.58) * mm});
            skLineSegment(sketch, "E1429", {"start": v(-55.6, 55.58) * mm, "end": v(-55.85, 55.86) * mm});
            skLineSegment(sketch, "E1430", {"start": v(-55.85, 55.86) * mm, "end": v(-56.13, 56.11) * mm});
            skLineSegment(sketch, "E1431", {"start": v(-56.13, 56.11) * mm, "end": v(-56.45, 56.29) * mm});
            skLineSegment(sketch, "E1432", {"start": v(-56.45, 56.29) * mm, "end": v(-56.8, 56.4) * mm});
            skLineSegment(sketch, "E1433", {"start": v(-56.8, 56.4) * mm, "end": v(-57.19, 56.43) * mm});
            skLineSegment(sketch, "E1434", {"start": v(-57.19, 56.43) * mm, "end": v(-57.54, 56.4) * mm});
            skLineSegment(sketch, "E1435", {"start": v(-57.54, 56.4) * mm, "end": v(-57.9, 56.29) * mm});
            skLineSegment(sketch, "E1436", {"start": v(-57.9, 56.29) * mm, "end": v(-58.25, 56.11) * mm});
            skLineSegment(sketch, "E1437", {"start": v(-58.25, 56.11) * mm, "end": v(-58.53, 55.86) * mm});
            skLineSegment(sketch, "E1438", {"start": v(-58.53, 55.86) * mm, "end": v(-58.74, 55.58) * mm});
            skLineSegment(sketch, "E1439", {"start": v(-58.74, 55.58) * mm, "end": v(-58.92, 55.26) * mm});
            skLineSegment(sketch, "E1440", {"start": v(-58.92, 55.26) * mm, "end": v(-59.02, 54.88) * mm});
            skLineSegment(sketch, "E1441", {"start": v(-42.51, 13) * mm, "end": v(-36.13, 13) * mm});
            skLineSegment(sketch, "E1442", {"start": v(-36.13, 13) * mm, "end": v(-36.13, 16) * mm});
            skLineSegment(sketch, "E1443", {"start": v(-29.81, 64.22) * mm, "end": v(-29.81, 61.23) * mm});
            skLineSegment(sketch, "E1444", {"start": v(-29.81, 61.23) * mm, "end": v(-23.43, 61.23) * mm});
            skLineSegment(sketch, "E1445", {"start": v(-23.43, 61.23) * mm, "end": v(-23.43, 64.22) * mm});
            skLineSegment(sketch, "E1446", {"start": v(-55.21, 64.22) * mm, "end": v(-55.21, 61.23) * mm});
            skLineSegment(sketch, "E1447", {"start": v(-55.21, 61.23) * mm, "end": v(-48.83, 61.23) * mm});
            skLineSegment(sketch, "E1448", {"start": v(-48.83, 61.23) * mm, "end": v(-48.83, 64.22) * mm});
            skLineSegment(sketch, "E1449", {"start": v(-5.9, 48.46) * mm, "end": v(-6.07, 48.7) * mm});
            skLineSegment(sketch, "E1450", {"start": v(-6.07, 48.7) * mm, "end": v(-6.32, 48.91) * mm});
            skLineSegment(sketch, "E1451", {"start": v(-6.32, 48.91) * mm, "end": v(-6.6, 49.05) * mm});
            skLineSegment(sketch, "E1452", {"start": v(-6.6, 49.05) * mm, "end": v(-6.92, 49.13) * mm});
            skLineSegment(sketch, "E1453", {"start": v(-6.92, 49.13) * mm, "end": v(-7.24, 49.13) * mm});
            skLineSegment(sketch, "E1454", {"start": v(-7.24, 49.13) * mm, "end": v(-7.52, 49.05) * mm});
            skLineSegment(sketch, "E1455", {"start": v(-7.52, 49.05) * mm, "end": v(-7.8, 48.91) * mm});
            skLineSegment(sketch, "E1456", {"start": v(-7.8, 48.91) * mm, "end": v(-8.05, 48.7) * mm});
            skLineSegment(sketch, "E1457", {"start": v(-8.05, 48.7) * mm, "end": v(-8.22, 48.46) * mm});
            skLineSegment(sketch, "E1458", {"start": v(-8.22, 48.46) * mm, "end": v(-8.33, 48.17) * mm});
            skLineSegment(sketch, "E1459", {"start": v(-8.33, 48.17) * mm, "end": v(-8.36, 47.86) * mm});
            skLineSegment(sketch, "E1460", {"start": v(-8.36, 47.86) * mm, "end": v(-8.36, 29.97) * mm});
            skLineSegment(sketch, "E1461", {"start": v(-8.36, 29.97) * mm, "end": v(-8.33, 29.65) * mm});
            skLineSegment(sketch, "E1462", {"start": v(-8.33, 29.65) * mm, "end": v(-8.22, 29.37) * mm});
            skLineSegment(sketch, "E1463", {"start": v(-8.22, 29.37) * mm, "end": v(-8.05, 29.12) * mm});
            skLineSegment(sketch, "E1464", {"start": v(-8.05, 29.12) * mm, "end": v(-7.8, 28.91) * mm});
            skLineSegment(sketch, "E1465", {"start": v(-7.8, 28.91) * mm, "end": v(-7.52, 28.77) * mm});
            skLineSegment(sketch, "E1466", {"start": v(-7.52, 28.77) * mm, "end": v(-7.24, 28.66) * mm});
            skLineSegment(sketch, "E1467", {"start": v(-7.24, 28.66) * mm, "end": v(-6.92, 28.66) * mm});
            skLineSegment(sketch, "E1468", {"start": v(-6.92, 28.66) * mm, "end": v(-6.6, 28.77) * mm});
            skLineSegment(sketch, "E1469", {"start": v(-6.6, 28.77) * mm, "end": v(-6.32, 28.91) * mm});
            skLineSegment(sketch, "E1470", {"start": v(-6.32, 28.91) * mm, "end": v(-6.07, 29.12) * mm});
            skLineSegment(sketch, "E1471", {"start": v(-6.07, 29.12) * mm, "end": v(-5.9, 29.37) * mm});
            skLineSegment(sketch, "E1472", {"start": v(-5.9, 29.37) * mm, "end": v(-5.79, 29.65) * mm});
            skLineSegment(sketch, "E1473", {"start": v(-5.79, 29.65) * mm, "end": v(-5.75, 29.97) * mm});
            skLineSegment(sketch, "E1474", {"start": v(-5.75, 29.97) * mm, "end": v(-5.75, 47.86) * mm});
            skLineSegment(sketch, "E1475", {"start": v(-5.75, 47.86) * mm, "end": v(-5.79, 48.17) * mm});
            skLineSegment(sketch, "E1476", {"start": v(-53.3, 5.84) * mm, "end": v(-53.13, 5.45) * mm});
            skLineSegment(sketch, "E1477", {"start": v(-53.13, 5.45) * mm, "end": v(-52.89, 5.13) * mm});
            skLineSegment(sketch, "E1478", {"start": v(-52.89, 5.13) * mm, "end": v(-52.6, 4.82) * mm});
            skLineSegment(sketch, "E1479", {"start": v(-52.6, 4.82) * mm, "end": v(-52.25, 4.57) * mm});
            skLineSegment(sketch, "E1480", {"start": v(-52.25, 4.57) * mm, "end": v(-51.86, 4.4) * mm});
            skLineSegment(sketch, "E1481", {"start": v(-51.86, 4.4) * mm, "end": v(-51.47, 4.29) * mm});
            skLineSegment(sketch, "E1482", {"start": v(-51.47, 4.29) * mm, "end": v(-51.05, 4.25) * mm});
            skLineSegment(sketch, "E1483", {"start": v(-51.05, 4.25) * mm, "end": v(-50.63, 4.29) * mm});
            skLineSegment(sketch, "E1484", {"start": v(-50.63, 4.29) * mm, "end": v(-50.24, 4.4) * mm});
            skLineSegment(sketch, "E1485", {"start": v(-50.24, 4.4) * mm, "end": v(-49.85, 4.57) * mm});
            skLineSegment(sketch, "E1486", {"start": v(-49.85, 4.57) * mm, "end": v(-49.53, 4.82) * mm});
            skLineSegment(sketch, "E1487", {"start": v(-57.58, 69.34) * mm, "end": v(-57.3, 69.62) * mm});
            skLineSegment(sketch, "E1488", {"start": v(-69.15, 25.1) * mm, "end": v(-68.97, 24.71) * mm});
            skLineSegment(sketch, "E1489", {"start": v(-69.4, 25.49) * mm, "end": v(-69.15, 25.1) * mm});
            skLineSegment(sketch, "E1490", {"start": v(-69.71, 25.8) * mm, "end": v(-69.4, 25.49) * mm});
            skLineSegment(sketch, "E1491", {"start": v(-70.07, 26.05) * mm, "end": v(-69.71, 25.8) * mm});
            skLineSegment(sketch, "E1492", {"start": v(-70.49, 26.23) * mm, "end": v(-70.07, 26.05) * mm});
            skLineSegment(sketch, "E1493", {"start": v(-70.91, 26.34) * mm, "end": v(-70.49, 26.23) * mm});
            skLineSegment(sketch, "E1494", {"start": v(-71.34, 26.37) * mm, "end": v(-70.91, 26.34) * mm});
            skLineSegment(sketch, "E1495", {"start": v(-72.46, 26.37) * mm, "end": v(-71.34, 26.37) * mm});
            skLineSegment(sketch, "E1496", {"start": v(-72.92, 26.44) * mm, "end": v(-72.46, 26.37) * mm});
            skLineSegment(sketch, "E1497", {"start": v(-73.35, 26.55) * mm, "end": v(-72.92, 26.44) * mm});
            skLineSegment(sketch, "E1498", {"start": v(-73.73, 26.72) * mm, "end": v(-73.35, 26.55) * mm});
            skLineSegment(sketch, "E1499", {"start": v(-74.09, 26.97) * mm, "end": v(-73.73, 26.72) * mm});
            skLineSegment(sketch, "E1500", {"start": v(-74.4, 27.29) * mm, "end": v(-74.09, 26.97) * mm});
            skLineSegment(sketch, "E1501", {"start": v(-74.69, 27.64) * mm, "end": v(-74.4, 27.29) * mm});
            skLineSegment(sketch, "E1502", {"start": v(-74.86, 28.06) * mm, "end": v(-74.69, 27.64) * mm});
            skLineSegment(sketch, "E1503", {"start": v(-74.97, 28.49) * mm, "end": v(-74.86, 28.06) * mm});
            skLineSegment(sketch, "E1504", {"start": v(-75, 28.91) * mm, "end": v(-74.97, 28.49) * mm});
            skLineSegment(sketch, "E1505", {"start": v(-75, 48.88) * mm, "end": v(-75, 28.91) * mm});
            skLineSegment(sketch, "E1506", {"start": v(-74.97, 49.34) * mm, "end": v(-75, 48.88) * mm});
            skLineSegment(sketch, "E1507", {"start": v(-74.86, 49.76) * mm, "end": v(-74.97, 49.34) * mm});
            skLineSegment(sketch, "E1508", {"start": v(-74.69, 50.15) * mm, "end": v(-74.86, 49.76) * mm});
            skLineSegment(sketch, "E1509", {"start": v(-74.4, 50.54) * mm, "end": v(-74.69, 50.15) * mm});
            skLineSegment(sketch, "E1510", {"start": v(-74.09, 50.85) * mm, "end": v(-74.4, 50.54) * mm});
            skLineSegment(sketch, "E1511", {"start": v(-73.73, 51.1) * mm, "end": v(-74.09, 50.85) * mm});
            skLineSegment(sketch, "E1512", {"start": v(-73.35, 51.28) * mm, "end": v(-73.73, 51.1) * mm});
            skLineSegment(sketch, "E1513", {"start": v(-72.92, 51.38) * mm, "end": v(-73.35, 51.28) * mm});
            skLineSegment(sketch, "E1514", {"start": v(-72.46, 51.42) * mm, "end": v(-72.92, 51.38) * mm});
            skLineSegment(sketch, "E1515", {"start": v(-71.34, 51.42) * mm, "end": v(-72.46, 51.42) * mm});
            skLineSegment(sketch, "E1516", {"start": v(-70.91, 51.49) * mm, "end": v(-71.34, 51.42) * mm});
            skLineSegment(sketch, "E1517", {"start": v(-70.49, 51.6) * mm, "end": v(-70.91, 51.49) * mm});
            skLineSegment(sketch, "E1518", {"start": v(-70.07, 51.77) * mm, "end": v(-70.49, 51.6) * mm});
            skLineSegment(sketch, "E1519", {"start": v(-69.71, 52.02) * mm, "end": v(-70.07, 51.77) * mm});
            skLineSegment(sketch, "E1520", {"start": v(-69.4, 52.34) * mm, "end": v(-69.71, 52.02) * mm});
            skLineSegment(sketch, "E1521", {"start": v(-69.15, 52.69) * mm, "end": v(-69.4, 52.34) * mm});
            skLineSegment(sketch, "E1522", {"start": v(-68.97, 53.11) * mm, "end": v(-69.15, 52.69) * mm});
            skLineSegment(sketch, "E1523", {"start": v(-68.83, 53.54) * mm, "end": v(-68.97, 53.11) * mm});
            skLineSegment(sketch, "E1524", {"start": v(-68.8, 53.96) * mm, "end": v(-68.83, 53.54) * mm});
            skLineSegment(sketch, "E1525", {"start": v(-68.8, 72.44) * mm, "end": v(-68.8, 53.96) * mm});
            skLineSegment(sketch, "E1526", {"start": v(-68.76, 72.87) * mm, "end": v(-68.8, 72.44) * mm});
            skLineSegment(sketch, "E1527", {"start": v(-68.65, 73.3) * mm, "end": v(-68.76, 72.87) * mm});
            skLineSegment(sketch, "E1528", {"start": v(-68.48, 73.71) * mm, "end": v(-68.65, 73.3) * mm});
            skLineSegment(sketch, "E1529", {"start": v(-68.2, 74.07) * mm, "end": v(-68.48, 73.71) * mm});
            skLineSegment(sketch, "E1530", {"start": v(-67.91, 74.38) * mm, "end": v(-68.2, 74.07) * mm});
            skLineSegment(sketch, "E1531", {"start": v(-67.53, 74.63) * mm, "end": v(-67.91, 74.38) * mm});
            skLineSegment(sketch, "E1532", {"start": v(-67.14, 74.84) * mm, "end": v(-67.53, 74.63) * mm});
            skLineSegment(sketch, "E1533", {"start": v(-66.71, 74.95) * mm, "end": v(-67.14, 74.84) * mm});
            skLineSegment(sketch, "E1534", {"start": v(-66.26, 74.98) * mm, "end": v(-66.71, 74.95) * mm});
            skLineSegment(sketch, "E1535", {"start": v(-12.14, 74.98) * mm, "end": v(-66.26, 74.98) * mm});
            skLineSegment(sketch, "E1536", {"start": v(-5.5, 26.44) * mm, "end": v(-5.05, 26.55) * mm});
            skLineSegment(sketch, "E1537", {"start": v(-5.93, 26.37) * mm, "end": v(-5.5, 26.44) * mm});
            skLineSegment(sketch, "E1538", {"start": v(-7.06, 26.37) * mm, "end": v(-5.93, 26.37) * mm});
            skLineSegment(sketch, "E1539", {"start": v(-7.52, 26.34) * mm, "end": v(-7.06, 26.37) * mm});
            skLineSegment(sketch, "E1540", {"start": v(-7.94, 26.23) * mm, "end": v(-7.52, 26.34) * mm});
            skLineSegment(sketch, "E1541", {"start": v(-8.33, 26.05) * mm, "end": v(-7.94, 26.23) * mm});
            skLineSegment(sketch, "E1542", {"start": v(-8.68, 25.8) * mm, "end": v(-8.33, 26.05) * mm});
            skLineSegment(sketch, "E1543", {"start": v(-9, 25.49) * mm, "end": v(-8.68, 25.8) * mm});
            skLineSegment(sketch, "E1544", {"start": v(-9.25, 25.1) * mm, "end": v(-9, 25.49) * mm});
            skLineSegment(sketch, "E1545", {"start": v(-9.46, 24.71) * mm, "end": v(-9.25, 25.1) * mm});
            skLineSegment(sketch, "E1546", {"start": v(-9.56, 24.3) * mm, "end": v(-9.46, 24.71) * mm});
            skLineSegment(sketch, "E1547", {"start": v(-9.6, 23.83) * mm, "end": v(-9.56, 24.3) * mm});
            skLineSegment(sketch, "E1548", {"start": v(-9.6, 5.38) * mm, "end": v(-9.6, 23.83) * mm});
            skLineSegment(sketch, "E1549", {"start": v(-9.63, 4.96) * mm, "end": v(-9.6, 5.38) * mm});
            skLineSegment(sketch, "E1550", {"start": v(-9.74, 4.5) * mm, "end": v(-9.63, 4.96) * mm});
            skLineSegment(sketch, "E1551", {"start": v(-9.95, 4.11) * mm, "end": v(-9.74, 4.5) * mm});
            skLineSegment(sketch, "E1552", {"start": v(-10.2, 3.76) * mm, "end": v(-9.95, 4.11) * mm});
            skLineSegment(sketch, "E1553", {"start": v(-10.52, 3.44) * mm, "end": v(-10.2, 3.76) * mm});
            skLineSegment(sketch, "E1554", {"start": v(-10.87, 3.2) * mm, "end": v(-10.52, 3.44) * mm});
            skLineSegment(sketch, "E1555", {"start": v(-11.26, 2.98) * mm, "end": v(-10.87, 3.2) * mm});
            skLineSegment(sketch, "E1556", {"start": v(-11.72, 2.88) * mm, "end": v(-11.26, 2.98) * mm});
            skLineSegment(sketch, "E1557", {"start": v(-12.14, 2.84) * mm, "end": v(-11.72, 2.88) * mm});
            skLineSegment(sketch, "E1558", {"start": v(-66.26, 2.84) * mm, "end": v(-12.14, 2.84) * mm});
            skLineSegment(sketch, "E1559", {"start": v(-66.71, 2.88) * mm, "end": v(-66.26, 2.84) * mm});
            skLineSegment(sketch, "E1560", {"start": v(-14.68, -67.65) * mm, "end": v(-17.68, -67.65) * mm});
            skFitSpline(sketch, "E1561", {"points": [v(-17.68, -72.44) * mm, v(-16.02, -72.44) * mm, v(-14.68, -71.1) * mm, v(-14.68, -69.44) * mm]});
            skLineSegment(sketch, "E1562", {"start": v(-14.68, -69.44) * mm, "end": v(-14.68, -67.65) * mm});
            skLineSegment(sketch, "E1563", {"start": v(-24.8, -72.44) * mm, "end": v(-17.68, -72.44) * mm});
            skLineSegment(sketch, "E1564", {"start": v(-24.8, -75.43) * mm, "end": v(-24.8, -72.44) * mm});
            skLineSegment(sketch, "E1565", {"start": v(-31.15, -75.43) * mm, "end": v(-24.8, -75.43) * mm});
            skLineSegment(sketch, "E1566", {"start": v(-31.15, -72.44) * mm, "end": v(-31.15, -75.43) * mm});
            skLineSegment(sketch, "E1567", {"start": v(-37.5, -72.44) * mm, "end": v(-31.15, -72.44) * mm});
            skLineSegment(sketch, "E1568", {"start": v(-37.5, -75.43) * mm, "end": v(-37.5, -72.44) * mm});
            skLineSegment(sketch, "E1569", {"start": v(-43.85, -75.43) * mm, "end": v(-37.5, -75.43) * mm});
            skLineSegment(sketch, "E1570", {"start": v(-43.85, -72.44) * mm, "end": v(-43.85, -75.43) * mm});
            skLineSegment(sketch, "E1571", {"start": v(-50.2, -72.44) * mm, "end": v(-43.85, -72.44) * mm});
            skLineSegment(sketch, "E1572", {"start": v(-50.2, -75.43) * mm, "end": v(-50.2, -72.44) * mm});
            skLineSegment(sketch, "E1573", {"start": v(-56.59, -75.43) * mm, "end": v(-50.2, -75.43) * mm});
            skLineSegment(sketch, "E1574", {"start": v(-56.59, -72.44) * mm, "end": v(-56.59, -75.43) * mm});
            skFitSpline(sketch, "E1575", {"points": [v(-65.9, -69.44) * mm, v(-65.9, -71.1) * mm, v(-64.56, -72.44) * mm, v(-62.9, -72.44) * mm]});
            skLineSegment(sketch, "E1576", {"start": v(-62.9, -72.44) * mm, "end": v(-56.59, -72.44) * mm});
            skLineSegment(sketch, "E1577", {"start": v(-65.9, -67.65) * mm, "end": v(-65.9, -69.44) * mm});
            skLineSegment(sketch, "E1578", {"start": v(-62.9, -67.65) * mm, "end": v(-65.9, -67.65) * mm});
            skLineSegment(sketch, "E1579", {"start": v(-62.9, -61.27) * mm, "end": v(-62.9, -67.65) * mm});
            skLineSegment(sketch, "E1580", {"start": v(-65.9, -61.27) * mm, "end": v(-62.9, -61.27) * mm});
            skFitSpline(sketch, "E1581", {"points": [v(-62.9, -56.48) * mm, v(-64.56, -56.48) * mm, v(-65.9, -57.83) * mm, v(-65.9, -59.48) * mm]});
            skLineSegment(sketch, "E1582", {"start": v(-65.9, -61.27) * mm, "end": v(-65.9, -59.48) * mm});
            skLineSegment(sketch, "E1583", {"start": v(-62.9, -56.48) * mm, "end": v(-56.59, -56.48) * mm});
            skLineSegment(sketch, "E1584", {"start": v(-56.59, -56.48) * mm, "end": v(-56.59, -53.5) * mm});
            skLineSegment(sketch, "E1585", {"start": v(-56.59, -53.5) * mm, "end": v(-50.2, -53.5) * mm});
            skFitSpline(sketch, "E1586", {"points": [v(-14.68, -59.48) * mm, v(-14.68, -57.83) * mm, v(-16.02, -56.48) * mm, v(-17.68, -56.48) * mm]});
            skLineSegment(sketch, "E1587", {"start": v(-50.2, -56.48) * mm, "end": v(-43.85, -56.48) * mm});
            skLineSegment(sketch, "E1588", {"start": v(-43.85, -56.48) * mm, "end": v(-43.85, -53.5) * mm});
            skLineSegment(sketch, "E1589", {"start": v(-43.85, -53.5) * mm, "end": v(-37.5, -53.5) * mm});
            skLineSegment(sketch, "E1590", {"start": v(-37.5, -53.5) * mm, "end": v(-37.5, -56.48) * mm});
            skLineSegment(sketch, "E1591", {"start": v(-37.5, -56.48) * mm, "end": v(-31.15, -56.48) * mm});
            skLineSegment(sketch, "E1592", {"start": v(-31.15, -56.48) * mm, "end": v(-31.15, -53.5) * mm});
            skLineSegment(sketch, "E1593", {"start": v(-31.15, -53.5) * mm, "end": v(-24.8, -53.5) * mm});
            skLineSegment(sketch, "E1594", {"start": v(-24.8, -53.5) * mm, "end": v(-24.8, -56.48) * mm});
            skLineSegment(sketch, "E1595", {"start": v(-24.8, -56.48) * mm, "end": v(-17.68, -56.48) * mm});
            skLineSegment(sketch, "E1596", {"start": v(-14.68, -59.48) * mm, "end": v(-14.68, -61.27) * mm});
            skLineSegment(sketch, "E1597", {"start": v(-17.68, -61.27) * mm, "end": v(-14.68, -61.27) * mm});
            skFitSpline(sketch, "E1598", {"points": [v(-52.23, -63.93) * mm, v(-52.23, -66.87) * mm, v(-49.84, -69.26) * mm, v(-46.89, -69.26) * mm]});
            skFitSpline(sketch, "E1599", {"points": [v(-46.89, -69.26) * mm, v(-43.95, -69.26) * mm, v(-41.56, -66.87) * mm, v(-41.56, -63.93) * mm]});
            skFitSpline(sketch, "E1600", {"points": [v(-41.56, -63.93) * mm, v(-41.56, -60.98) * mm, v(-43.95, -58.6) * mm, v(-46.89, -58.6) * mm]});
            skFitSpline(sketch, "E1601", {"points": [v(-46.89, -58.6) * mm, v(-49.84, -58.6) * mm, v(-52.23, -60.98) * mm, v(-52.23, -63.93) * mm]});
            skFitSpline(sketch, "E1602", {"points": [v(-39.17, -64.61) * mm, v(-40.45, -64.61) * mm, v(-41.49, -65.65) * mm, v(-41.49, -66.93) * mm]});
            skFitSpline(sketch, "E1603", {"points": [v(-41.49, -66.93) * mm, v(-41.49, -68.22) * mm, v(-40.45, -69.26) * mm, v(-39.17, -69.26) * mm]});
            skLineSegment(sketch, "E1604", {"start": v(-17.68, -67.65) * mm, "end": v(-17.68, -61.27) * mm});
            skFitSpline(sketch, "E1605", {"points": [v(-29.22, -64.61) * mm, v(-27.93, -64.61) * mm, v(-26.89, -65.65) * mm, v(-26.89, -66.93) * mm]});
            skFitSpline(sketch, "E1606", {"points": [v(-26.89, -66.93) * mm, v(-26.89, -68.22) * mm, v(-27.93, -69.26) * mm, v(-29.22, -69.26) * mm]});
            skLineSegment(sketch, "E1607", {"start": v(-39.17, -69.26) * mm, "end": v(-29.22, -69.26) * mm});
            skLineSegment(sketch, "E1608", {"start": v(-29.22, -64.61) * mm, "end": v(-39.17, -64.61) * mm});
            skLineSegment(sketch, "E1609", {"start": v(-50.2, -53.5) * mm, "end": v(-50.2, -56.48) * mm});
            skLineSegment(sketch, "E1610", {"start": v(12.14, 75.66) * mm, "end": v(66.26, 75.66) * mm});
            skLineSegment(sketch, "E1611", {"start": v(68.8, 73.12) * mm, "end": v(68.8, 54.63) * mm});
            skLineSegment(sketch, "E1612", {"start": v(75, 49.55) * mm, "end": v(75, 29.59) * mm});
            skLineSegment(sketch, "E1613", {"start": v(68.8, 24.5) * mm, "end": v(68.8, 6.06) * mm});
            skLineSegment(sketch, "E1614", {"start": v(66.26, 3.52) * mm, "end": v(12.14, 3.52) * mm});
            skLineSegment(sketch, "E1615", {"start": v(9.6, 24.5) * mm, "end": v(9.6, 6.06) * mm});
            skLineSegment(sketch, "E1616", {"start": v(3.4, 49.55) * mm, "end": v(3.4, 29.59) * mm});
            skLineSegment(sketch, "E1617", {"start": v(9.6, 73.12) * mm, "end": v(9.6, 54.63) * mm});
            skArc(sketch, "E1618", {"start": v(66.26, 75.66) * mm, "mid": v(68.05, 74.92) * mm, "end": v(68.8, 73.12) * mm});
            skArc(sketch, "E1619", {"start": v(12.14, 75.66) * mm, "mid": v(10.34, 74.92) * mm, "end": v(9.6, 73.12) * mm});
            skArc(sketch, "E1620", {"start": v(9.6, 6.06) * mm, "mid": v(10.34, 4.26) * mm, "end": v(12.14, 3.52) * mm});
            skArc(sketch, "E1621", {"start": v(68.8, 6.06) * mm, "mid": v(68.05, 4.26) * mm, "end": v(66.26, 3.52) * mm});
            skArc(sketch, "E1622", {"start": v(68.8, 24.5) * mm, "mid": v(69.54, 26.3) * mm, "end": v(71.34, 27.05) * mm});
            skArc(sketch, "E1623", {"start": v(72.46, 27.05) * mm, "mid": v(74.26, 27.8) * mm, "end": v(75, 29.59) * mm});
            skArc(sketch, "E1624", {"start": v(75, 49.55) * mm, "mid": v(74.26, 51.35) * mm, "end": v(72.46, 52.1) * mm});
            skArc(sketch, "E1625", {"start": v(71.34, 52.1) * mm, "mid": v(69.54, 52.84) * mm, "end": v(68.8, 54.63) * mm});
            skArc(sketch, "E1626", {"start": v(3.4, 49.55) * mm, "mid": v(4.13, 51.35) * mm, "end": v(5.93, 52.1) * mm});
            skArc(sketch, "E1627", {"start": v(7.06, 52.1) * mm, "mid": v(8.86, 52.84) * mm, "end": v(9.6, 54.63) * mm});
            skArc(sketch, "E1628", {"start": v(3.4, 29.59) * mm, "mid": v(4.13, 27.8) * mm, "end": v(5.93, 27.05) * mm});
            skArc(sketch, "E1629", {"start": v(9.6, 24.5) * mm, "mid": v(8.86, 26.3) * mm, "end": v(7.06, 27.05) * mm});
            skLineSegment(sketch, "E1630", {"start": v(-50.21, -15.19) * mm, "end": v(-26.4, -15.24) * mm});
            skArc(sketch, "E1631.0.startCap", {"start": v(-50.22, -19) * mm, "mid": v(-54.02, -15.18) * mm, "end": v(-50.2, -11.38) * mm});
            skArc(sketch, "E1631.0.endCap", {"start": v(-26.38, -11.43) * mm, "mid": v(-22.58, -15.25) * mm, "end": v(-26.4, -19.05) * mm});
            skLineSegment(sketch, "E1631.0.left", {"start": v(-50.2, -11.38) * mm, "end": v(-26.38, -11.43) * mm});
            skLineSegment(sketch, "E1631.0.right", {"start": v(-50.22, -19) * mm, "end": v(-26.4, -19.05) * mm});
            skSolve(sketch);
        }
        {
            var Q0;
            Q0=makeQuery(id+"F0.imprint","IMPRINT",FACE,{"disambiguationData":[TD([[makeQuery(id+"F0.imprint","IMPRINT",EDGE,{"derivedFrom":sQuery(id+"F0.wireOp",EDGE,"E816")}),1.0]])]});
            extrude(context, id + "F1", {"entities" : qUnion([Q0]), "depth" : 2.8 * mm});
        }
        {
            var Q0;
            Q0=makeQuery(id+"F0.imprint","IMPRINT",FACE,{"disambiguationData":[TD([[makeQuery(id+"F0.imprint","IMPRINT",EDGE,{"derivedFrom":sQuery(id+"F0.wireOp",EDGE,"E196")}),1.0]])]});
            extrude(context, id + "F2", {"entities" : qUnion([Q0]), "depth" : 2.8 * mm});
        }
        {
            var Q0;
            Q0=makeQuery(id+"F0.imprint","IMPRINT",FACE,{"disambiguationData":[TD([[makeQuery(id+"F0.imprint","IMPRINT",EDGE,{"derivedFrom":sQuery(id+"F0.wireOp",EDGE,"E120")}),1.0]])]});
            extrude(context, id + "F3", {"entities" : qUnion([Q0]), "depth" : 2.8 * mm});
        }
        {
            var Q0;
            Q0=makeQuery(id+"F0.imprint","IMPRINT",FACE,{"disambiguationData":[TD([[makeQuery(id+"F0.imprint","IMPRINT",EDGE,{"derivedFrom":sQuery(id+"F0.wireOp",EDGE,"E44")}),1.0]])]});
            extrude(context, id + "F4", {"entities" : qUnion([Q0]), "depth" : 2.8 * mm});
        }
        {
            var Q0;
            Q0=makeQuery(id+"F0.imprint","IMPRINT",FACE,{"disambiguationData":[TD([[makeQuery(id+"F0.imprint","IMPRINT",EDGE,{"derivedFrom":sQuery(id+"F0.wireOp",EDGE,"E160")}),1.0]])]});
            extrude(context, id + "F5", {"entities" : qUnion([Q0]), "depth" : 2.8 * mm});
        }
    });
